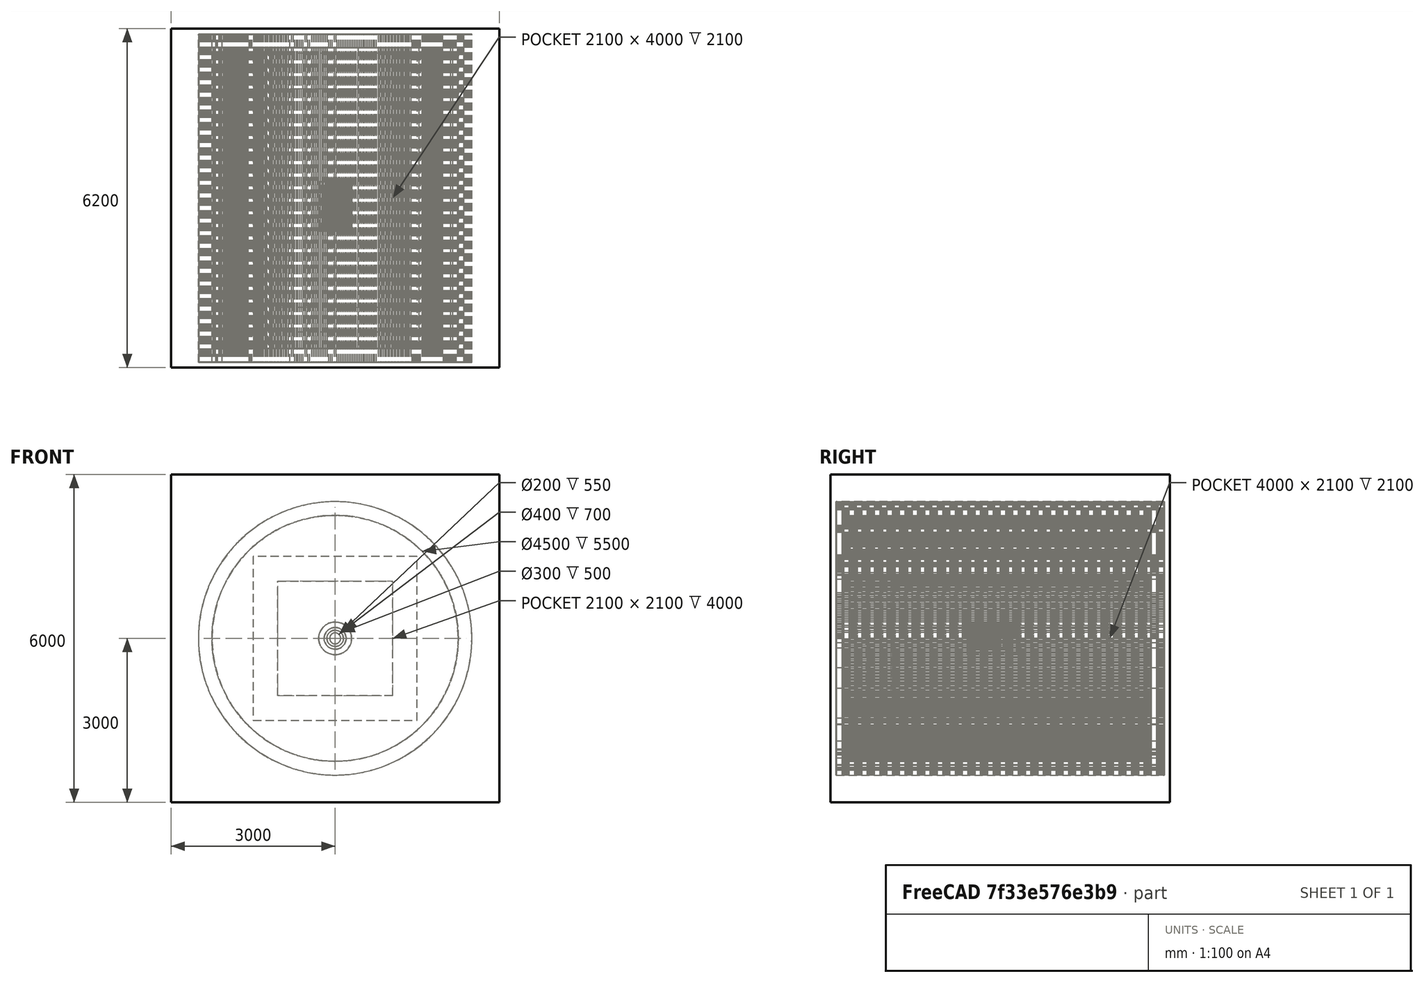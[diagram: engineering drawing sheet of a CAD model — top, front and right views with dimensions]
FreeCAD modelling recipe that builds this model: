
FCSTD DOCUMENT  (FreeCAD 1.0R39109 (Git))
Label: BeamDumpGDML_Optimized_01
License: All rights reserved
LicenseURL: https://en.wikipedia.org/wiki/All_rights_reserved
objects: App::DocumentObjectGroupPython×1252, Sketcher::SketchObject×8, PartDesign::Pad×6, Part::FeaturePython×5, App::Part×5, PartDesign::Body×4, Spreadsheet::Sheet×3, PartDesign::Revolution×2
note: 49 computed .brp shape members not serialized (recipe doc carries the construction recipe); baked Part::Feature solids carry a one-line shape summary decoded from their .brp

FEATURE [Spreadsheet::Sheet] defines
  cells = A1='constant; B1='HALFPI; C1(HALFPI)==pi / 2; A2='constant; B2='PI; C2(PI)==1 * pi; A3='constant; B3='TWOPI; C3(TWOPI)==2 * pi
FEATURE [Spreadsheet::Sheet] gdmlInfo
FEATURE [App::DocumentObjectGroupPython] Define  # scripted group (container) (typed FeaturePython)
  Group = -> [defines,gdmlInfo]
FEATURE [App::DocumentObjectGroupPython] HALFPI  # scripted group (container) (typed FeaturePython)
  name = HALFPI
  value = pi/2.
FEATURE [App::DocumentObjectGroupPython] PI  # scripted group (container) (typed FeaturePython)
  name = PI
  value = 1.*pi
FEATURE [App::DocumentObjectGroupPython] TWOPI  # scripted group (container) (typed FeaturePython)
  name = TWOPI
  value = 2.*pi
FEATURE [App::DocumentObjectGroupPython] Constants  # scripted group (container) (typed FeaturePython)
  Group = -> [HALFPI,PI,TWOPI]
FEATURE [App::DocumentObjectGroupPython] Quantities  # scripted group (container) (typed FeaturePython)
FEATURE [App::DocumentObjectGroupPython] Variables  # scripted group (container) (typed FeaturePython)
FEATURE [App::DocumentObjectGroupPython] Isotopes  # scripted group (container) (typed FeaturePython)
FEATURE [App::DocumentObjectGroupPython] Elements  # scripted group (container) (typed FeaturePython)
FEATURE [App::DocumentObjectGroupPython] Matrix  # scripted group (container) (typed FeaturePython)
FEATURE [App::DocumentObjectGroupPython] Surfaces  # scripted group (container) (typed FeaturePython)
FEATURE [App::DocumentObjectGroupPython] Opticals  # scripted group (container) (typed FeaturePython)
  Group = -> [Matrix,Surfaces]
FEATURE [App::DocumentObjectGroupPython] G4Isotopes  # scripted group (container) (typed FeaturePython)
FEATURE [App::DocumentObjectGroupPython] H_element  # scripted group (container) (typed FeaturePython)
  Z = 1
  atom_value = 1.008
  formula = H
  name = H_element
FEATURE [App::DocumentObjectGroupPython] He_element  # scripted group (container) (typed FeaturePython)
  Z = 2
  atom_value = 4.0026
  formula = He
  name = He_element
FEATURE [App::DocumentObjectGroupPython] Li_element  # scripted group (container) (typed FeaturePython)
  Z = 3
  atom_value = 6.94
  formula = Li
  name = Li_element
FEATURE [App::DocumentObjectGroupPython] Be_element  # scripted group (container) (typed FeaturePython)
  Z = 4
  atom_value = 9.01218
  formula = Be
  name = Be_element
FEATURE [App::DocumentObjectGroupPython] B_element  # scripted group (container) (typed FeaturePython)
  Z = 5
  atom_value = 10.81
  formula = B
  name = B_element
FEATURE [App::DocumentObjectGroupPython] C_element  # scripted group (container) (typed FeaturePython)
  Z = 6
  atom_value = 12.011
  formula = C
  name = C_element
FEATURE [App::DocumentObjectGroupPython] N_element  # scripted group (container) (typed FeaturePython)
  Z = 7
  atom_value = 14.007
  formula = N
  name = N_element
FEATURE [App::DocumentObjectGroupPython] O_element  # scripted group (container) (typed FeaturePython)
  Z = 8
  atom_value = 15.999
  formula = O
  name = O_element
FEATURE [App::DocumentObjectGroupPython] F_element  # scripted group (container) (typed FeaturePython)
  Z = 9
  atom_value = 18.9984
  formula = F
  name = F_element
FEATURE [App::DocumentObjectGroupPython] Ne_element  # scripted group (container) (typed FeaturePython)
  Z = 10
  atom_value = 20.1797
  formula = Ne
  name = Ne_element
FEATURE [App::DocumentObjectGroupPython] Na_element  # scripted group (container) (typed FeaturePython)
  Z = 11
  atom_value = 22.9898
  formula = Na
  name = Na_element
FEATURE [App::DocumentObjectGroupPython] Mg_element  # scripted group (container) (typed FeaturePython)
  Z = 12
  atom_value = 24.305
  formula = Mg
  name = Mg_element
FEATURE [App::DocumentObjectGroupPython] Al_element  # scripted group (container) (typed FeaturePython)
  Z = 13
  atom_value = 26.9815
  formula = Al
  name = Al_element
FEATURE [App::DocumentObjectGroupPython] Si_element  # scripted group (container) (typed FeaturePython)
  Z = 14
  atom_value = 28.085
  formula = Si
  name = Si_element
FEATURE [App::DocumentObjectGroupPython] P_element  # scripted group (container) (typed FeaturePython)
  Z = 15
  atom_value = 30.9738
  formula = P
  name = P_element
FEATURE [App::DocumentObjectGroupPython] S_element  # scripted group (container) (typed FeaturePython)
  Z = 16
  atom_value = 32.06
  formula = S
  name = S_element
FEATURE [App::DocumentObjectGroupPython] Cl_element  # scripted group (container) (typed FeaturePython)
  Z = 17
  atom_value = 35.45
  formula = Cl
  name = Cl_element
FEATURE [App::DocumentObjectGroupPython] Ar_element  # scripted group (container) (typed FeaturePython)
  Z = 18
  atom_value = 39.95
  formula = Ar
  name = Ar_element
FEATURE [App::DocumentObjectGroupPython] K_element  # scripted group (container) (typed FeaturePython)
  Z = 19
  atom_value = 39.0983
  formula = K
  name = K_element
FEATURE [App::DocumentObjectGroupPython] Ca_element  # scripted group (container) (typed FeaturePython)
  Z = 20
  atom_value = 40.078
  formula = Ca
  name = Ca_element
FEATURE [App::DocumentObjectGroupPython] Sc_element  # scripted group (container) (typed FeaturePython)
  Z = 21
  atom_value = 44.9559
  formula = Sc
  name = Sc_element
FEATURE [App::DocumentObjectGroupPython] Ti_element  # scripted group (container) (typed FeaturePython)
  Z = 22
  atom_value = 47.867
  formula = Ti
  name = Ti_element
FEATURE [App::DocumentObjectGroupPython] V_element  # scripted group (container) (typed FeaturePython)
  Z = 23
  atom_value = 50.9415
  formula = V
  name = V_element
FEATURE [App::DocumentObjectGroupPython] Cr_element  # scripted group (container) (typed FeaturePython)
  Z = 24
  atom_value = 51.9961
  formula = Cr
  name = Cr_element
FEATURE [App::DocumentObjectGroupPython] Mn_element  # scripted group (container) (typed FeaturePython)
  Z = 25
  atom_value = 54.938
  formula = Mn
  name = Mn_element
FEATURE [App::DocumentObjectGroupPython] Fe_element  # scripted group (container) (typed FeaturePython)
  Z = 26
  atom_value = 55.845
  formula = Fe
  name = Fe_element
FEATURE [App::DocumentObjectGroupPython] Co_element  # scripted group (container) (typed FeaturePython)
  Z = 27
  atom_value = 58.9332
  formula = Co
  name = Co_element
FEATURE [App::DocumentObjectGroupPython] Ni_element  # scripted group (container) (typed FeaturePython)
  Z = 28
  atom_value = 58.6934
  formula = Ni
  name = Ni_element
FEATURE [App::DocumentObjectGroupPython] Cu_element  # scripted group (container) (typed FeaturePython)
  Z = 29
  atom_value = 63.546
  formula = Cu
  name = Cu_element
FEATURE [App::DocumentObjectGroupPython] Zn_element  # scripted group (container) (typed FeaturePython)
  Z = 30
  atom_value = 65.38
  formula = Zn
  name = Zn_element
FEATURE [App::DocumentObjectGroupPython] Ga_element  # scripted group (container) (typed FeaturePython)
  Z = 31
  atom_value = 69.723
  formula = Ga
  name = Ga_element
FEATURE [App::DocumentObjectGroupPython] Ge_element  # scripted group (container) (typed FeaturePython)
  Z = 32
  atom_value = 72.63
  formula = Ge
  name = Ge_element
FEATURE [App::DocumentObjectGroupPython] As_element  # scripted group (container) (typed FeaturePython)
  Z = 33
  atom_value = 74.9216
  formula = As
  name = As_element
FEATURE [App::DocumentObjectGroupPython] Se_element  # scripted group (container) (typed FeaturePython)
  Z = 34
  atom_value = 78.971
  formula = Se
  name = Se_element
FEATURE [App::DocumentObjectGroupPython] Br_element  # scripted group (container) (typed FeaturePython)
  Z = 35
  atom_value = 79.904
  formula = Br
  name = Br_element
FEATURE [App::DocumentObjectGroupPython] Kr_element  # scripted group (container) (typed FeaturePython)
  Z = 36
  atom_value = 83.798
  formula = Kr
  name = Kr_element
FEATURE [App::DocumentObjectGroupPython] Rb_element  # scripted group (container) (typed FeaturePython)
  Z = 37
  atom_value = 85.4678
  formula = Rb
  name = Rb_element
FEATURE [App::DocumentObjectGroupPython] Sr_element  # scripted group (container) (typed FeaturePython)
  Z = 38
  atom_value = 87.62
  formula = Sr
  name = Sr_element
FEATURE [App::DocumentObjectGroupPython] Y_element  # scripted group (container) (typed FeaturePython)
  Z = 39
  atom_value = 88.9058
  formula = Y
  name = Y_element
FEATURE [App::DocumentObjectGroupPython] Zr_element  # scripted group (container) (typed FeaturePython)
  Z = 40
  atom_value = 91.224
  formula = Zr
  name = Zr_element
FEATURE [App::DocumentObjectGroupPython] Nb_element  # scripted group (container) (typed FeaturePython)
  Z = 41
  atom_value = 92.9064
  formula = Nb
  name = Nb_element
FEATURE [App::DocumentObjectGroupPython] Mo_element  # scripted group (container) (typed FeaturePython)
  Z = 42
  atom_value = 95.95
  formula = Mo
  name = Mo_element
FEATURE [App::DocumentObjectGroupPython] Tc_element  # scripted group (container) (typed FeaturePython)
  Z = 43
  atom_value = 97
  formula = Tc
  name = Tc_element
FEATURE [App::DocumentObjectGroupPython] Ru_element  # scripted group (container) (typed FeaturePython)
  Z = 44
  atom_value = 101.07
  formula = Ru
  name = Ru_element
FEATURE [App::DocumentObjectGroupPython] Rh_element  # scripted group (container) (typed FeaturePython)
  Z = 45
  atom_value = 102.905
  formula = Rh
  name = Rh_element
FEATURE [App::DocumentObjectGroupPython] Pd_element  # scripted group (container) (typed FeaturePython)
  Z = 46
  atom_value = 106.42
  formula = Pd
  name = Pd_element
FEATURE [App::DocumentObjectGroupPython] Ag_element  # scripted group (container) (typed FeaturePython)
  Z = 47
  atom_value = 107.868
  formula = Ag
  name = Ag_element
FEATURE [App::DocumentObjectGroupPython] Cd_element  # scripted group (container) (typed FeaturePython)
  Z = 48
  atom_value = 112.414
  formula = Cd
  name = Cd_element
FEATURE [App::DocumentObjectGroupPython] In_element  # scripted group (container) (typed FeaturePython)
  Z = 49
  atom_value = 114.818
  formula = In
  name = In_element
FEATURE [App::DocumentObjectGroupPython] Sn_element  # scripted group (container) (typed FeaturePython)
  Z = 50
  atom_value = 118.71
  formula = Sn
  name = Sn_element
FEATURE [App::DocumentObjectGroupPython] Sb_element  # scripted group (container) (typed FeaturePython)
  Z = 51
  atom_value = 121.76
  formula = Sb
  name = Sb_element
FEATURE [App::DocumentObjectGroupPython] Te_element  # scripted group (container) (typed FeaturePython)
  Z = 52
  atom_value = 127.6
  formula = Te
  name = Te_element
FEATURE [App::DocumentObjectGroupPython] I_element  # scripted group (container) (typed FeaturePython)
  Z = 53
  atom_value = 126.904
  formula = I
  name = I_element
FEATURE [App::DocumentObjectGroupPython] Xe_element  # scripted group (container) (typed FeaturePython)
  Z = 54
  atom_value = 131.293
  formula = Xe
  name = Xe_element
FEATURE [App::DocumentObjectGroupPython] Cs_element  # scripted group (container) (typed FeaturePython)
  Z = 55
  atom_value = 132.905
  formula = Cs
  name = Cs_element
FEATURE [App::DocumentObjectGroupPython] Ba_element  # scripted group (container) (typed FeaturePython)
  Z = 56
  atom_value = 137.327
  formula = Ba
  name = Ba_element
FEATURE [App::DocumentObjectGroupPython] La_element  # scripted group (container) (typed FeaturePython)
  Z = 57
  atom_value = 138.905
  formula = La
  name = La_element
FEATURE [App::DocumentObjectGroupPython] Ce_element  # scripted group (container) (typed FeaturePython)
  Z = 58
  atom_value = 140.116
  formula = Ce
  name = Ce_element
FEATURE [App::DocumentObjectGroupPython] Pr_element  # scripted group (container) (typed FeaturePython)
  Z = 59
  atom_value = 140.908
  formula = Pr
  name = Pr_element
FEATURE [App::DocumentObjectGroupPython] Nd_element  # scripted group (container) (typed FeaturePython)
  Z = 60
  atom_value = 144.242
  formula = Nd
  name = Nd_element
FEATURE [App::DocumentObjectGroupPython] Pm_element  # scripted group (container) (typed FeaturePython)
  Z = 61
  atom_value = 145
  formula = Pm
  name = Pm_element
FEATURE [App::DocumentObjectGroupPython] Sm_element  # scripted group (container) (typed FeaturePython)
  Z = 62
  atom_value = 150.36
  formula = Sm
  name = Sm_element
FEATURE [App::DocumentObjectGroupPython] Eu_element  # scripted group (container) (typed FeaturePython)
  Z = 63
  atom_value = 151.964
  formula = Eu
  name = Eu_element
FEATURE [App::DocumentObjectGroupPython] Gd_element  # scripted group (container) (typed FeaturePython)
  Z = 64
  atom_value = 157.25
  formula = Gd
  name = Gd_element
FEATURE [App::DocumentObjectGroupPython] Tb_element  # scripted group (container) (typed FeaturePython)
  Z = 65
  atom_value = 158.925
  formula = Tb
  name = Tb_element
FEATURE [App::DocumentObjectGroupPython] Dy_element  # scripted group (container) (typed FeaturePython)
  Z = 66
  atom_value = 162.5
  formula = Dy
  name = Dy_element
FEATURE [App::DocumentObjectGroupPython] Ho_element  # scripted group (container) (typed FeaturePython)
  Z = 67
  atom_value = 164.93
  formula = Ho
  name = Ho_element
FEATURE [App::DocumentObjectGroupPython] Er_element  # scripted group (container) (typed FeaturePython)
  Z = 68
  atom_value = 167.259
  formula = Er
  name = Er_element
FEATURE [App::DocumentObjectGroupPython] Tm_element  # scripted group (container) (typed FeaturePython)
  Z = 69
  atom_value = 168.934
  formula = Tm
  name = Tm_element
FEATURE [App::DocumentObjectGroupPython] Yb_element  # scripted group (container) (typed FeaturePython)
  Z = 70
  atom_value = 173.045
  formula = Yb
  name = Yb_element
FEATURE [App::DocumentObjectGroupPython] Lu_element  # scripted group (container) (typed FeaturePython)
  Z = 71
  atom_value = 174.967
  formula = Lu
  name = Lu_element
FEATURE [App::DocumentObjectGroupPython] Hf_element  # scripted group (container) (typed FeaturePython)
  Z = 72
  atom_value = 178.49
  formula = Hf
  name = Hf_element
FEATURE [App::DocumentObjectGroupPython] Ta_element  # scripted group (container) (typed FeaturePython)
  Z = 73
  atom_value = 180.948
  formula = Ta
  name = Ta_element
FEATURE [App::DocumentObjectGroupPython] W_element  # scripted group (container) (typed FeaturePython)
  Z = 74
  atom_value = 183.84
  formula = W
  name = W_element
FEATURE [App::DocumentObjectGroupPython] Re_element  # scripted group (container) (typed FeaturePython)
  Z = 75
  atom_value = 186.207
  formula = Re
  name = Re_element
FEATURE [App::DocumentObjectGroupPython] Os_element  # scripted group (container) (typed FeaturePython)
  Z = 76
  atom_value = 190.23
  formula = Os
  name = Os_element
FEATURE [App::DocumentObjectGroupPython] Ir_element  # scripted group (container) (typed FeaturePython)
  Z = 77
  atom_value = 192.217
  formula = Ir
  name = Ir_element
FEATURE [App::DocumentObjectGroupPython] Pt_element  # scripted group (container) (typed FeaturePython)
  Z = 78
  atom_value = 195.084
  formula = Pt
  name = Pt_element
FEATURE [App::DocumentObjectGroupPython] Au_element  # scripted group (container) (typed FeaturePython)
  Z = 79
  atom_value = 196.967
  formula = Au
  name = Au_element
FEATURE [App::DocumentObjectGroupPython] Hg_element  # scripted group (container) (typed FeaturePython)
  Z = 80
  atom_value = 200.592
  formula = Hg
  name = Hg_element
FEATURE [App::DocumentObjectGroupPython] Tl_element  # scripted group (container) (typed FeaturePython)
  Z = 81
  atom_value = 204.38
  formula = Tl
  name = Tl_element
FEATURE [App::DocumentObjectGroupPython] Pb_element  # scripted group (container) (typed FeaturePython)
  Z = 82
  atom_value = 207.2
  formula = Pb
  name = Pb_element
FEATURE [App::DocumentObjectGroupPython] Bi_element  # scripted group (container) (typed FeaturePython)
  Z = 83
  atom_value = 208.98
  formula = Bi
  name = Bi_element
FEATURE [App::DocumentObjectGroupPython] Po_element  # scripted group (container) (typed FeaturePython)
  Z = 84
  atom_value = 209
  formula = Po
  name = Po_element
FEATURE [App::DocumentObjectGroupPython] At_element  # scripted group (container) (typed FeaturePython)
  Z = 85
  atom_value = 210
  formula = At
  name = At_element
FEATURE [App::DocumentObjectGroupPython] Rn_element  # scripted group (container) (typed FeaturePython)
  Z = 86
  atom_value = 222
  formula = Rn
  name = Rn_element
FEATURE [App::DocumentObjectGroupPython] Fr_element  # scripted group (container) (typed FeaturePython)
  Z = 87
  atom_value = 223
  formula = Fr
  name = Fr_element
FEATURE [App::DocumentObjectGroupPython] Ra_element  # scripted group (container) (typed FeaturePython)
  Z = 88
  atom_value = 226
  formula = Ra
  name = Ra_element
FEATURE [App::DocumentObjectGroupPython] Ac_element  # scripted group (container) (typed FeaturePython)
  Z = 89
  atom_value = 227
  formula = Ac
  name = Ac_element
FEATURE [App::DocumentObjectGroupPython] Th_element  # scripted group (container) (typed FeaturePython)
  Z = 90
  atom_value = 232.038
  formula = Th
  name = Th_element
FEATURE [App::DocumentObjectGroupPython] Pa_element  # scripted group (container) (typed FeaturePython)
  Z = 91
  atom_value = 231.036
  formula = Pa
  name = Pa_element
FEATURE [App::DocumentObjectGroupPython] U_element  # scripted group (container) (typed FeaturePython)
  Z = 92
  atom_value = 238.029
  formula = U
  name = U_element
FEATURE [App::DocumentObjectGroupPython] Np_element  # scripted group (container) (typed FeaturePython)
  Z = 93
  atom_value = 237
  formula = Np
  name = Np_element
FEATURE [App::DocumentObjectGroupPython] Pu_element  # scripted group (container) (typed FeaturePython)
  Z = 94
  atom_value = 244
  formula = Pu
  name = Pu_element
FEATURE [App::DocumentObjectGroupPython] Am_element  # scripted group (container) (typed FeaturePython)
  Z = 95
  atom_value = 243
  formula = Am
  name = Am_element
FEATURE [App::DocumentObjectGroupPython] Cm_element  # scripted group (container) (typed FeaturePython)
  Z = 96
  atom_value = 247
  formula = Cm
  name = Cm_element
FEATURE [App::DocumentObjectGroupPython] Bk_element  # scripted group (container) (typed FeaturePython)
  Z = 97
  atom_value = 247
  formula = Bk
  name = Bk_element
FEATURE [App::DocumentObjectGroupPython] Cf_element  # scripted group (container) (typed FeaturePython)
  Z = 98
  atom_value = 251
  formula = Cf
  name = Cf_element
FEATURE [App::DocumentObjectGroupPython] G4Elements  # scripted group (container) (typed FeaturePython)
  Group = -> [H_element,He_element,Li_element,Be_element,B_element,C_element,N_element,O_element,F_element,Ne_element,Na_element,Mg_element,Al_element,Si_element,P_element,S_element,Cl_element,Ar_element,K_element,Ca_element,Sc_element,Ti_element,V_element,Cr_element,Mn_element,Fe_element,Co_element,Ni_element,Cu_element,Zn_element,Ga_element,Ge_element,As_element,Se_element,Br_element,Kr_element,Rb_element,+61 more]
FEATURE [App::DocumentObjectGroupPython] H_element001  label="H_element : 0.101"  # scripted group (container) (typed FeaturePython)
  n = 0.101327
FEATURE [App::DocumentObjectGroupPython] C_element001  label="C_element : 0.775"  # scripted group (container) (typed FeaturePython)
  n = 0.7755
FEATURE [App::DocumentObjectGroupPython] N_element001  label="N_element : 0.035"  # scripted group (container) (typed FeaturePython)
  n = 0.035057
FEATURE [App::DocumentObjectGroupPython] O_element001  label="O_element : 0.052"  # scripted group (container) (typed FeaturePython)
  n = 0.0523159
FEATURE [App::DocumentObjectGroupPython] F_element001  label="F_element : 0.017"  # scripted group (container) (typed FeaturePython)
  n = 0.017422
FEATURE [App::DocumentObjectGroupPython] Ca_element001  label="Ca_element : 0.018"  # scripted group (container) (typed FeaturePython)
  n = 0.018378
FEATURE [App::DocumentObjectGroupPython] G4_A_150_TISSUE  label="G4_A-150_TISSUE"  # scripted group (container) (typed FeaturePython)
  Dunit = g/cm3
  Dvalue = 1.127
  Group = -> [H_element001,C_element001,N_element001,O_element001,F_element001,Ca_element001]
  conduct = 2
  density = 1
  expand = 3
  formula = G4_A-150_TISSUE
  name = G4_A-150_TISSUE
  specific = 4
FEATURE [App::DocumentObjectGroupPython] C_element002  label="C_element : 3"  # scripted group (container) (typed FeaturePython)
  n = 3
  ref = C_element
FEATURE [App::DocumentObjectGroupPython] H_element002  label="H_element : 6"  # scripted group (container) (typed FeaturePython)
  n = 6
  ref = H_element
FEATURE [App::DocumentObjectGroupPython] O_element002  label="O_element : 1"  # scripted group (container) (typed FeaturePython)
  n = 1
  ref = O_element
FEATURE [App::DocumentObjectGroupPython] G4_ACETONE  # scripted group (container) (typed FeaturePython)
  Dunit = g/cm3
  Dvalue = 0.7899
  Group = -> [C_element002,H_element002,O_element002]
  conduct = 2
  density = 1
  expand = 3
  formula = G4_ACETONE
  name = G4_ACETONE
  specific = 4
FEATURE [App::DocumentObjectGroupPython] C_element003  label="C_element : 2"  # scripted group (container) (typed FeaturePython)
  n = 2
  ref = C_element
FEATURE [App::DocumentObjectGroupPython] H_element003  label="H_element : 2"  # scripted group (container) (typed FeaturePython)
  n = 2
  ref = H_element
FEATURE [App::DocumentObjectGroupPython] G4_ACETYLENE  # scripted group (container) (typed FeaturePython)
  Dunit = g/cm3
  Dvalue = 0.0010967
  Group = -> [C_element003,H_element003]
  conduct = 2
  density = 1
  expand = 3
  formula = G4_ACETYLENE
  name = G4_ACETYLENE
  specific = 4
FEATURE [App::DocumentObjectGroupPython] C_element004  label="C_element : 5"  # scripted group (container) (typed FeaturePython)
  n = 5
  ref = C_element
FEATURE [App::DocumentObjectGroupPython] H_element004  label="H_element : 5"  # scripted group (container) (typed FeaturePython)
  n = 5
  ref = H_element
FEATURE [App::DocumentObjectGroupPython] N_element002  label="N_element : 5"  # scripted group (container) (typed FeaturePython)
  n = 5
  ref = N_element
FEATURE [App::DocumentObjectGroupPython] G4_ADENINE  # scripted group (container) (typed FeaturePython)
  Dunit = g/cm3
  Dvalue = 1.6
  Group = -> [C_element004,H_element004,N_element002]
  conduct = 2
  density = 1
  expand = 3
  formula = G4_ADENINE
  name = G4_ADENINE
  specific = 4
FEATURE [App::DocumentObjectGroupPython] H_element005  label="H_element : 0.114"  # scripted group (container) (typed FeaturePython)
  n = 0.114
FEATURE [App::DocumentObjectGroupPython] C_element005  label="C_element : 0.598"  # scripted group (container) (typed FeaturePython)
  n = 0.598
FEATURE [App::DocumentObjectGroupPython] N_element003  label="N_element : 0.007"  # scripted group (container) (typed FeaturePython)
  n = 0.007
FEATURE [App::DocumentObjectGroupPython] O_element003  label="O_element : 0.278"  # scripted group (container) (typed FeaturePython)
  n = 0.278
FEATURE [App::DocumentObjectGroupPython] Na_element001  label="Na_element : 0.001"  # scripted group (container) (typed FeaturePython)
  n = 0.001
FEATURE [App::DocumentObjectGroupPython] S_element001  label="S_element : 0.001"  # scripted group (container) (typed FeaturePython)
  n = 0.001
FEATURE [App::DocumentObjectGroupPython] Cl_element001  label="Cl_element : 0.001"  # scripted group (container) (typed FeaturePython)
  n = 0.001
FEATURE [App::DocumentObjectGroupPython] G4_ADIPOSE_TISSUE_ICRP  # scripted group (container) (typed FeaturePython)
  Dunit = g/cm3
  Dvalue = 0.95
  Group = -> [H_element005,C_element005,N_element003,O_element003,Na_element001,S_element001,Cl_element001]
  conduct = 2
  density = 1
  expand = 3
  formula = G4_ADIPOSE_TISSUE_ICRP
  name = G4_ADIPOSE_TISSUE_ICRP
  specific = 4
FEATURE [App::DocumentObjectGroupPython] C_element006  label="C_element : 0.000"  # scripted group (container) (typed FeaturePython)
  n = 0.000124
FEATURE [App::DocumentObjectGroupPython] N_element004  label="N_element : 0.755"  # scripted group (container) (typed FeaturePython)
  n = 0.755268
FEATURE [App::DocumentObjectGroupPython] O_element004  label="O_element : 0.232"  # scripted group (container) (typed FeaturePython)
  n = 0.231781
FEATURE [App::DocumentObjectGroupPython] Ar_element001  label="Ar_element : 0.013"  # scripted group (container) (typed FeaturePython)
  n = 0.012827
FEATURE [App::DocumentObjectGroupPython] G4_AIR  # scripted group (container) (typed FeaturePython)
  Dunit = g/cm3
  Dvalue = 0.00120479
  Group = -> [C_element006,N_element004,O_element004,Ar_element001]
  conduct = 2
  density = 1
  expand = 3
  formula = G4_AIR
  name = G4_AIR
  specific = 4
FEATURE [App::DocumentObjectGroupPython] C_element007  label="C_element : 006"  # scripted group (container) (typed FeaturePython)
  n = 3
  ref = C_element
FEATURE [App::DocumentObjectGroupPython] H_element006  label="H_element : 7"  # scripted group (container) (typed FeaturePython)
  n = 7
  ref = H_element
FEATURE [App::DocumentObjectGroupPython] N_element005  label="N_element : 1"  # scripted group (container) (typed FeaturePython)
  n = 1
  ref = N_element
FEATURE [App::DocumentObjectGroupPython] O_element005  label="O_element : 2"  # scripted group (container) (typed FeaturePython)
  n = 2
  ref = O_element
FEATURE [App::DocumentObjectGroupPython] G4_ALANINE  # scripted group (container) (typed FeaturePython)
  Dunit = g/cm3
  Dvalue = 1.42
  Group = -> [C_element007,H_element006,N_element005,O_element005]
  conduct = 2
  density = 1
  expand = 3
  formula = G4_ALANINE
  name = G4_ALANINE
  specific = 4
FEATURE [App::DocumentObjectGroupPython] Al_element001  label="Al_element : 2"  # scripted group (container) (typed FeaturePython)
  n = 2
  ref = Al_element
FEATURE [App::DocumentObjectGroupPython] O_element006  label="O_element : 3"  # scripted group (container) (typed FeaturePython)
  n = 3
  ref = O_element
FEATURE [App::DocumentObjectGroupPython] G4_ALUMINUM_OXIDE  # scripted group (container) (typed FeaturePython)
  Dunit = g/cm3
  Dvalue = 3.97
  Group = -> [Al_element001,O_element006]
  conduct = 2
  density = 1
  expand = 3
  formula = G4_ALUMINUM_OXIDE
  name = G4_ALUMINUM_OXIDE
  specific = 4
FEATURE [App::DocumentObjectGroupPython] H_element007  label="H_element : 0.106"  # scripted group (container) (typed FeaturePython)
  n = 0.10593
FEATURE [App::DocumentObjectGroupPython] C_element008  label="C_element : 0.789"  # scripted group (container) (typed FeaturePython)
  n = 0.788974
FEATURE [App::DocumentObjectGroupPython] O_element007  label="O_element : 0.105"  # scripted group (container) (typed FeaturePython)
  n = 0.105096
FEATURE [App::DocumentObjectGroupPython] G4_AMBER  # scripted group (container) (typed FeaturePython)
  Dunit = g/cm3
  Dvalue = 1.1
  Group = -> [H_element007,C_element008,O_element007]
  conduct = 2
  density = 1
  expand = 3
  formula = G4_AMBER
  name = G4_AMBER
  specific = 4
FEATURE [App::DocumentObjectGroupPython] N_element006  label="N_element : 006"  # scripted group (container) (typed FeaturePython)
  n = 1
  ref = N_element
FEATURE [App::DocumentObjectGroupPython] H_element008  label="H_element : 3"  # scripted group (container) (typed FeaturePython)
  n = 3
  ref = H_element
FEATURE [App::DocumentObjectGroupPython] G4_AMMONIA  # scripted group (container) (typed FeaturePython)
  Dunit = g/cm3
  Dvalue = 0.000826019
  Group = -> [N_element006,H_element008]
  conduct = 2
  density = 1
  expand = 3
  formula = G4_AMMONIA
  name = G4_AMMONIA
  specific = 4
FEATURE [App::DocumentObjectGroupPython] C_element009  label="C_element : 6"  # scripted group (container) (typed FeaturePython)
  n = 6
  ref = C_element
FEATURE [App::DocumentObjectGroupPython] H_element009  label="H_element : 008"  # scripted group (container) (typed FeaturePython)
  n = 7
  ref = H_element
FEATURE [App::DocumentObjectGroupPython] N_element007  label="N_element : 007"  # scripted group (container) (typed FeaturePython)
  n = 1
  ref = N_element
FEATURE [App::DocumentObjectGroupPython] G4_ANILINE  # scripted group (container) (typed FeaturePython)
  Dunit = g/cm3
  Dvalue = 1.0235
  Group = -> [C_element009,H_element009,N_element007]
  conduct = 2
  density = 1
  expand = 3
  formula = G4_ANILINE
  name = G4_ANILINE
  specific = 4
FEATURE [App::DocumentObjectGroupPython] C_element010  label="C_element : 14"  # scripted group (container) (typed FeaturePython)
  n = 14
  ref = C_element
FEATURE [App::DocumentObjectGroupPython] H_element010  label="H_element : 10"  # scripted group (container) (typed FeaturePython)
  n = 10
  ref = H_element
FEATURE [App::DocumentObjectGroupPython] G4_ANTHRACENE  # scripted group (container) (typed FeaturePython)
  Dunit = g/cm3
  Dvalue = 1.283
  Group = -> [C_element010,H_element010]
  conduct = 2
  density = 1
  expand = 3
  formula = G4_ANTHRACENE
  name = G4_ANTHRACENE
  specific = 4
FEATURE [App::DocumentObjectGroupPython] H_element011  label="H_element : 0.065"  # scripted group (container) (typed FeaturePython)
  n = 0.0654709
FEATURE [App::DocumentObjectGroupPython] C_element011  label="C_element : 0.537"  # scripted group (container) (typed FeaturePython)
  n = 0.536944
FEATURE [App::DocumentObjectGroupPython] N_element008  label="N_element : 0.021"  # scripted group (container) (typed FeaturePython)
  n = 0.0215
FEATURE [App::DocumentObjectGroupPython] O_element008  label="O_element : 0.032"  # scripted group (container) (typed FeaturePython)
  n = 0.032085
FEATURE [App::DocumentObjectGroupPython] F_element002  label="F_element : 0.167"  # scripted group (container) (typed FeaturePython)
  n = 0.167411
FEATURE [App::DocumentObjectGroupPython] Ca_element002  label="Ca_element : 0.177"  # scripted group (container) (typed FeaturePython)
  n = 0.176589
FEATURE [App::DocumentObjectGroupPython] G4_B_100_BONE  label="G4_B-100_BONE"  # scripted group (container) (typed FeaturePython)
  Dunit = g/cm3
  Dvalue = 1.45
  Group = -> [H_element011,C_element011,N_element008,O_element008,F_element002,Ca_element002]
  conduct = 2
  density = 1
  expand = 3
  formula = G4_B-100_BONE
  name = G4_B-100_BONE
  specific = 4
FEATURE [App::DocumentObjectGroupPython] H_element012  label="H_element : 0.057"  # scripted group (container) (typed FeaturePython)
  n = 0.057441
FEATURE [App::DocumentObjectGroupPython] C_element012  label="C_element : 0.790"  # scripted group (container) (typed FeaturePython)
  n = 0.774591
FEATURE [App::DocumentObjectGroupPython] O_element009  label="O_element : 0.168"  # scripted group (container) (typed FeaturePython)
  n = 0.167968
FEATURE [App::DocumentObjectGroupPython] G4_BAKELITE  # scripted group (container) (typed FeaturePython)
  Dunit = g/cm3
  Dvalue = 1.25
  Group = -> [H_element012,C_element012,O_element009]
  conduct = 2
  density = 1
  expand = 3
  formula = G4_BAKELITE
  name = G4_BAKELITE
  specific = 4
FEATURE [App::DocumentObjectGroupPython] Ba_element001  label="Ba_element : 1"  # scripted group (container) (typed FeaturePython)
  n = 1
  ref = Ba_element
FEATURE [App::DocumentObjectGroupPython] F_element003  label="F_element : 2"  # scripted group (container) (typed FeaturePython)
  n = 2
  ref = F_element
FEATURE [App::DocumentObjectGroupPython] G4_BARIUM_FLUORIDE  # scripted group (container) (typed FeaturePython)
  Dunit = g/cm3
  Dvalue = 4.89
  Group = -> [Ba_element001,F_element003]
  conduct = 2
  density = 1
  expand = 3
  formula = G4_BARIUM_FLUORIDE
  name = G4_BARIUM_FLUORIDE
  specific = 4
FEATURE [App::DocumentObjectGroupPython] Ba_element002  label="Ba_element : 002"  # scripted group (container) (typed FeaturePython)
  n = 1
  ref = Ba_element
FEATURE [App::DocumentObjectGroupPython] S_element002  label="S_element : 1"  # scripted group (container) (typed FeaturePython)
  n = 1
  ref = S_element
FEATURE [App::DocumentObjectGroupPython] O_element010  label="O_element : 4"  # scripted group (container) (typed FeaturePython)
  n = 4
  ref = O_element
FEATURE [App::DocumentObjectGroupPython] G4_BARIUM_SULFATE  # scripted group (container) (typed FeaturePython)
  Dunit = g/cm3
  Dvalue = 4.5
  Group = -> [Ba_element002,S_element002,O_element010]
  conduct = 2
  density = 1
  expand = 3
  formula = G4_BARIUM_SULFATE
  name = G4_BARIUM_SULFATE
  specific = 4
FEATURE [App::DocumentObjectGroupPython] C_element013  label="C_element : 007"  # scripted group (container) (typed FeaturePython)
  n = 6
  ref = C_element
FEATURE [App::DocumentObjectGroupPython] H_element013  label="H_element : 009"  # scripted group (container) (typed FeaturePython)
  n = 6
  ref = H_element
FEATURE [App::DocumentObjectGroupPython] G4_BENZENE  # scripted group (container) (typed FeaturePython)
  Dunit = g/cm3
  Dvalue = 0.87865
  Group = -> [C_element013,H_element013]
  conduct = 2
  density = 1
  expand = 3
  formula = G4_BENZENE
  name = G4_BENZENE
  specific = 4
FEATURE [App::DocumentObjectGroupPython] Be_element001  label="Be_element : 1"  # scripted group (container) (typed FeaturePython)
  n = 1
  ref = Be_element
FEATURE [App::DocumentObjectGroupPython] O_element011  label="O_element : 005"  # scripted group (container) (typed FeaturePython)
  n = 1
  ref = O_element
FEATURE [App::DocumentObjectGroupPython] G4_BERYLLIUM_OXIDE  # scripted group (container) (typed FeaturePython)
  Dunit = g/cm3
  Dvalue = 3.01
  Group = -> [Be_element001,O_element011]
  conduct = 2
  density = 1
  expand = 3
  formula = G4_BERYLLIUM_OXIDE
  name = G4_BERYLLIUM_OXIDE
  specific = 4
FEATURE [App::DocumentObjectGroupPython] Bi_element001  label="Bi_element : 4"  # scripted group (container) (typed FeaturePython)
  n = 4
  ref = Bi_element
FEATURE [App::DocumentObjectGroupPython] Ge_element001  label="Ge_element : 3"  # scripted group (container) (typed FeaturePython)
  n = 3
  ref = Ge_element
FEATURE [App::DocumentObjectGroupPython] O_element012  label="O_element : 12"  # scripted group (container) (typed FeaturePython)
  n = 12
  ref = O_element
FEATURE [App::DocumentObjectGroupPython] G4_BGO  # scripted group (container) (typed FeaturePython)
  Dunit = g/cm3
  Dvalue = 7.13
  Group = -> [Bi_element001,Ge_element001,O_element012]
  conduct = 2
  density = 1
  expand = 3
  formula = G4_BGO
  name = G4_BGO
  specific = 4
FEATURE [App::DocumentObjectGroupPython] H_element014  label="H_element : 0.102"  # scripted group (container) (typed FeaturePython)
  n = 0.102
FEATURE [App::DocumentObjectGroupPython] C_element014  label="C_element : 0.110"  # scripted group (container) (typed FeaturePython)
  n = 0.11
FEATURE [App::DocumentObjectGroupPython] N_element009  label="N_element : 0.033"  # scripted group (container) (typed FeaturePython)
  n = 0.033
FEATURE [App::DocumentObjectGroupPython] O_element013  label="O_element : 0.745"  # scripted group (container) (typed FeaturePython)
  n = 0.745
FEATURE [App::DocumentObjectGroupPython] Na_element002  label="Na_element : 0.002"  # scripted group (container) (typed FeaturePython)
  n = 0.001
FEATURE [App::DocumentObjectGroupPython] P_element001  label="P_element : 0.001"  # scripted group (container) (typed FeaturePython)
  n = 0.001
FEATURE [App::DocumentObjectGroupPython] S_element003  label="S_element : 0.002"  # scripted group (container) (typed FeaturePython)
  n = 0.002
FEATURE [App::DocumentObjectGroupPython] Cl_element002  label="Cl_element : 0.003"  # scripted group (container) (typed FeaturePython)
  n = 0.003
FEATURE [App::DocumentObjectGroupPython] K_element001  label="K_element : 0.002"  # scripted group (container) (typed FeaturePython)
  n = 0.002
FEATURE [App::DocumentObjectGroupPython] Fe_element001  label="Fe_element : 0.001"  # scripted group (container) (typed FeaturePython)
  n = 0.001
FEATURE [App::DocumentObjectGroupPython] G4_BLOOD_ICRP  # scripted group (container) (typed FeaturePython)
  Dunit = g/cm3
  Dvalue = 1.06
  Group = -> [H_element014,C_element014,N_element009,O_element013,Na_element002,P_element001,S_element003,Cl_element002,K_element001,Fe_element001]
  conduct = 2
  density = 1
  expand = 3
  formula = G4_BLOOD_ICRP
  name = G4_BLOOD_ICRP
  specific = 4
FEATURE [App::DocumentObjectGroupPython] H_element015  label="H_element : 0.064"  # scripted group (container) (typed FeaturePython)
  n = 0.064
FEATURE [App::DocumentObjectGroupPython] C_element015  label="C_element : 0.278"  # scripted group (container) (typed FeaturePython)
  n = 0.278
FEATURE [App::DocumentObjectGroupPython] N_element010  label="N_element : 0.027"  # scripted group (container) (typed FeaturePython)
  n = 0.027
FEATURE [App::DocumentObjectGroupPython] O_element014  label="O_element : 0.410"  # scripted group (container) (typed FeaturePython)
  n = 0.41
FEATURE [App::DocumentObjectGroupPython] Mg_element001  label="Mg_element : 0.002"  # scripted group (container) (typed FeaturePython)
  n = 0.002
FEATURE [App::DocumentObjectGroupPython] P_element002  label="P_element : 0.070"  # scripted group (container) (typed FeaturePython)
  n = 0.07
FEATURE [App::DocumentObjectGroupPython] S_element004  label="S_element : 0.003"  # scripted group (container) (typed FeaturePython)
  n = 0.002
FEATURE [App::DocumentObjectGroupPython] Ca_element003  label="Ca_element : 0.147"  # scripted group (container) (typed FeaturePython)
  n = 0.147
FEATURE [App::DocumentObjectGroupPython] G4_BONE_COMPACT_ICRU  # scripted group (container) (typed FeaturePython)
  Dunit = g/cm3
  Dvalue = 1.85
  Group = -> [H_element015,C_element015,N_element010,O_element014,Mg_element001,P_element002,S_element004,Ca_element003]
  conduct = 2
  density = 1
  expand = 3
  formula = G4_BONE_COMPACT_ICRU
  name = G4_BONE_COMPACT_ICRU
  specific = 4
FEATURE [App::DocumentObjectGroupPython] H_element016  label="H_element : 0.034"  # scripted group (container) (typed FeaturePython)
  n = 0.034
FEATURE [App::DocumentObjectGroupPython] C_element016  label="C_element : 0.155"  # scripted group (container) (typed FeaturePython)
  n = 0.155
FEATURE [App::DocumentObjectGroupPython] N_element011  label="N_element : 0.042"  # scripted group (container) (typed FeaturePython)
  n = 0.042
FEATURE [App::DocumentObjectGroupPython] O_element015  label="O_element : 0.435"  # scripted group (container) (typed FeaturePython)
  n = 0.435
FEATURE [App::DocumentObjectGroupPython] Na_element003  label="Na_element : 0.003"  # scripted group (container) (typed FeaturePython)
  n = 0.001
FEATURE [App::DocumentObjectGroupPython] Mg_element002  label="Mg_element : 0.003"  # scripted group (container) (typed FeaturePython)
  n = 0.002
FEATURE [App::DocumentObjectGroupPython] P_element003  label="P_element : 0.103"  # scripted group (container) (typed FeaturePython)
  n = 0.103
FEATURE [App::DocumentObjectGroupPython] S_element005  label="S_element : 0.004"  # scripted group (container) (typed FeaturePython)
  n = 0.003
FEATURE [App::DocumentObjectGroupPython] Ca_element004  label="Ca_element : 0.225"  # scripted group (container) (typed FeaturePython)
  n = 0.225
FEATURE [App::DocumentObjectGroupPython] G4_BONE_CORTICAL_ICRP  # scripted group (container) (typed FeaturePython)
  Dunit = g/cm3
  Dvalue = 1.92
  Group = -> [H_element016,C_element016,N_element011,O_element015,Na_element003,Mg_element002,P_element003,S_element005,Ca_element004]
  conduct = 2
  density = 1
  expand = 3
  formula = G4_BONE_CORTICAL_ICRP
  name = G4_BONE_CORTICAL_ICRP
  specific = 4
FEATURE [App::DocumentObjectGroupPython] B_element001  label="B_element : 4"  # scripted group (container) (typed FeaturePython)
  n = 4
  ref = B_element
FEATURE [App::DocumentObjectGroupPython] C_element017  label="C_element : 1"  # scripted group (container) (typed FeaturePython)
  n = 1
  ref = C_element
FEATURE [App::DocumentObjectGroupPython] G4_BORON_CARBIDE  # scripted group (container) (typed FeaturePython)
  Dunit = g/cm3
  Dvalue = 2.52
  Group = -> [B_element001,C_element017]
  conduct = 2
  density = 1
  expand = 3
  formula = G4_BORON_CARBIDE
  name = G4_BORON_CARBIDE
  specific = 4
FEATURE [App::DocumentObjectGroupPython] B_element002  label="B_element : 2"  # scripted group (container) (typed FeaturePython)
  n = 2
  ref = B_element
FEATURE [App::DocumentObjectGroupPython] O_element016  label="O_element : 006"  # scripted group (container) (typed FeaturePython)
  n = 3
  ref = O_element
FEATURE [App::DocumentObjectGroupPython] G4_BORON_OXIDE  # scripted group (container) (typed FeaturePython)
  Dunit = g/cm3
  Dvalue = 1.812
  Group = -> [B_element002,O_element016]
  conduct = 2
  density = 1
  expand = 3
  formula = G4_BORON_OXIDE
  name = G4_BORON_OXIDE
  specific = 4
FEATURE [App::DocumentObjectGroupPython] H_element017  label="H_element : 0.107"  # scripted group (container) (typed FeaturePython)
  n = 0.107
FEATURE [App::DocumentObjectGroupPython] C_element018  label="C_element : 0.145"  # scripted group (container) (typed FeaturePython)
  n = 0.145
FEATURE [App::DocumentObjectGroupPython] N_element012  label="N_element : 0.022"  # scripted group (container) (typed FeaturePython)
  n = 0.022
FEATURE [App::DocumentObjectGroupPython] O_element017  label="O_element : 0.712"  # scripted group (container) (typed FeaturePython)
  n = 0.712
FEATURE [App::DocumentObjectGroupPython] Na_element004  label="Na_element : 0.004"  # scripted group (container) (typed FeaturePython)
  n = 0.002
FEATURE [App::DocumentObjectGroupPython] P_element004  label="P_element : 0.004"  # scripted group (container) (typed FeaturePython)
  n = 0.004
FEATURE [App::DocumentObjectGroupPython] S_element006  label="S_element : 0.005"  # scripted group (container) (typed FeaturePython)
  n = 0.002
FEATURE [App::DocumentObjectGroupPython] Cl_element003  label="Cl_element : 0.004"  # scripted group (container) (typed FeaturePython)
  n = 0.003
FEATURE [App::DocumentObjectGroupPython] K_element002  label="K_element : 0.003"  # scripted group (container) (typed FeaturePython)
  n = 0.003
FEATURE [App::DocumentObjectGroupPython] G4_BRAIN_ICRP  # scripted group (container) (typed FeaturePython)
  Dunit = g/cm3
  Dvalue = 1.04
  Group = -> [H_element017,C_element018,N_element012,O_element017,Na_element004,P_element004,S_element006,Cl_element003,K_element002]
  conduct = 2
  density = 1
  expand = 3
  formula = G4_BRAIN_ICRP
  name = G4_BRAIN_ICRP
  specific = 4
FEATURE [App::DocumentObjectGroupPython] C_element019  label="C_element : 4"  # scripted group (container) (typed FeaturePython)
  n = 4
  ref = C_element
FEATURE [App::DocumentObjectGroupPython] H_element018  label="H_element : 010"  # scripted group (container) (typed FeaturePython)
  n = 10
  ref = H_element
FEATURE [App::DocumentObjectGroupPython] G4_BUTANE  # scripted group (container) (typed FeaturePython)
  Dunit = g/cm3
  Dvalue = 0.00249343
  Group = -> [C_element019,H_element018]
  conduct = 2
  density = 1
  expand = 3
  formula = G4_BUTANE
  name = G4_BUTANE
  specific = 4
FEATURE [App::DocumentObjectGroupPython] C_element020  label="C_element : 008"  # scripted group (container) (typed FeaturePython)
  n = 4
  ref = C_element
FEATURE [App::DocumentObjectGroupPython] H_element019  label="H_element : 011"  # scripted group (container) (typed FeaturePython)
  n = 10
  ref = H_element
FEATURE [App::DocumentObjectGroupPython] O_element018  label="O_element : 007"  # scripted group (container) (typed FeaturePython)
  n = 1
  ref = O_element
FEATURE [App::DocumentObjectGroupPython] G4_N_BUTYL_ALCOHOL  label="G4_N-BUTYL_ALCOHOL"  # scripted group (container) (typed FeaturePython)
  Dunit = g/cm3
  Dvalue = 0.8098
  Group = -> [C_element020,H_element019,O_element018]
  conduct = 2
  density = 1
  expand = 3
  formula = G4_N-BUTYL_ALCOHOL
  name = G4_N-BUTYL_ALCOHOL
  specific = 4
FEATURE [App::DocumentObjectGroupPython] H_element020  label="H_element : 0.025"  # scripted group (container) (typed FeaturePython)
  n = 0.02468
FEATURE [App::DocumentObjectGroupPython] C_element021  label="C_element : 0.502"  # scripted group (container) (typed FeaturePython)
  n = 0.501611
FEATURE [App::DocumentObjectGroupPython] O_element019  label="O_element : 0.005"  # scripted group (container) (typed FeaturePython)
  n = 0.004527
FEATURE [App::DocumentObjectGroupPython] F_element004  label="F_element : 0.465"  # scripted group (container) (typed FeaturePython)
  n = 0.465209
FEATURE [App::DocumentObjectGroupPython] Si_element001  label="Si_element : 0.004"  # scripted group (container) (typed FeaturePython)
  n = 0.003973
FEATURE [App::DocumentObjectGroupPython] G4_C_552  label="G4_C-552"  # scripted group (container) (typed FeaturePython)
  Dunit = g/cm3
  Dvalue = 1.76
  Group = -> [H_element020,C_element021,O_element019,F_element004,Si_element001]
  conduct = 2
  density = 1
  expand = 3
  formula = G4_C-552
  name = G4_C-552
  specific = 4
FEATURE [App::DocumentObjectGroupPython] Cd_element001  label="Cd_element : 1"  # scripted group (container) (typed FeaturePython)
  n = 1
  ref = Cd_element
FEATURE [App::DocumentObjectGroupPython] Te_element001  label="Te_element : 1"  # scripted group (container) (typed FeaturePython)
  n = 1
  ref = Te_element
FEATURE [App::DocumentObjectGroupPython] G4_CADMIUM_TELLURIDE  # scripted group (container) (typed FeaturePython)
  Dunit = g/cm3
  Dvalue = 6.2
  Group = -> [Cd_element001,Te_element001]
  conduct = 2
  density = 1
  expand = 3
  formula = G4_CADMIUM_TELLURIDE
  name = G4_CADMIUM_TELLURIDE
  specific = 4
FEATURE [App::DocumentObjectGroupPython] Cd_element002  label="Cd_element : 002"  # scripted group (container) (typed FeaturePython)
  n = 1
  ref = Cd_element
FEATURE [App::DocumentObjectGroupPython] W_element001  label="W_element : 1"  # scripted group (container) (typed FeaturePython)
  n = 1
  ref = W_element
FEATURE [App::DocumentObjectGroupPython] O_element020  label="O_element : 008"  # scripted group (container) (typed FeaturePython)
  n = 4
  ref = O_element
FEATURE [App::DocumentObjectGroupPython] G4_CADMIUM_TUNGSTATE  # scripted group (container) (typed FeaturePython)
  Dunit = g/cm3
  Dvalue = 7.9
  Group = -> [Cd_element002,W_element001,O_element020]
  conduct = 2
  density = 1
  expand = 3
  formula = G4_CADMIUM_TUNGSTATE
  name = G4_CADMIUM_TUNGSTATE
  specific = 4
FEATURE [App::DocumentObjectGroupPython] Ca_element005  label="Ca_element : 1"  # scripted group (container) (typed FeaturePython)
  n = 1
  ref = Ca_element
FEATURE [App::DocumentObjectGroupPython] C_element022  label="C_element : 009"  # scripted group (container) (typed FeaturePython)
  n = 1
  ref = C_element
FEATURE [App::DocumentObjectGroupPython] O_element021  label="O_element : 009"  # scripted group (container) (typed FeaturePython)
  n = 3
  ref = O_element
FEATURE [App::DocumentObjectGroupPython] G4_CALCIUM_CARBONATE  # scripted group (container) (typed FeaturePython)
  Dunit = g/cm3
  Dvalue = 2.8
  Group = -> [Ca_element005,C_element022,O_element021]
  conduct = 2
  density = 1
  expand = 3
  formula = G4_CALCIUM_CARBONATE
  name = G4_CALCIUM_CARBONATE
  specific = 4
FEATURE [App::DocumentObjectGroupPython] Ca_element006  label="Ca_element : 002"  # scripted group (container) (typed FeaturePython)
  n = 1
  ref = Ca_element
FEATURE [App::DocumentObjectGroupPython] F_element005  label="F_element : 003"  # scripted group (container) (typed FeaturePython)
  n = 2
  ref = F_element
FEATURE [App::DocumentObjectGroupPython] G4_CALCIUM_FLUORIDE  # scripted group (container) (typed FeaturePython)
  Dunit = g/cm3
  Dvalue = 3.18
  Group = -> [Ca_element006,F_element005]
  conduct = 2
  density = 1
  expand = 3
  formula = G4_CALCIUM_FLUORIDE
  name = G4_CALCIUM_FLUORIDE
  specific = 4
FEATURE [App::DocumentObjectGroupPython] Ca_element007  label="Ca_element : 003"  # scripted group (container) (typed FeaturePython)
  n = 1
  ref = Ca_element
FEATURE [App::DocumentObjectGroupPython] O_element022  label="O_element : 010"  # scripted group (container) (typed FeaturePython)
  n = 1
  ref = O_element
FEATURE [App::DocumentObjectGroupPython] G4_CALCIUM_OXIDE  # scripted group (container) (typed FeaturePython)
  Dunit = g/cm3
  Dvalue = 3.3
  Group = -> [Ca_element007,O_element022]
  conduct = 2
  density = 1
  expand = 3
  formula = G4_CALCIUM_OXIDE
  name = G4_CALCIUM_OXIDE
  specific = 4
FEATURE [App::DocumentObjectGroupPython] Ca_element008  label="Ca_element : 004"  # scripted group (container) (typed FeaturePython)
  n = 1
  ref = Ca_element
FEATURE [App::DocumentObjectGroupPython] S_element007  label="S_element : 002"  # scripted group (container) (typed FeaturePython)
  n = 1
  ref = S_element
FEATURE [App::DocumentObjectGroupPython] O_element023  label="O_element : 011"  # scripted group (container) (typed FeaturePython)
  n = 4
  ref = O_element
FEATURE [App::DocumentObjectGroupPython] G4_CALCIUM_SULFATE  # scripted group (container) (typed FeaturePython)
  Dunit = g/cm3
  Dvalue = 2.96
  Group = -> [Ca_element008,S_element007,O_element023]
  conduct = 2
  density = 1
  expand = 3
  formula = G4_CALCIUM_SULFATE
  name = G4_CALCIUM_SULFATE
  specific = 4
FEATURE [App::DocumentObjectGroupPython] Ca_element009  label="Ca_element : 005"  # scripted group (container) (typed FeaturePython)
  n = 1
  ref = Ca_element
FEATURE [App::DocumentObjectGroupPython] W_element002  label="W_element : 002"  # scripted group (container) (typed FeaturePython)
  n = 1
  ref = W_element
FEATURE [App::DocumentObjectGroupPython] O_element024  label="O_element : 012"  # scripted group (container) (typed FeaturePython)
  n = 4
  ref = O_element
FEATURE [App::DocumentObjectGroupPython] G4_CALCIUM_TUNGSTATE  # scripted group (container) (typed FeaturePython)
  Dunit = g/cm3
  Dvalue = 6.062
  Group = -> [Ca_element009,W_element002,O_element024]
  conduct = 2
  density = 1
  expand = 3
  formula = G4_CALCIUM_TUNGSTATE
  name = G4_CALCIUM_TUNGSTATE
  specific = 4
FEATURE [App::DocumentObjectGroupPython] C_element023  label="C_element : 010"  # scripted group (container) (typed FeaturePython)
  n = 1
  ref = C_element
FEATURE [App::DocumentObjectGroupPython] O_element025  label="O_element : 013"  # scripted group (container) (typed FeaturePython)
  n = 2
  ref = O_element
FEATURE [App::DocumentObjectGroupPython] G4_CARBON_DIOXIDE  # scripted group (container) (typed FeaturePython)
  Dunit = g/cm3
  Dvalue = 0.00184212
  Group = -> [C_element023,O_element025]
  conduct = 2
  density = 1
  expand = 3
  formula = G4_CARBON_DIOXIDE
  name = G4_CARBON_DIOXIDE
  specific = 4
FEATURE [App::DocumentObjectGroupPython] C_element024  label="C_element : 011"  # scripted group (container) (typed FeaturePython)
  n = 1
  ref = C_element
FEATURE [App::DocumentObjectGroupPython] Cl_element004  label="Cl_element : 4"  # scripted group (container) (typed FeaturePython)
  n = 4
  ref = Cl_element
FEATURE [App::DocumentObjectGroupPython] G4_CARBON_TETRACHLORIDE  # scripted group (container) (typed FeaturePython)
  Dunit = g/cm3
  Dvalue = 1.594
  Group = -> [C_element024,Cl_element004]
  conduct = 2
  density = 1
  expand = 3
  formula = G4_CARBON_TETRACHLORIDE
  name = G4_CARBON_TETRACHLORIDE
  specific = 4
FEATURE [App::DocumentObjectGroupPython] C_element025  label="C_element : 012"  # scripted group (container) (typed FeaturePython)
  n = 6
  ref = C_element
FEATURE [App::DocumentObjectGroupPython] H_element021  label="H_element : 012"  # scripted group (container) (typed FeaturePython)
  n = 10
  ref = H_element
FEATURE [App::DocumentObjectGroupPython] O_element026  label="O_element : 5"  # scripted group (container) (typed FeaturePython)
  n = 5
  ref = O_element
FEATURE [App::DocumentObjectGroupPython] G4_CELLULOSE_CELLOPHANE  # scripted group (container) (typed FeaturePython)
  Dunit = g/cm3
  Dvalue = 1.42
  Group = -> [C_element025,H_element021,O_element026]
  conduct = 2
  density = 1
  expand = 3
  formula = G4_CELLULOSE_CELLOPHANE
  name = G4_CELLULOSE_CELLOPHANE
  specific = 4
FEATURE [App::DocumentObjectGroupPython] H_element022  label="H_element : 0.067"  # scripted group (container) (typed FeaturePython)
  n = 0.067125
FEATURE [App::DocumentObjectGroupPython] C_element026  label="C_element : 0.545"  # scripted group (container) (typed FeaturePython)
  n = 0.545403
FEATURE [App::DocumentObjectGroupPython] O_element027  label="O_element : 0.387"  # scripted group (container) (typed FeaturePython)
  n = 0.387472
FEATURE [App::DocumentObjectGroupPython] G4_CELLULOSE_BUTYRATE  # scripted group (container) (typed FeaturePython)
  Dunit = g/cm3
  Dvalue = 1.2
  Group = -> [H_element022,C_element026,O_element027]
  conduct = 2
  density = 1
  expand = 3
  formula = G4_CELLULOSE_BUTYRATE
  name = G4_CELLULOSE_BUTYRATE
  specific = 4
FEATURE [App::DocumentObjectGroupPython] H_element023  label="H_element : 0.029"  # scripted group (container) (typed FeaturePython)
  n = 0.029216
FEATURE [App::DocumentObjectGroupPython] C_element027  label="C_element : 0.271"  # scripted group (container) (typed FeaturePython)
  n = 0.271296
FEATURE [App::DocumentObjectGroupPython] N_element013  label="N_element : 0.121"  # scripted group (container) (typed FeaturePython)
  n = 0.121276
FEATURE [App::DocumentObjectGroupPython] O_element028  label="O_element : 0.578"  # scripted group (container) (typed FeaturePython)
  n = 0.578212
FEATURE [App::DocumentObjectGroupPython] G4_CELLULOSE_NITRATE  # scripted group (container) (typed FeaturePython)
  Dunit = g/cm3
  Dvalue = 1.49
  Group = -> [H_element023,C_element027,N_element013,O_element028]
  conduct = 2
  density = 1
  expand = 3
  formula = G4_CELLULOSE_NITRATE
  name = G4_CELLULOSE_NITRATE
  specific = 4
FEATURE [App::DocumentObjectGroupPython] H_element024  label="H_element : 0.108"  # scripted group (container) (typed FeaturePython)
  n = 0.107596
FEATURE [App::DocumentObjectGroupPython] N_element014  label="N_element : 0.001"  # scripted group (container) (typed FeaturePython)
  n = 0.0008
FEATURE [App::DocumentObjectGroupPython] O_element029  label="O_element : 0.875"  # scripted group (container) (typed FeaturePython)
  n = 0.874976
FEATURE [App::DocumentObjectGroupPython] S_element008  label="S_element : 0.015"  # scripted group (container) (typed FeaturePython)
  n = 0.014627
FEATURE [App::DocumentObjectGroupPython] Ce_element001  label="Ce_element : 0.002"  # scripted group (container) (typed FeaturePython)
  n = 0.002001
FEATURE [App::DocumentObjectGroupPython] G4_CERIC_SULFATE  # scripted group (container) (typed FeaturePython)
  Dunit = g/cm3
  Dvalue = 1.03
  Group = -> [H_element024,N_element014,O_element029,S_element008,Ce_element001]
  conduct = 2
  density = 1
  expand = 3
  formula = G4_CERIC_SULFATE
  name = G4_CERIC_SULFATE
  specific = 4
FEATURE [App::DocumentObjectGroupPython] Cs_element001  label="Cs_element : 1"  # scripted group (container) (typed FeaturePython)
  n = 1
  ref = Cs_element
FEATURE [App::DocumentObjectGroupPython] F_element006  label="F_element : 1"  # scripted group (container) (typed FeaturePython)
  n = 1
  ref = F_element
FEATURE [App::DocumentObjectGroupPython] G4_CESIUM_FLUORIDE  # scripted group (container) (typed FeaturePython)
  Dunit = g/cm3
  Dvalue = 4.115
  Group = -> [Cs_element001,F_element006]
  conduct = 2
  density = 1
  expand = 3
  formula = G4_CESIUM_FLUORIDE
  name = G4_CESIUM_FLUORIDE
  specific = 4
FEATURE [App::DocumentObjectGroupPython] Cs_element002  label="Cs_element : 002"  # scripted group (container) (typed FeaturePython)
  n = 1
  ref = Cs_element
FEATURE [App::DocumentObjectGroupPython] I_element001  label="I_element : 1"  # scripted group (container) (typed FeaturePython)
  n = 1
  ref = I_element
FEATURE [App::DocumentObjectGroupPython] G4_CESIUM_IODIDE  # scripted group (container) (typed FeaturePython)
  Dunit = g/cm3
  Dvalue = 4.51
  Group = -> [Cs_element002,I_element001]
  conduct = 2
  density = 1
  expand = 3
  formula = G4_CESIUM_IODIDE
  name = G4_CESIUM_IODIDE
  specific = 4
FEATURE [App::DocumentObjectGroupPython] C_element028  label="C_element : 013"  # scripted group (container) (typed FeaturePython)
  n = 6
  ref = C_element
FEATURE [App::DocumentObjectGroupPython] H_element025  label="H_element : 013"  # scripted group (container) (typed FeaturePython)
  n = 5
  ref = H_element
FEATURE [App::DocumentObjectGroupPython] Cl_element005  label="Cl_element : 1"  # scripted group (container) (typed FeaturePython)
  n = 1
  ref = Cl_element
FEATURE [App::DocumentObjectGroupPython] G4_CHLOROBENZENE  # scripted group (container) (typed FeaturePython)
  Dunit = g/cm3
  Dvalue = 1.1058
  Group = -> [C_element028,H_element025,Cl_element005]
  conduct = 2
  density = 1
  expand = 3
  formula = G4_CHLOROBENZENE
  name = G4_CHLOROBENZENE
  specific = 4
FEATURE [App::DocumentObjectGroupPython] C_element029  label="C_element : 014"  # scripted group (container) (typed FeaturePython)
  n = 1
  ref = C_element
FEATURE [App::DocumentObjectGroupPython] H_element026  label="H_element : 1"  # scripted group (container) (typed FeaturePython)
  n = 1
  ref = H_element
FEATURE [App::DocumentObjectGroupPython] Cl_element006  label="Cl_element : 3"  # scripted group (container) (typed FeaturePython)
  n = 3
  ref = Cl_element
FEATURE [App::DocumentObjectGroupPython] G4_CHLOROFORM  # scripted group (container) (typed FeaturePython)
  Dunit = g/cm3
  Dvalue = 1.4832
  Group = -> [C_element029,H_element026,Cl_element006]
  conduct = 2
  density = 1
  expand = 3
  formula = G4_CHLOROFORM
  name = G4_CHLOROFORM
  specific = 4
FEATURE [App::DocumentObjectGroupPython] H_element027  label="H_element : 0.010"  # scripted group (container) (typed FeaturePython)
  n = 0.01
FEATURE [App::DocumentObjectGroupPython] C_element030  label="C_element : 0.001"  # scripted group (container) (typed FeaturePython)
  n = 0.001
FEATURE [App::DocumentObjectGroupPython] O_element030  label="O_element : 0.529"  # scripted group (container) (typed FeaturePython)
  n = 0.529107
FEATURE [App::DocumentObjectGroupPython] Na_element005  label="Na_element : 0.016"  # scripted group (container) (typed FeaturePython)
  n = 0.016
FEATURE [App::DocumentObjectGroupPython] Mg_element003  label="Mg_element : 0.004"  # scripted group (container) (typed FeaturePython)
  n = 0.002
FEATURE [App::DocumentObjectGroupPython] Al_element002  label="Al_element : 0.034"  # scripted group (container) (typed FeaturePython)
  n = 0.033872
FEATURE [App::DocumentObjectGroupPython] Si_element002  label="Si_element : 0.337"  # scripted group (container) (typed FeaturePython)
  n = 0.337021
FEATURE [App::DocumentObjectGroupPython] K_element003  label="K_element : 0.013"  # scripted group (container) (typed FeaturePython)
  n = 0.013
FEATURE [App::DocumentObjectGroupPython] Ca_element010  label="Ca_element : 0.044"  # scripted group (container) (typed FeaturePython)
  n = 0.044
FEATURE [App::DocumentObjectGroupPython] Fe_element002  label="Fe_element : 0.014"  # scripted group (container) (typed FeaturePython)
  n = 0.014
FEATURE [App::DocumentObjectGroupPython] G4_CONCRETE  # scripted group (container) (typed FeaturePython)
  Dunit = g/cm3
  Dvalue = 2.3
  Group = -> [H_element027,C_element030,O_element030,Na_element005,Mg_element003,Al_element002,Si_element002,K_element003,Ca_element010,Fe_element002]
  conduct = 2
  density = 1
  expand = 3
  formula = G4_CONCRETE
  name = G4_CONCRETE
  specific = 4
FEATURE [App::DocumentObjectGroupPython] C_element031  label="C_element : 015"  # scripted group (container) (typed FeaturePython)
  n = 6
  ref = C_element
FEATURE [App::DocumentObjectGroupPython] H_element028  label="H_element : 12"  # scripted group (container) (typed FeaturePython)
  n = 12
  ref = H_element
FEATURE [App::DocumentObjectGroupPython] G4_CYCLOHEXANE  # scripted group (container) (typed FeaturePython)
  Dunit = g/cm3
  Dvalue = 0.779
  Group = -> [C_element031,H_element028]
  conduct = 2
  density = 1
  expand = 3
  formula = G4_CYCLOHEXANE
  name = G4_CYCLOHEXANE
  specific = 4
FEATURE [App::DocumentObjectGroupPython] C_element032  label="C_element : 016"  # scripted group (container) (typed FeaturePython)
  n = 6
  ref = C_element
FEATURE [App::DocumentObjectGroupPython] H_element029  label="H_element : 4"  # scripted group (container) (typed FeaturePython)
  n = 4
  ref = H_element
FEATURE [App::DocumentObjectGroupPython] Cl_element007  label="Cl_element : 2"  # scripted group (container) (typed FeaturePython)
  n = 2
  ref = Cl_element
FEATURE [App::DocumentObjectGroupPython] G4_1_2_DICHLOROBENZENE  label="G4_1.2-DICHLOROBENZENE"  # scripted group (container) (typed FeaturePython)
  Dunit = g/cm3
  Dvalue = 1.3048
  Group = -> [C_element032,H_element029,Cl_element007]
  conduct = 2
  density = 1
  expand = 3
  formula = G4_1.2-DICHLOROBENZENE
  name = G4_1.2-DICHLOROBENZENE
  specific = 4
FEATURE [App::DocumentObjectGroupPython] C_element033  label="C_element : 017"  # scripted group (container) (typed FeaturePython)
  n = 4
  ref = C_element
FEATURE [App::DocumentObjectGroupPython] H_element030  label="H_element : 8"  # scripted group (container) (typed FeaturePython)
  n = 8
  ref = H_element
FEATURE [App::DocumentObjectGroupPython] O_element031  label="O_element : 014"  # scripted group (container) (typed FeaturePython)
  n = 1
  ref = O_element
FEATURE [App::DocumentObjectGroupPython] Cl_element008  label="Cl_element : 005"  # scripted group (container) (typed FeaturePython)
  n = 2
  ref = Cl_element
FEATURE [App::DocumentObjectGroupPython] G4_DICHLORODIETHYL_ETHER  # scripted group (container) (typed FeaturePython)
  Dunit = g/cm3
  Dvalue = 1.2199
  Group = -> [C_element033,H_element030,O_element031,Cl_element008]
  conduct = 2
  density = 1
  expand = 3
  formula = G4_DICHLORODIETHYL_ETHER
  name = G4_DICHLORODIETHYL_ETHER
  specific = 4
FEATURE [App::DocumentObjectGroupPython] C_element034  label="C_element : 018"  # scripted group (container) (typed FeaturePython)
  n = 2
  ref = C_element
FEATURE [App::DocumentObjectGroupPython] H_element031  label="H_element : 014"  # scripted group (container) (typed FeaturePython)
  n = 4
  ref = H_element
FEATURE [App::DocumentObjectGroupPython] Cl_element009  label="Cl_element : 006"  # scripted group (container) (typed FeaturePython)
  n = 2
  ref = Cl_element
FEATURE [App::DocumentObjectGroupPython] G4_1_2_DICHLOROETHANE  label="G4_1.2-DICHLOROETHANE"  # scripted group (container) (typed FeaturePython)
  Dunit = g/cm3
  Dvalue = 1.2351
  Group = -> [C_element034,H_element031,Cl_element009]
  conduct = 2
  density = 1
  expand = 3
  formula = G4_1.2-DICHLOROETHANE
  name = G4_1.2-DICHLOROETHANE
  specific = 4
FEATURE [App::DocumentObjectGroupPython] C_element035  label="C_element : 019"  # scripted group (container) (typed FeaturePython)
  n = 4
  ref = C_element
FEATURE [App::DocumentObjectGroupPython] H_element032  label="H_element : 015"  # scripted group (container) (typed FeaturePython)
  n = 10
  ref = H_element
FEATURE [App::DocumentObjectGroupPython] O_element032  label="O_element : 015"  # scripted group (container) (typed FeaturePython)
  n = 1
  ref = O_element
FEATURE [App::DocumentObjectGroupPython] G4_DIETHYL_ETHER  # scripted group (container) (typed FeaturePython)
  Dunit = g/cm3
  Dvalue = 0.71378
  Group = -> [C_element035,H_element032,O_element032]
  conduct = 2
  density = 1
  expand = 3
  formula = G4_DIETHYL_ETHER
  name = G4_DIETHYL_ETHER
  specific = 4
FEATURE [App::DocumentObjectGroupPython] C_element036  label="C_element : 020"  # scripted group (container) (typed FeaturePython)
  n = 3
  ref = C_element
FEATURE [App::DocumentObjectGroupPython] H_element033  label="H_element : 016"  # scripted group (container) (typed FeaturePython)
  n = 7
  ref = H_element
FEATURE [App::DocumentObjectGroupPython] N_element015  label="N_element : 008"  # scripted group (container) (typed FeaturePython)
  n = 1
  ref = N_element
FEATURE [App::DocumentObjectGroupPython] O_element033  label="O_element : 016"  # scripted group (container) (typed FeaturePython)
  n = 1
  ref = O_element
FEATURE [App::DocumentObjectGroupPython] G4_N_N_DIMETHYL_FORMAMIDE  label="G4_N.N-DIMETHYL_FORMAMIDE"  # scripted group (container) (typed FeaturePython)
  Dunit = g/cm3
  Dvalue = 0.9487
  Group = -> [C_element036,H_element033,N_element015,O_element033]
  conduct = 2
  density = 1
  expand = 3
  formula = G4_N.N-DIMETHYL_FORMAMIDE
  name = G4_N.N-DIMETHYL_FORMAMIDE
  specific = 4
FEATURE [App::DocumentObjectGroupPython] C_element037  label="C_element : 021"  # scripted group (container) (typed FeaturePython)
  n = 2
  ref = C_element
FEATURE [App::DocumentObjectGroupPython] H_element034  label="H_element : 017"  # scripted group (container) (typed FeaturePython)
  n = 6
  ref = H_element
FEATURE [App::DocumentObjectGroupPython] O_element034  label="O_element : 017"  # scripted group (container) (typed FeaturePython)
  n = 1
  ref = O_element
FEATURE [App::DocumentObjectGroupPython] S_element009  label="S_element : 003"  # scripted group (container) (typed FeaturePython)
  n = 1
  ref = S_element
FEATURE [App::DocumentObjectGroupPython] G4_DIMETHYL_SULFOXIDE  # scripted group (container) (typed FeaturePython)
  Dunit = g/cm3
  Dvalue = 1.1014
  Group = -> [C_element037,H_element034,O_element034,S_element009]
  conduct = 2
  density = 1
  expand = 3
  formula = G4_DIMETHYL_SULFOXIDE
  name = G4_DIMETHYL_SULFOXIDE
  specific = 4
FEATURE [App::DocumentObjectGroupPython] C_element038  label="C_element : 022"  # scripted group (container) (typed FeaturePython)
  n = 2
  ref = C_element
FEATURE [App::DocumentObjectGroupPython] H_element035  label="H_element : 018"  # scripted group (container) (typed FeaturePython)
  n = 6
  ref = H_element
FEATURE [App::DocumentObjectGroupPython] G4_ETHANE  # scripted group (container) (typed FeaturePython)
  Dunit = g/cm3
  Dvalue = 0.00125324
  Group = -> [C_element038,H_element035]
  conduct = 2
  density = 1
  expand = 3
  formula = G4_ETHANE
  name = G4_ETHANE
  specific = 4
FEATURE [App::DocumentObjectGroupPython] C_element039  label="C_element : 023"  # scripted group (container) (typed FeaturePython)
  n = 2
  ref = C_element
FEATURE [App::DocumentObjectGroupPython] H_element036  label="H_element : 019"  # scripted group (container) (typed FeaturePython)
  n = 6
  ref = H_element
FEATURE [App::DocumentObjectGroupPython] O_element035  label="O_element : 018"  # scripted group (container) (typed FeaturePython)
  n = 1
  ref = O_element
FEATURE [App::DocumentObjectGroupPython] G4_ETHYL_ALCOHOL  # scripted group (container) (typed FeaturePython)
  Dunit = g/cm3
  Dvalue = 0.7893
  Group = -> [C_element039,H_element036,O_element035]
  conduct = 2
  density = 1
  expand = 3
  formula = G4_ETHYL_ALCOHOL
  name = G4_ETHYL_ALCOHOL
  specific = 4
FEATURE [App::DocumentObjectGroupPython] H_element037  label="H_element : 0.090"  # scripted group (container) (typed FeaturePython)
  n = 0.090027
FEATURE [App::DocumentObjectGroupPython] C_element040  label="C_element : 0.585"  # scripted group (container) (typed FeaturePython)
  n = 0.585182
FEATURE [App::DocumentObjectGroupPython] O_element036  label="O_element : 0.325"  # scripted group (container) (typed FeaturePython)
  n = 0.324791
FEATURE [App::DocumentObjectGroupPython] G4_ETHYL_CELLULOSE  # scripted group (container) (typed FeaturePython)
  Dunit = g/cm3
  Dvalue = 1.13
  Group = -> [H_element037,C_element040,O_element036]
  conduct = 2
  density = 1
  expand = 3
  formula = G4_ETHYL_CELLULOSE
  name = G4_ETHYL_CELLULOSE
  specific = 4
FEATURE [App::DocumentObjectGroupPython] C_element041  label="C_element : 024"  # scripted group (container) (typed FeaturePython)
  n = 2
  ref = C_element
FEATURE [App::DocumentObjectGroupPython] H_element038  label="H_element : 020"  # scripted group (container) (typed FeaturePython)
  n = 4
  ref = H_element
FEATURE [App::DocumentObjectGroupPython] G4_ETHYLENE  # scripted group (container) (typed FeaturePython)
  Dunit = g/cm3
  Dvalue = 0.00117497
  Group = -> [C_element041,H_element038]
  conduct = 2
  density = 1
  expand = 3
  formula = G4_ETHYLENE
  name = G4_ETHYLENE
  specific = 4
FEATURE [App::DocumentObjectGroupPython] H_element039  label="H_element : 0.096"  # scripted group (container) (typed FeaturePython)
  n = 0.096
FEATURE [App::DocumentObjectGroupPython] C_element042  label="C_element : 0.195"  # scripted group (container) (typed FeaturePython)
  n = 0.195
FEATURE [App::DocumentObjectGroupPython] N_element016  label="N_element : 0.057"  # scripted group (container) (typed FeaturePython)
  n = 0.057
FEATURE [App::DocumentObjectGroupPython] O_element037  label="O_element : 0.646"  # scripted group (container) (typed FeaturePython)
  n = 0.646
FEATURE [App::DocumentObjectGroupPython] Na_element006  label="Na_element : 0.017"  # scripted group (container) (typed FeaturePython)
  n = 0.001
FEATURE [App::DocumentObjectGroupPython] P_element005  label="P_element : 0.104"  # scripted group (container) (typed FeaturePython)
  n = 0.001
FEATURE [App::DocumentObjectGroupPython] S_element010  label="S_element : 0.016"  # scripted group (container) (typed FeaturePython)
  n = 0.003
FEATURE [App::DocumentObjectGroupPython] Cl_element010  label="Cl_element : 0.005"  # scripted group (container) (typed FeaturePython)
  n = 0.001
FEATURE [App::DocumentObjectGroupPython] G4_EYE_LENS_ICRP  # scripted group (container) (typed FeaturePython)
  Dunit = g/cm3
  Dvalue = 1.07
  Group = -> [H_element039,C_element042,N_element016,O_element037,Na_element006,P_element005,S_element010,Cl_element010]
  conduct = 2
  density = 1
  expand = 3
  formula = G4_EYE_LENS_ICRP
  name = G4_EYE_LENS_ICRP
  specific = 4
FEATURE [App::DocumentObjectGroupPython] Fe_element003  label="Fe_element : 2"  # scripted group (container) (typed FeaturePython)
  n = 2
  ref = Fe_element
FEATURE [App::DocumentObjectGroupPython] O_element038  label="O_element : 019"  # scripted group (container) (typed FeaturePython)
  n = 3
  ref = O_element
FEATURE [App::DocumentObjectGroupPython] G4_FERRIC_OXIDE  # scripted group (container) (typed FeaturePython)
  Dunit = g/cm3
  Dvalue = 5.2
  Group = -> [Fe_element003,O_element038]
  conduct = 2
  density = 1
  expand = 3
  formula = G4_FERRIC_OXIDE
  name = G4_FERRIC_OXIDE
  specific = 4
FEATURE [App::DocumentObjectGroupPython] Fe_element004  label="Fe_element : 1"  # scripted group (container) (typed FeaturePython)
  n = 1
  ref = Fe_element
FEATURE [App::DocumentObjectGroupPython] B_element003  label="B_element : 1"  # scripted group (container) (typed FeaturePython)
  n = 1
  ref = B_element
FEATURE [App::DocumentObjectGroupPython] G4_FERROBORIDE  # scripted group (container) (typed FeaturePython)
  Dunit = g/cm3
  Dvalue = 7.15
  Group = -> [Fe_element004,B_element003]
  conduct = 2
  density = 1
  expand = 3
  formula = G4_FERROBORIDE
  name = G4_FERROBORIDE
  specific = 4
FEATURE [App::DocumentObjectGroupPython] Fe_element005  label="Fe_element : 003"  # scripted group (container) (typed FeaturePython)
  n = 1
  ref = Fe_element
FEATURE [App::DocumentObjectGroupPython] O_element039  label="O_element : 020"  # scripted group (container) (typed FeaturePython)
  n = 1
  ref = O_element
FEATURE [App::DocumentObjectGroupPython] G4_FERROUS_OXIDE  # scripted group (container) (typed FeaturePython)
  Dunit = g/cm3
  Dvalue = 5.7
  Group = -> [Fe_element005,O_element039]
  conduct = 2
  density = 1
  expand = 3
  formula = G4_FERROUS_OXIDE
  name = G4_FERROUS_OXIDE
  specific = 4
FEATURE [App::DocumentObjectGroupPython] H_element040  label="H_element : 0.115"  # scripted group (container) (typed FeaturePython)
  n = 0.108259
FEATURE [App::DocumentObjectGroupPython] N_element017  label="N_element : 0.000"  # scripted group (container) (typed FeaturePython)
  n = 2.7e-05
FEATURE [App::DocumentObjectGroupPython] O_element040  label="O_element : 0.879"  # scripted group (container) (typed FeaturePython)
  n = 0.878636
FEATURE [App::DocumentObjectGroupPython] Na_element007  label="Na_element : 0.000"  # scripted group (container) (typed FeaturePython)
  n = 2.2e-05
FEATURE [App::DocumentObjectGroupPython] S_element011  label="S_element : 0.013"  # scripted group (container) (typed FeaturePython)
  n = 0.012968
FEATURE [App::DocumentObjectGroupPython] Cl_element011  label="Cl_element : 0.000"  # scripted group (container) (typed FeaturePython)
  n = 3.4e-05
FEATURE [App::DocumentObjectGroupPython] Fe_element006  label="Fe_element : 0.000"  # scripted group (container) (typed FeaturePython)
  n = 5.4e-05
FEATURE [App::DocumentObjectGroupPython] G4_FERROUS_SULFATE  # scripted group (container) (typed FeaturePython)
  Dunit = g/cm3
  Dvalue = 1.024
  Group = -> [H_element040,N_element017,O_element040,Na_element007,S_element011,Cl_element011,Fe_element006]
  conduct = 2
  density = 1
  expand = 3
  formula = G4_FERROUS_SULFATE
  name = G4_FERROUS_SULFATE
  specific = 4
FEATURE [App::DocumentObjectGroupPython] C_element043  label="C_element : 0.099"  # scripted group (container) (typed FeaturePython)
  n = 0.099335
FEATURE [App::DocumentObjectGroupPython] F_element007  label="F_element : 0.314"  # scripted group (container) (typed FeaturePython)
  n = 0.314247
FEATURE [App::DocumentObjectGroupPython] Cl_element012  label="Cl_element : 0.586"  # scripted group (container) (typed FeaturePython)
  n = 0.586418
FEATURE [App::DocumentObjectGroupPython] G4_FREON_12  label="G4_FREON-12"  # scripted group (container) (typed FeaturePython)
  Dunit = g/cm3
  Dvalue = 1.12
  Group = -> [C_element043,F_element007,Cl_element012]
  conduct = 2
  density = 1
  expand = 3
  formula = G4_FREON-12
  name = G4_FREON-12
  specific = 4
FEATURE [App::DocumentObjectGroupPython] C_element044  label="C_element : 0.057"  # scripted group (container) (typed FeaturePython)
  n = 0.057245
FEATURE [App::DocumentObjectGroupPython] F_element008  label="F_element : 0.181"  # scripted group (container) (typed FeaturePython)
  n = 0.181096
FEATURE [App::DocumentObjectGroupPython] Br_element001  label="Br_element : 0.762"  # scripted group (container) (typed FeaturePython)
  n = 0.761659
FEATURE [App::DocumentObjectGroupPython] G4_FREON_12B2  label="G4_FREON-12B2"  # scripted group (container) (typed FeaturePython)
  Dunit = g/cm3
  Dvalue = 1.8
  Group = -> [C_element044,F_element008,Br_element001]
  conduct = 2
  density = 1
  expand = 3
  formula = G4_FREON-12B2
  name = G4_FREON-12B2
  specific = 4
FEATURE [App::DocumentObjectGroupPython] C_element045  label="C_element : 0.115"  # scripted group (container) (typed FeaturePython)
  n = 0.114983
FEATURE [App::DocumentObjectGroupPython] F_element009  label="F_element : 0.546"  # scripted group (container) (typed FeaturePython)
  n = 0.545621
FEATURE [App::DocumentObjectGroupPython] Cl_element013  label="Cl_element : 0.339"  # scripted group (container) (typed FeaturePython)
  n = 0.339396
FEATURE [App::DocumentObjectGroupPython] G4_FREON_13  label="G4_FREON-13"  # scripted group (container) (typed FeaturePython)
  Dunit = g/cm3
  Dvalue = 0.95
  Group = -> [C_element045,F_element009,Cl_element013]
  conduct = 2
  density = 1
  expand = 3
  formula = G4_FREON-13
  name = G4_FREON-13
  specific = 4
FEATURE [App::DocumentObjectGroupPython] C_element046  label="C_element : 025"  # scripted group (container) (typed FeaturePython)
  n = 1
  ref = C_element
FEATURE [App::DocumentObjectGroupPython] F_element010  label="F_element : 3"  # scripted group (container) (typed FeaturePython)
  n = 3
  ref = F_element
FEATURE [App::DocumentObjectGroupPython] Br_element002  label="Br_element : 1"  # scripted group (container) (typed FeaturePython)
  n = 1
  ref = Br_element
FEATURE [App::DocumentObjectGroupPython] G4_FREON_13B1  label="G4_FREON-13B1"  # scripted group (container) (typed FeaturePython)
  Dunit = g/cm3
  Dvalue = 1.5
  Group = -> [C_element046,F_element010,Br_element002]
  conduct = 2
  density = 1
  expand = 3
  formula = G4_FREON-13B1
  name = G4_FREON-13B1
  specific = 4
FEATURE [App::DocumentObjectGroupPython] C_element047  label="C_element : 0.061"  # scripted group (container) (typed FeaturePython)
  n = 0.061309
FEATURE [App::DocumentObjectGroupPython] F_element011  label="F_element : 0.291"  # scripted group (container) (typed FeaturePython)
  n = 0.290924
FEATURE [App::DocumentObjectGroupPython] I_element002  label="I_element : 0.648"  # scripted group (container) (typed FeaturePython)
  n = 0.647767
FEATURE [App::DocumentObjectGroupPython] G4_FREON_13I1  label="G4_FREON-13I1"  # scripted group (container) (typed FeaturePython)
  Dunit = g/cm3
  Dvalue = 1.8
  Group = -> [C_element047,F_element011,I_element002]
  conduct = 2
  density = 1
  expand = 3
  formula = G4_FREON-13I1
  name = G4_FREON-13I1
  specific = 4
FEATURE [App::DocumentObjectGroupPython] Gd_element001  label="Gd_element : 2"  # scripted group (container) (typed FeaturePython)
  n = 2
  ref = Gd_element
FEATURE [App::DocumentObjectGroupPython] O_element041  label="O_element : 021"  # scripted group (container) (typed FeaturePython)
  n = 2
  ref = O_element
FEATURE [App::DocumentObjectGroupPython] S_element012  label="S_element : 004"  # scripted group (container) (typed FeaturePython)
  n = 1
  ref = S_element
FEATURE [App::DocumentObjectGroupPython] G4_GADOLINIUM_OXYSULFIDE  # scripted group (container) (typed FeaturePython)
  Dunit = g/cm3
  Dvalue = 7.44
  Group = -> [Gd_element001,O_element041,S_element012]
  conduct = 2
  density = 1
  expand = 3
  formula = G4_GADOLINIUM_OXYSULFIDE
  name = G4_GADOLINIUM_OXYSULFIDE
  specific = 4
FEATURE [App::DocumentObjectGroupPython] Ga_element001  label="Ga_element : 1"  # scripted group (container) (typed FeaturePython)
  n = 1
  ref = Ga_element
FEATURE [App::DocumentObjectGroupPython] As_element001  label="As_element : 1"  # scripted group (container) (typed FeaturePython)
  n = 1
  ref = As_element
FEATURE [App::DocumentObjectGroupPython] G4_GALLIUM_ARSENIDE  # scripted group (container) (typed FeaturePython)
  Dunit = g/cm3
  Dvalue = 5.31
  Group = -> [Ga_element001,As_element001]
  conduct = 2
  density = 1
  expand = 3
  formula = G4_GALLIUM_ARSENIDE
  name = G4_GALLIUM_ARSENIDE
  specific = 4
FEATURE [App::DocumentObjectGroupPython] H_element041  label="H_element : 0.081"  # scripted group (container) (typed FeaturePython)
  n = 0.08118
FEATURE [App::DocumentObjectGroupPython] C_element048  label="C_element : 0.416"  # scripted group (container) (typed FeaturePython)
  n = 0.41606
FEATURE [App::DocumentObjectGroupPython] N_element018  label="N_element : 0.111"  # scripted group (container) (typed FeaturePython)
  n = 0.11124
FEATURE [App::DocumentObjectGroupPython] O_element042  label="O_element : 0.381"  # scripted group (container) (typed FeaturePython)
  n = 0.38064
FEATURE [App::DocumentObjectGroupPython] S_element013  label="S_element : 0.011"  # scripted group (container) (typed FeaturePython)
  n = 0.01088
FEATURE [App::DocumentObjectGroupPython] G4_GEL_PHOTO_EMULSION  # scripted group (container) (typed FeaturePython)
  Dunit = g/cm3
  Dvalue = 1.2914
  Group = -> [H_element041,C_element048,N_element018,O_element042,S_element013]
  conduct = 2
  density = 1
  expand = 3
  formula = G4_GEL_PHOTO_EMULSION
  name = G4_GEL_PHOTO_EMULSION
  specific = 4
FEATURE [App::DocumentObjectGroupPython] B_element004  label="B_element : 0.040"  # scripted group (container) (typed FeaturePython)
  n = 0.0400639
FEATURE [App::DocumentObjectGroupPython] O_element043  label="O_element : 0.540"  # scripted group (container) (typed FeaturePython)
  n = 0.539561
FEATURE [App::DocumentObjectGroupPython] Na_element008  label="Na_element : 0.028"  # scripted group (container) (typed FeaturePython)
  n = 0.0281909
FEATURE [App::DocumentObjectGroupPython] Al_element003  label="Al_element : 0.012"  # scripted group (container) (typed FeaturePython)
  n = 0.011644
FEATURE [App::DocumentObjectGroupPython] Si_element003  label="Si_element : 0.377"  # scripted group (container) (typed FeaturePython)
  n = 0.377219
FEATURE [App::DocumentObjectGroupPython] K_element004  label="K_element : 0.014"  # scripted group (container) (typed FeaturePython)
  n = 0.00332099
FEATURE [App::DocumentObjectGroupPython] G4_Pyrex_Glass  # scripted group (container) (typed FeaturePython)
  Dunit = g/cm3
  Dvalue = 2.23
  Group = -> [B_element004,O_element043,Na_element008,Al_element003,Si_element003,K_element004]
  conduct = 2
  density = 1
  expand = 3
  formula = G4_Pyrex_Glass
  name = G4_Pyrex_Glass
  specific = 4
FEATURE [App::DocumentObjectGroupPython] O_element044  label="O_element : 0.156"  # scripted group (container) (typed FeaturePython)
  n = 0.156453
FEATURE [App::DocumentObjectGroupPython] Si_element004  label="Si_element : 0.081"  # scripted group (container) (typed FeaturePython)
  n = 0.080866
FEATURE [App::DocumentObjectGroupPython] Ti_element001  label="Ti_element : 0.008"  # scripted group (container) (typed FeaturePython)
  n = 0.008092
FEATURE [App::DocumentObjectGroupPython] As_element002  label="As_element : 0.003"  # scripted group (container) (typed FeaturePython)
  n = 0.002651
FEATURE [App::DocumentObjectGroupPython] Pb_element001  label="Pb_element : 0.752"  # scripted group (container) (typed FeaturePython)
  n = 0.751938
FEATURE [App::DocumentObjectGroupPython] G4_GLASS_LEAD  # scripted group (container) (typed FeaturePython)
  Dunit = g/cm3
  Dvalue = 6.22
  Group = -> [O_element044,Si_element004,Ti_element001,As_element002,Pb_element001]
  conduct = 2
  density = 1
  expand = 3
  formula = G4_GLASS_LEAD
  name = G4_GLASS_LEAD
  specific = 4
FEATURE [App::DocumentObjectGroupPython] O_element045  label="O_element : 0.460"  # scripted group (container) (typed FeaturePython)
  n = 0.4598
FEATURE [App::DocumentObjectGroupPython] Na_element009  label="Na_element : 0.096"  # scripted group (container) (typed FeaturePython)
  n = 0.0964411
FEATURE [App::DocumentObjectGroupPython] Si_element005  label="Si_element : 0.378"  # scripted group (container) (typed FeaturePython)
  n = 0.336553
FEATURE [App::DocumentObjectGroupPython] Ca_element011  label="Ca_element : 0.107"  # scripted group (container) (typed FeaturePython)
  n = 0.107205
FEATURE [App::DocumentObjectGroupPython] G4_GLASS_PLATE  # scripted group (container) (typed FeaturePython)
  Dunit = g/cm3
  Dvalue = 2.4
  Group = -> [O_element045,Na_element009,Si_element005,Ca_element011]
  conduct = 2
  density = 1
  expand = 3
  formula = G4_GLASS_PLATE
  name = G4_GLASS_PLATE
  specific = 4
FEATURE [App::DocumentObjectGroupPython] C_element049  label="C_element : 026"  # scripted group (container) (typed FeaturePython)
  n = 5
  ref = C_element
FEATURE [App::DocumentObjectGroupPython] H_element042  label="H_element : 021"  # scripted group (container) (typed FeaturePython)
  n = 10
  ref = H_element
FEATURE [App::DocumentObjectGroupPython] N_element019  label="N_element : 2"  # scripted group (container) (typed FeaturePython)
  n = 2
  ref = N_element
FEATURE [App::DocumentObjectGroupPython] O_element046  label="O_element : 022"  # scripted group (container) (typed FeaturePython)
  n = 3
  ref = O_element
FEATURE [App::DocumentObjectGroupPython] G4_GLUTAMINE  # scripted group (container) (typed FeaturePython)
  Dunit = g/cm3
  Dvalue = 1.46
  Group = -> [C_element049,H_element042,N_element019,O_element046]
  conduct = 2
  density = 1
  expand = 3
  formula = G4_GLUTAMINE
  name = G4_GLUTAMINE
  specific = 4
FEATURE [App::DocumentObjectGroupPython] C_element050  label="C_element : 027"  # scripted group (container) (typed FeaturePython)
  n = 3
  ref = C_element
FEATURE [App::DocumentObjectGroupPython] H_element043  label="H_element : 022"  # scripted group (container) (typed FeaturePython)
  n = 8
  ref = H_element
FEATURE [App::DocumentObjectGroupPython] O_element047  label="O_element : 023"  # scripted group (container) (typed FeaturePython)
  n = 3
  ref = O_element
FEATURE [App::DocumentObjectGroupPython] G4_GLYCEROL  # scripted group (container) (typed FeaturePython)
  Dunit = g/cm3
  Dvalue = 1.2613
  Group = -> [C_element050,H_element043,O_element047]
  conduct = 2
  density = 1
  expand = 3
  formula = G4_GLYCEROL
  name = G4_GLYCEROL
  specific = 4
FEATURE [App::DocumentObjectGroupPython] C_element051  label="C_element : 028"  # scripted group (container) (typed FeaturePython)
  n = 5
  ref = C_element
FEATURE [App::DocumentObjectGroupPython] H_element044  label="H_element : 023"  # scripted group (container) (typed FeaturePython)
  n = 5
  ref = H_element
FEATURE [App::DocumentObjectGroupPython] N_element020  label="N_element : 009"  # scripted group (container) (typed FeaturePython)
  n = 5
  ref = N_element
FEATURE [App::DocumentObjectGroupPython] O_element048  label="O_element : 024"  # scripted group (container) (typed FeaturePython)
  n = 1
  ref = O_element
FEATURE [App::DocumentObjectGroupPython] G4_GUANINE  # scripted group (container) (typed FeaturePython)
  Dunit = g/cm3
  Dvalue = 2.2
  Group = -> [C_element051,H_element044,N_element020,O_element048]
  conduct = 2
  density = 1
  expand = 3
  formula = G4_GUANINE
  name = G4_GUANINE
  specific = 4
FEATURE [App::DocumentObjectGroupPython] Ca_element012  label="Ca_element : 006"  # scripted group (container) (typed FeaturePython)
  n = 1
  ref = Ca_element
FEATURE [App::DocumentObjectGroupPython] S_element014  label="S_element : 005"  # scripted group (container) (typed FeaturePython)
  n = 1
  ref = S_element
FEATURE [App::DocumentObjectGroupPython] O_element049  label="O_element : 6"  # scripted group (container) (typed FeaturePython)
  n = 6
  ref = O_element
FEATURE [App::DocumentObjectGroupPython] H_element045  label="H_element : 024"  # scripted group (container) (typed FeaturePython)
  n = 4
  ref = H_element
FEATURE [App::DocumentObjectGroupPython] G4_GYPSUM  # scripted group (container) (typed FeaturePython)
  Dunit = g/cm3
  Dvalue = 2.32
  Group = -> [Ca_element012,S_element014,O_element049,H_element045]
  conduct = 2
  density = 1
  expand = 3
  formula = G4_GYPSUM
  name = G4_GYPSUM
  specific = 4
FEATURE [App::DocumentObjectGroupPython] C_element052  label="C_element : 7"  # scripted group (container) (typed FeaturePython)
  n = 7
  ref = C_element
FEATURE [App::DocumentObjectGroupPython] H_element046  label="H_element : 16"  # scripted group (container) (typed FeaturePython)
  n = 16
  ref = H_element
FEATURE [App::DocumentObjectGroupPython] G4_N_HEPTANE  label="G4_N-HEPTANE"  # scripted group (container) (typed FeaturePython)
  Dunit = g/cm3
  Dvalue = 0.68376
  Group = -> [C_element052,H_element046]
  conduct = 2
  density = 1
  expand = 3
  formula = G4_N-HEPTANE
  name = G4_N-HEPTANE
  specific = 4
FEATURE [App::DocumentObjectGroupPython] C_element053  label="C_element : 029"  # scripted group (container) (typed FeaturePython)
  n = 6
  ref = C_element
FEATURE [App::DocumentObjectGroupPython] H_element047  label="H_element : 14"  # scripted group (container) (typed FeaturePython)
  n = 14
  ref = H_element
FEATURE [App::DocumentObjectGroupPython] G4_N_HEXANE  label="G4_N-HEXANE"  # scripted group (container) (typed FeaturePython)
  Dunit = g/cm3
  Dvalue = 0.6603
  Group = -> [C_element053,H_element047]
  conduct = 2
  density = 1
  expand = 3
  formula = G4_N-HEXANE
  name = G4_N-HEXANE
  specific = 4
FEATURE [App::DocumentObjectGroupPython] C_element054  label="C_element : 22"  # scripted group (container) (typed FeaturePython)
  n = 22
  ref = C_element
FEATURE [App::DocumentObjectGroupPython] H_element048  label="H_element : 025"  # scripted group (container) (typed FeaturePython)
  n = 10
  ref = H_element
FEATURE [App::DocumentObjectGroupPython] N_element021  label="N_element : 010"  # scripted group (container) (typed FeaturePython)
  n = 2
  ref = N_element
FEATURE [App::DocumentObjectGroupPython] O_element050  label="O_element : 025"  # scripted group (container) (typed FeaturePython)
  n = 5
  ref = O_element
FEATURE [App::DocumentObjectGroupPython] G4_KAPTON  # scripted group (container) (typed FeaturePython)
  Dunit = g/cm3
  Dvalue = 1.42
  Group = -> [C_element054,H_element048,N_element021,O_element050]
  conduct = 2
  density = 1
  expand = 3
  formula = G4_KAPTON
  name = G4_KAPTON
  specific = 4
FEATURE [App::DocumentObjectGroupPython] La_element001  label="La_element : 1"  # scripted group (container) (typed FeaturePython)
  n = 1
  ref = La_element
FEATURE [App::DocumentObjectGroupPython] Br_element003  label="Br_element : 002"  # scripted group (container) (typed FeaturePython)
  n = 1
  ref = Br_element
FEATURE [App::DocumentObjectGroupPython] O_element051  label="O_element : 026"  # scripted group (container) (typed FeaturePython)
  n = 1
  ref = O_element
FEATURE [App::DocumentObjectGroupPython] G4_LANTHANUM_OXYBROMIDE  # scripted group (container) (typed FeaturePython)
  Dunit = g/cm3
  Dvalue = 6.28
  Group = -> [La_element001,Br_element003,O_element051]
  conduct = 2
  density = 1
  expand = 3
  formula = G4_LANTHANUM_OXYBROMIDE
  name = G4_LANTHANUM_OXYBROMIDE
  specific = 4
FEATURE [App::DocumentObjectGroupPython] La_element002  label="La_element : 2"  # scripted group (container) (typed FeaturePython)
  n = 2
  ref = La_element
FEATURE [App::DocumentObjectGroupPython] O_element052  label="O_element : 027"  # scripted group (container) (typed FeaturePython)
  n = 2
  ref = O_element
FEATURE [App::DocumentObjectGroupPython] S_element015  label="S_element : 006"  # scripted group (container) (typed FeaturePython)
  n = 1
  ref = S_element
FEATURE [App::DocumentObjectGroupPython] G4_LANTHANUM_OXYSULFIDE  # scripted group (container) (typed FeaturePython)
  Dunit = g/cm3
  Dvalue = 5.86
  Group = -> [La_element002,O_element052,S_element015]
  conduct = 2
  density = 1
  expand = 3
  formula = G4_LANTHANUM_OXYSULFIDE
  name = G4_LANTHANUM_OXYSULFIDE
  specific = 4
FEATURE [App::DocumentObjectGroupPython] O_element053  label="O_element : 0.072"  # scripted group (container) (typed FeaturePython)
  n = 0.071682
FEATURE [App::DocumentObjectGroupPython] Pb_element002  label="Pb_element : 0.928"  # scripted group (container) (typed FeaturePython)
  n = 0.928318
FEATURE [App::DocumentObjectGroupPython] G4_LEAD_OXIDE  # scripted group (container) (typed FeaturePython)
  Dunit = g/cm3
  Dvalue = 9.53
  Group = -> [O_element053,Pb_element002]
  conduct = 2
  density = 1
  expand = 3
  formula = G4_LEAD_OXIDE
  name = G4_LEAD_OXIDE
  specific = 4
FEATURE [App::DocumentObjectGroupPython] Li_element001  label="Li_element : 1"  # scripted group (container) (typed FeaturePython)
  n = 1
  ref = Li_element
FEATURE [App::DocumentObjectGroupPython] N_element022  label="N_element : 011"  # scripted group (container) (typed FeaturePython)
  n = 1
  ref = N_element
FEATURE [App::DocumentObjectGroupPython] H_element049  label="H_element : 026"  # scripted group (container) (typed FeaturePython)
  n = 2
  ref = H_element
FEATURE [App::DocumentObjectGroupPython] G4_LITHIUM_AMIDE  # scripted group (container) (typed FeaturePython)
  Dunit = g/cm3
  Dvalue = 1.178
  Group = -> [Li_element001,N_element022,H_element049]
  conduct = 2
  density = 1
  expand = 3
  formula = G4_LITHIUM_AMIDE
  name = G4_LITHIUM_AMIDE
  specific = 4
FEATURE [App::DocumentObjectGroupPython] Li_element002  label="Li_element : 2"  # scripted group (container) (typed FeaturePython)
  n = 2
  ref = Li_element
FEATURE [App::DocumentObjectGroupPython] C_element055  label="C_element : 030"  # scripted group (container) (typed FeaturePython)
  n = 1
  ref = C_element
FEATURE [App::DocumentObjectGroupPython] O_element054  label="O_element : 028"  # scripted group (container) (typed FeaturePython)
  n = 3
  ref = O_element
FEATURE [App::DocumentObjectGroupPython] G4_LITHIUM_CARBONATE  # scripted group (container) (typed FeaturePython)
  Dunit = g/cm3
  Dvalue = 2.11
  Group = -> [Li_element002,C_element055,O_element054]
  conduct = 2
  density = 1
  expand = 3
  formula = G4_LITHIUM_CARBONATE
  name = G4_LITHIUM_CARBONATE
  specific = 4
FEATURE [App::DocumentObjectGroupPython] Li_element003  label="Li_element : 003"  # scripted group (container) (typed FeaturePython)
  n = 1
  ref = Li_element
FEATURE [App::DocumentObjectGroupPython] F_element012  label="F_element : 004"  # scripted group (container) (typed FeaturePython)
  n = 1
  ref = F_element
FEATURE [App::DocumentObjectGroupPython] G4_LITHIUM_FLUORIDE  # scripted group (container) (typed FeaturePython)
  Dunit = g/cm3
  Dvalue = 2.635
  Group = -> [Li_element003,F_element012]
  conduct = 2
  density = 1
  expand = 3
  formula = G4_LITHIUM_FLUORIDE
  name = G4_LITHIUM_FLUORIDE
  specific = 4
FEATURE [App::DocumentObjectGroupPython] Li_element004  label="Li_element : 004"  # scripted group (container) (typed FeaturePython)
  n = 1
  ref = Li_element
FEATURE [App::DocumentObjectGroupPython] H_element050  label="H_element : 027"  # scripted group (container) (typed FeaturePython)
  n = 1
  ref = H_element
FEATURE [App::DocumentObjectGroupPython] G4_LITHIUM_HYDRIDE  # scripted group (container) (typed FeaturePython)
  Dunit = g/cm3
  Dvalue = 0.82
  Group = -> [Li_element004,H_element050]
  conduct = 2
  density = 1
  expand = 3
  formula = G4_LITHIUM_HYDRIDE
  name = G4_LITHIUM_HYDRIDE
  specific = 4
FEATURE [App::DocumentObjectGroupPython] Li_element005  label="Li_element : 005"  # scripted group (container) (typed FeaturePython)
  n = 1
  ref = Li_element
FEATURE [App::DocumentObjectGroupPython] I_element003  label="I_element : 002"  # scripted group (container) (typed FeaturePython)
  n = 1
  ref = I_element
FEATURE [App::DocumentObjectGroupPython] G4_LITHIUM_IODIDE  # scripted group (container) (typed FeaturePython)
  Dunit = g/cm3
  Dvalue = 3.494
  Group = -> [Li_element005,I_element003]
  conduct = 2
  density = 1
  expand = 3
  formula = G4_LITHIUM_IODIDE
  name = G4_LITHIUM_IODIDE
  specific = 4
FEATURE [App::DocumentObjectGroupPython] Li_element006  label="Li_element : 006"  # scripted group (container) (typed FeaturePython)
  n = 2
  ref = Li_element
FEATURE [App::DocumentObjectGroupPython] O_element055  label="O_element : 029"  # scripted group (container) (typed FeaturePython)
  n = 1
  ref = O_element
FEATURE [App::DocumentObjectGroupPython] G4_LITHIUM_OXIDE  # scripted group (container) (typed FeaturePython)
  Dunit = g/cm3
  Dvalue = 2.013
  Group = -> [Li_element006,O_element055]
  conduct = 2
  density = 1
  expand = 3
  formula = G4_LITHIUM_OXIDE
  name = G4_LITHIUM_OXIDE
  specific = 4
FEATURE [App::DocumentObjectGroupPython] Li_element007  label="Li_element : 007"  # scripted group (container) (typed FeaturePython)
  n = 2
  ref = Li_element
FEATURE [App::DocumentObjectGroupPython] B_element005  label="B_element : 005"  # scripted group (container) (typed FeaturePython)
  n = 4
  ref = B_element
FEATURE [App::DocumentObjectGroupPython] O_element056  label="O_element : 7"  # scripted group (container) (typed FeaturePython)
  n = 7
  ref = O_element
FEATURE [App::DocumentObjectGroupPython] G4_LITHIUM_TETRABORATE  # scripted group (container) (typed FeaturePython)
  Dunit = g/cm3
  Dvalue = 2.44
  Group = -> [Li_element007,B_element005,O_element056]
  conduct = 2
  density = 1
  expand = 3
  formula = G4_LITHIUM_TETRABORATE
  name = G4_LITHIUM_TETRABORATE
  specific = 4
FEATURE [App::DocumentObjectGroupPython] H_element051  label="H_element : 0.105"  # scripted group (container) (typed FeaturePython)
  n = 0.105
FEATURE [App::DocumentObjectGroupPython] C_element056  label="C_element : 0.083"  # scripted group (container) (typed FeaturePython)
  n = 0.083
FEATURE [App::DocumentObjectGroupPython] N_element023  label="N_element : 0.023"  # scripted group (container) (typed FeaturePython)
  n = 0.023
FEATURE [App::DocumentObjectGroupPython] O_element057  label="O_element : 0.779"  # scripted group (container) (typed FeaturePython)
  n = 0.779
FEATURE [App::DocumentObjectGroupPython] Na_element010  label="Na_element : 0.097"  # scripted group (container) (typed FeaturePython)
  n = 0.002
FEATURE [App::DocumentObjectGroupPython] P_element006  label="P_element : 0.105"  # scripted group (container) (typed FeaturePython)
  n = 0.001
FEATURE [App::DocumentObjectGroupPython] S_element016  label="S_element : 0.017"  # scripted group (container) (typed FeaturePython)
  n = 0.002
FEATURE [App::DocumentObjectGroupPython] Cl_element014  label="Cl_element : 0.587"  # scripted group (container) (typed FeaturePython)
  n = 0.003
FEATURE [App::DocumentObjectGroupPython] K_element005  label="K_element : 0.015"  # scripted group (container) (typed FeaturePython)
  n = 0.002
FEATURE [App::DocumentObjectGroupPython] G4_LUNG_ICRP  # scripted group (container) (typed FeaturePython)
  Dunit = g/cm3
  Dvalue = 1.04
  Group = -> [H_element051,C_element056,N_element023,O_element057,Na_element010,P_element006,S_element016,Cl_element014,K_element005]
  conduct = 2
  density = 1
  expand = 3
  formula = G4_LUNG_ICRP
  name = G4_LUNG_ICRP
  specific = 4
FEATURE [App::DocumentObjectGroupPython] H_element052  label="H_element : 0.116"  # scripted group (container) (typed FeaturePython)
  n = 0.114318
FEATURE [App::DocumentObjectGroupPython] C_element057  label="C_element : 0.656"  # scripted group (container) (typed FeaturePython)
  n = 0.655824
FEATURE [App::DocumentObjectGroupPython] O_element058  label="O_element : 0.092"  # scripted group (container) (typed FeaturePython)
  n = 0.0921831
FEATURE [App::DocumentObjectGroupPython] Mg_element004  label="Mg_element : 0.135"  # scripted group (container) (typed FeaturePython)
  n = 0.134792
FEATURE [App::DocumentObjectGroupPython] Ca_element013  label="Ca_element : 0.003"  # scripted group (container) (typed FeaturePython)
  n = 0.002883
FEATURE [App::DocumentObjectGroupPython] G4_M3_WAX  # scripted group (container) (typed FeaturePython)
  Dunit = g/cm3
  Dvalue = 1.05
  Group = -> [H_element052,C_element057,O_element058,Mg_element004,Ca_element013]
  conduct = 2
  density = 1
  expand = 3
  formula = G4_M3_WAX
  name = G4_M3_WAX
  specific = 4
FEATURE [App::DocumentObjectGroupPython] Mg_element005  label="Mg_element : 1"  # scripted group (container) (typed FeaturePython)
  n = 1
  ref = Mg_element
FEATURE [App::DocumentObjectGroupPython] C_element058  label="C_element : 031"  # scripted group (container) (typed FeaturePython)
  n = 1
  ref = C_element
FEATURE [App::DocumentObjectGroupPython] O_element059  label="O_element : 030"  # scripted group (container) (typed FeaturePython)
  n = 3
  ref = O_element
FEATURE [App::DocumentObjectGroupPython] G4_MAGNESIUM_CARBONATE  # scripted group (container) (typed FeaturePython)
  Dunit = g/cm3
  Dvalue = 2.958
  Group = -> [Mg_element005,C_element058,O_element059]
  conduct = 2
  density = 1
  expand = 3
  formula = G4_MAGNESIUM_CARBONATE
  name = G4_MAGNESIUM_CARBONATE
  specific = 4
FEATURE [App::DocumentObjectGroupPython] Mg_element006  label="Mg_element : 002"  # scripted group (container) (typed FeaturePython)
  n = 1
  ref = Mg_element
FEATURE [App::DocumentObjectGroupPython] F_element013  label="F_element : 005"  # scripted group (container) (typed FeaturePython)
  n = 2
  ref = F_element
FEATURE [App::DocumentObjectGroupPython] G4_MAGNESIUM_FLUORIDE  # scripted group (container) (typed FeaturePython)
  Dunit = g/cm3
  Dvalue = 3
  Group = -> [Mg_element006,F_element013]
  conduct = 2
  density = 1
  expand = 3
  formula = G4_MAGNESIUM_FLUORIDE
  name = G4_MAGNESIUM_FLUORIDE
  specific = 4
FEATURE [App::DocumentObjectGroupPython] Mg_element007  label="Mg_element : 003"  # scripted group (container) (typed FeaturePython)
  n = 1
  ref = Mg_element
FEATURE [App::DocumentObjectGroupPython] O_element060  label="O_element : 031"  # scripted group (container) (typed FeaturePython)
  n = 1
  ref = O_element
FEATURE [App::DocumentObjectGroupPython] G4_MAGNESIUM_OXIDE  # scripted group (container) (typed FeaturePython)
  Dunit = g/cm3
  Dvalue = 3.58
  Group = -> [Mg_element007,O_element060]
  conduct = 2
  density = 1
  expand = 3
  formula = G4_MAGNESIUM_OXIDE
  name = G4_MAGNESIUM_OXIDE
  specific = 4
FEATURE [App::DocumentObjectGroupPython] Mg_element008  label="Mg_element : 004"  # scripted group (container) (typed FeaturePython)
  n = 1
  ref = Mg_element
FEATURE [App::DocumentObjectGroupPython] B_element006  label="B_element : 006"  # scripted group (container) (typed FeaturePython)
  n = 4
  ref = B_element
FEATURE [App::DocumentObjectGroupPython] O_element061  label="O_element : 032"  # scripted group (container) (typed FeaturePython)
  n = 7
  ref = O_element
FEATURE [App::DocumentObjectGroupPython] G4_MAGNESIUM_TETRABORATE  # scripted group (container) (typed FeaturePython)
  Dunit = g/cm3
  Dvalue = 2.53
  Group = -> [Mg_element008,B_element006,O_element061]
  conduct = 2
  density = 1
  expand = 3
  formula = G4_MAGNESIUM_TETRABORATE
  name = G4_MAGNESIUM_TETRABORATE
  specific = 4
FEATURE [App::DocumentObjectGroupPython] Hg_element001  label="Hg_element : 1"  # scripted group (container) (typed FeaturePython)
  n = 1
  ref = Hg_element
FEATURE [App::DocumentObjectGroupPython] I_element004  label="I_element : 2"  # scripted group (container) (typed FeaturePython)
  n = 2
  ref = I_element
FEATURE [App::DocumentObjectGroupPython] G4_MERCURIC_IODIDE  # scripted group (container) (typed FeaturePython)
  Dunit = g/cm3
  Dvalue = 6.36
  Group = -> [Hg_element001,I_element004]
  conduct = 2
  density = 1
  expand = 3
  formula = G4_MERCURIC_IODIDE
  name = G4_MERCURIC_IODIDE
  specific = 4
FEATURE [App::DocumentObjectGroupPython] C_element059  label="C_element : 032"  # scripted group (container) (typed FeaturePython)
  n = 1
  ref = C_element
FEATURE [App::DocumentObjectGroupPython] H_element053  label="H_element : 028"  # scripted group (container) (typed FeaturePython)
  n = 4
  ref = H_element
FEATURE [App::DocumentObjectGroupPython] G4_METHANE  # scripted group (container) (typed FeaturePython)
  Dunit = g/cm3
  Dvalue = 0.000667151
  Group = -> [C_element059,H_element053]
  conduct = 2
  density = 1
  expand = 3
  formula = G4_METHANE
  name = G4_METHANE
  specific = 4
FEATURE [App::DocumentObjectGroupPython] C_element060  label="C_element : 033"  # scripted group (container) (typed FeaturePython)
  n = 1
  ref = C_element
FEATURE [App::DocumentObjectGroupPython] H_element054  label="H_element : 029"  # scripted group (container) (typed FeaturePython)
  n = 4
  ref = H_element
FEATURE [App::DocumentObjectGroupPython] O_element062  label="O_element : 033"  # scripted group (container) (typed FeaturePython)
  n = 1
  ref = O_element
FEATURE [App::DocumentObjectGroupPython] G4_METHANOL  # scripted group (container) (typed FeaturePython)
  Dunit = g/cm3
  Dvalue = 0.7914
  Group = -> [C_element060,H_element054,O_element062]
  conduct = 2
  density = 1
  expand = 3
  formula = G4_METHANOL
  name = G4_METHANOL
  specific = 4
FEATURE [App::DocumentObjectGroupPython] H_element055  label="H_element : 0.134"  # scripted group (container) (typed FeaturePython)
  n = 0.13404
FEATURE [App::DocumentObjectGroupPython] C_element061  label="C_element : 0.778"  # scripted group (container) (typed FeaturePython)
  n = 0.77796
FEATURE [App::DocumentObjectGroupPython] O_element063  label="O_element : 0.035"  # scripted group (container) (typed FeaturePython)
  n = 0.03502
FEATURE [App::DocumentObjectGroupPython] Mg_element009  label="Mg_element : 0.039"  # scripted group (container) (typed FeaturePython)
  n = 0.038594
FEATURE [App::DocumentObjectGroupPython] Ti_element002  label="Ti_element : 0.014"  # scripted group (container) (typed FeaturePython)
  n = 0.014386
FEATURE [App::DocumentObjectGroupPython] G4_MIX_D_WAX  # scripted group (container) (typed FeaturePython)
  Dunit = g/cm3
  Dvalue = 0.99
  Group = -> [H_element055,C_element061,O_element063,Mg_element009,Ti_element002]
  conduct = 2
  density = 1
  expand = 3
  formula = G4_MIX_D_WAX
  name = G4_MIX_D_WAX
  specific = 4
FEATURE [App::DocumentObjectGroupPython] H_element056  label="H_element : 0.135"  # scripted group (container) (typed FeaturePython)
  n = 0.081192
FEATURE [App::DocumentObjectGroupPython] C_element062  label="C_element : 0.583"  # scripted group (container) (typed FeaturePython)
  n = 0.583442
FEATURE [App::DocumentObjectGroupPython] N_element024  label="N_element : 0.018"  # scripted group (container) (typed FeaturePython)
  n = 0.017798
FEATURE [App::DocumentObjectGroupPython] O_element064  label="O_element : 0.186"  # scripted group (container) (typed FeaturePython)
  n = 0.186381
FEATURE [App::DocumentObjectGroupPython] Mg_element010  label="Mg_element : 0.130"  # scripted group (container) (typed FeaturePython)
  n = 0.130287
FEATURE [App::DocumentObjectGroupPython] Cl_element015  label="Cl_element : 0.588"  # scripted group (container) (typed FeaturePython)
  n = 0.0009
FEATURE [App::DocumentObjectGroupPython] G4_MS20_TISSUE  # scripted group (container) (typed FeaturePython)
  Dunit = g/cm3
  Dvalue = 1
  Group = -> [H_element056,C_element062,N_element024,O_element064,Mg_element010,Cl_element015]
  conduct = 2
  density = 1
  expand = 3
  formula = G4_MS20_TISSUE
  name = G4_MS20_TISSUE
  specific = 4
FEATURE [App::DocumentObjectGroupPython] H_element057  label="H_element : 0.136"  # scripted group (container) (typed FeaturePython)
  n = 0.102
FEATURE [App::DocumentObjectGroupPython] C_element063  label="C_element : 0.143"  # scripted group (container) (typed FeaturePython)
  n = 0.143
FEATURE [App::DocumentObjectGroupPython] N_element025  label="N_element : 0.034"  # scripted group (container) (typed FeaturePython)
  n = 0.034
FEATURE [App::DocumentObjectGroupPython] O_element065  label="O_element : 0.710"  # scripted group (container) (typed FeaturePython)
  n = 0.71
FEATURE [App::DocumentObjectGroupPython] Na_element011  label="Na_element : 0.098"  # scripted group (container) (typed FeaturePython)
  n = 0.001
FEATURE [App::DocumentObjectGroupPython] P_element007  label="P_element : 0.002"  # scripted group (container) (typed FeaturePython)
  n = 0.002
FEATURE [App::DocumentObjectGroupPython] S_element017  label="S_element : 0.018"  # scripted group (container) (typed FeaturePython)
  n = 0.003
FEATURE [App::DocumentObjectGroupPython] Cl_element016  label="Cl_element : 0.589"  # scripted group (container) (typed FeaturePython)
  n = 0.001
FEATURE [App::DocumentObjectGroupPython] K_element006  label="K_element : 0.004"  # scripted group (container) (typed FeaturePython)
  n = 0.004
FEATURE [App::DocumentObjectGroupPython] G4_MUSCLE_SKELETAL_ICRP  # scripted group (container) (typed FeaturePython)
  Dunit = g/cm3
  Dvalue = 1.05
  Group = -> [H_element057,C_element063,N_element025,O_element065,Na_element011,P_element007,S_element017,Cl_element016,K_element006]
  conduct = 2
  density = 1
  expand = 3
  formula = G4_MUSCLE_SKELETAL_ICRP
  name = G4_MUSCLE_SKELETAL_ICRP
  specific = 4
FEATURE [App::DocumentObjectGroupPython] H_element058  label="H_element : 0.137"  # scripted group (container) (typed FeaturePython)
  n = 0.102102
FEATURE [App::DocumentObjectGroupPython] C_element064  label="C_element : 0.123"  # scripted group (container) (typed FeaturePython)
  n = 0.123123
FEATURE [App::DocumentObjectGroupPython] N_element026  label="N_element : 0.756"  # scripted group (container) (typed FeaturePython)
  n = 0.035035
FEATURE [App::DocumentObjectGroupPython] O_element066  label="O_element : 0.730"  # scripted group (container) (typed FeaturePython)
  n = 0.72973
FEATURE [App::DocumentObjectGroupPython] Na_element012  label="Na_element : 0.099"  # scripted group (container) (typed FeaturePython)
  n = 0.001001
FEATURE [App::DocumentObjectGroupPython] P_element008  label="P_element : 0.106"  # scripted group (container) (typed FeaturePython)
  n = 0.002002
FEATURE [App::DocumentObjectGroupPython] S_element018  label="S_element : 0.019"  # scripted group (container) (typed FeaturePython)
  n = 0.004004
FEATURE [App::DocumentObjectGroupPython] K_element007  label="K_element : 0.016"  # scripted group (container) (typed FeaturePython)
  n = 0.003003
FEATURE [App::DocumentObjectGroupPython] G4_MUSCLE_STRIATED_ICRU  # scripted group (container) (typed FeaturePython)
  Dunit = g/cm3
  Dvalue = 1.04
  Group = -> [H_element058,C_element064,N_element026,O_element066,Na_element012,P_element008,S_element018,K_element007]
  conduct = 2
  density = 1
  expand = 3
  formula = G4_MUSCLE_STRIATED_ICRU
  name = G4_MUSCLE_STRIATED_ICRU
  specific = 4
FEATURE [App::DocumentObjectGroupPython] H_element059  label="H_element : 0.098"  # scripted group (container) (typed FeaturePython)
  n = 0.0982341
FEATURE [App::DocumentObjectGroupPython] C_element065  label="C_element : 0.156"  # scripted group (container) (typed FeaturePython)
  n = 0.156214
FEATURE [App::DocumentObjectGroupPython] N_element027  label="N_element : 0.757"  # scripted group (container) (typed FeaturePython)
  n = 0.035451
FEATURE [App::DocumentObjectGroupPython] O_element067  label="O_element : 0.880"  # scripted group (container) (typed FeaturePython)
  n = 0.710101
FEATURE [App::DocumentObjectGroupPython] G4_MUSCLE_WITH_SUCROSE  # scripted group (container) (typed FeaturePython)
  Dunit = g/cm3
  Dvalue = 1.11
  Group = -> [H_element059,C_element065,N_element027,O_element067]
  conduct = 2
  density = 1
  expand = 3
  formula = G4_MUSCLE_WITH_SUCROSE
  name = G4_MUSCLE_WITH_SUCROSE
  specific = 4
FEATURE [App::DocumentObjectGroupPython] H_element060  label="H_element : 0.138"  # scripted group (container) (typed FeaturePython)
  n = 0.101969
FEATURE [App::DocumentObjectGroupPython] C_element066  label="C_element : 0.120"  # scripted group (container) (typed FeaturePython)
  n = 0.120058
FEATURE [App::DocumentObjectGroupPython] N_element028  label="N_element : 0.758"  # scripted group (container) (typed FeaturePython)
  n = 0.035451
FEATURE [App::DocumentObjectGroupPython] O_element068  label="O_element : 0.743"  # scripted group (container) (typed FeaturePython)
  n = 0.742522
FEATURE [App::DocumentObjectGroupPython] G4_MUSCLE_WITHOUT_SUCROSE  # scripted group (container) (typed FeaturePython)
  Dunit = g/cm3
  Dvalue = 1.07
  Group = -> [H_element060,C_element066,N_element028,O_element068]
  conduct = 2
  density = 1
  expand = 3
  formula = G4_MUSCLE_WITHOUT_SUCROSE
  name = G4_MUSCLE_WITHOUT_SUCROSE
  specific = 4
FEATURE [App::DocumentObjectGroupPython] C_element067  label="C_element : 10"  # scripted group (container) (typed FeaturePython)
  n = 10
  ref = C_element
FEATURE [App::DocumentObjectGroupPython] H_element061  label="H_element : 030"  # scripted group (container) (typed FeaturePython)
  n = 8
  ref = H_element
FEATURE [App::DocumentObjectGroupPython] G4_NAPHTHALENE  # scripted group (container) (typed FeaturePython)
  Dunit = g/cm3
  Dvalue = 1.145
  Group = -> [C_element067,H_element061]
  conduct = 2
  density = 1
  expand = 3
  formula = G4_NAPHTHALENE
  name = G4_NAPHTHALENE
  specific = 4
FEATURE [App::DocumentObjectGroupPython] C_element068  label="C_element : 034"  # scripted group (container) (typed FeaturePython)
  n = 6
  ref = C_element
FEATURE [App::DocumentObjectGroupPython] H_element062  label="H_element : 031"  # scripted group (container) (typed FeaturePython)
  n = 5
  ref = H_element
FEATURE [App::DocumentObjectGroupPython] N_element029  label="N_element : 012"  # scripted group (container) (typed FeaturePython)
  n = 1
  ref = N_element
FEATURE [App::DocumentObjectGroupPython] O_element069  label="O_element : 034"  # scripted group (container) (typed FeaturePython)
  n = 2
  ref = O_element
FEATURE [App::DocumentObjectGroupPython] G4_NITROBENZENE  # scripted group (container) (typed FeaturePython)
  Dunit = g/cm3
  Dvalue = 1.19867
  Group = -> [C_element068,H_element062,N_element029,O_element069]
  conduct = 2
  density = 1
  expand = 3
  formula = G4_NITROBENZENE
  name = G4_NITROBENZENE
  specific = 4
FEATURE [App::DocumentObjectGroupPython] N_element030  label="N_element : 013"  # scripted group (container) (typed FeaturePython)
  n = 2
  ref = N_element
FEATURE [App::DocumentObjectGroupPython] O_element070  label="O_element : 035"  # scripted group (container) (typed FeaturePython)
  n = 1
  ref = O_element
FEATURE [App::DocumentObjectGroupPython] G4_NITROUS_OXIDE  # scripted group (container) (typed FeaturePython)
  Dunit = g/cm3
  Dvalue = 0.00183094
  Group = -> [N_element030,O_element070]
  conduct = 2
  density = 1
  expand = 3
  formula = G4_NITROUS_OXIDE
  name = G4_NITROUS_OXIDE
  specific = 4
FEATURE [App::DocumentObjectGroupPython] H_element063  label="H_element : 0.104"  # scripted group (container) (typed FeaturePython)
  n = 0.103509
FEATURE [App::DocumentObjectGroupPython] C_element069  label="C_element : 0.648"  # scripted group (container) (typed FeaturePython)
  n = 0.648416
FEATURE [App::DocumentObjectGroupPython] N_element031  label="N_element : 0.100"  # scripted group (container) (typed FeaturePython)
  n = 0.0995361
FEATURE [App::DocumentObjectGroupPython] O_element071  label="O_element : 0.149"  # scripted group (container) (typed FeaturePython)
  n = 0.148539
FEATURE [App::DocumentObjectGroupPython] G4_NYLON_8062  label="G4_NYLON-8062"  # scripted group (container) (typed FeaturePython)
  Dunit = g/cm3
  Dvalue = 1.08
  Group = -> [H_element063,C_element069,N_element031,O_element071]
  conduct = 2
  density = 1
  expand = 3
  formula = G4_NYLON-8062
  name = G4_NYLON-8062
  specific = 4
FEATURE [App::DocumentObjectGroupPython] C_element070  label="C_element : 035"  # scripted group (container) (typed FeaturePython)
  n = 6
  ref = C_element
FEATURE [App::DocumentObjectGroupPython] H_element064  label="H_element : 11"  # scripted group (container) (typed FeaturePython)
  n = 11
  ref = H_element
FEATURE [App::DocumentObjectGroupPython] N_element032  label="N_element : 014"  # scripted group (container) (typed FeaturePython)
  n = 1
  ref = N_element
FEATURE [App::DocumentObjectGroupPython] O_element072  label="O_element : 036"  # scripted group (container) (typed FeaturePython)
  n = 1
  ref = O_element
FEATURE [App::DocumentObjectGroupPython] G4_NYLON_6_6  label="G4_NYLON-6-6"  # scripted group (container) (typed FeaturePython)
  Dunit = g/cm3
  Dvalue = 1.14
  Group = -> [C_element070,H_element064,N_element032,O_element072]
  conduct = 2
  density = 1
  expand = 3
  formula = G4_NYLON-6-6
  name = G4_NYLON-6-6
  specific = 4
FEATURE [App::DocumentObjectGroupPython] H_element065  label="H_element : 0.139"  # scripted group (container) (typed FeaturePython)
  n = 0.107062
FEATURE [App::DocumentObjectGroupPython] C_element071  label="C_element : 0.680"  # scripted group (container) (typed FeaturePython)
  n = 0.680449
FEATURE [App::DocumentObjectGroupPython] N_element033  label="N_element : 0.099"  # scripted group (container) (typed FeaturePython)
  n = 0.099189
FEATURE [App::DocumentObjectGroupPython] O_element073  label="O_element : 0.113"  # scripted group (container) (typed FeaturePython)
  n = 0.1133
FEATURE [App::DocumentObjectGroupPython] G4_NYLON_6_10  label="G4_NYLON-6-10"  # scripted group (container) (typed FeaturePython)
  Dunit = g/cm3
  Dvalue = 1.14
  Group = -> [H_element065,C_element071,N_element033,O_element073]
  conduct = 2
  density = 1
  expand = 3
  formula = G4_NYLON-6-10
  name = G4_NYLON-6-10
  specific = 4
FEATURE [App::DocumentObjectGroupPython] H_element066  label="H_element : 0.140"  # scripted group (container) (typed FeaturePython)
  n = 0.115476
FEATURE [App::DocumentObjectGroupPython] C_element072  label="C_element : 0.721"  # scripted group (container) (typed FeaturePython)
  n = 0.720818
FEATURE [App::DocumentObjectGroupPython] N_element034  label="N_element : 0.076"  # scripted group (container) (typed FeaturePython)
  n = 0.0764169
FEATURE [App::DocumentObjectGroupPython] O_element074  label="O_element : 0.087"  # scripted group (container) (typed FeaturePython)
  n = 0.0872889
FEATURE [App::DocumentObjectGroupPython] G4_NYLON_11_RILSAN  label="G4_NYLON-11_RILSAN"  # scripted group (container) (typed FeaturePython)
  Dunit = g/cm3
  Dvalue = 1.425
  Group = -> [H_element066,C_element072,N_element034,O_element074]
  conduct = 2
  density = 1
  expand = 3
  formula = G4_NYLON-11_RILSAN
  name = G4_NYLON-11_RILSAN
  specific = 4
FEATURE [App::DocumentObjectGroupPython] C_element073  label="C_element : 8"  # scripted group (container) (typed FeaturePython)
  n = 8
  ref = C_element
FEATURE [App::DocumentObjectGroupPython] H_element067  label="H_element : 18"  # scripted group (container) (typed FeaturePython)
  n = 18
  ref = H_element
FEATURE [App::DocumentObjectGroupPython] G4_OCTANE  # scripted group (container) (typed FeaturePython)
  Dunit = g/cm3
  Dvalue = 0.7026
  Group = -> [C_element073,H_element067]
  conduct = 2
  density = 1
  expand = 3
  formula = G4_OCTANE
  name = G4_OCTANE
  specific = 4
FEATURE [App::DocumentObjectGroupPython] C_element074  label="C_element : 25"  # scripted group (container) (typed FeaturePython)
  n = 25
  ref = C_element
FEATURE [App::DocumentObjectGroupPython] H_element068  label="H_element : 52"  # scripted group (container) (typed FeaturePython)
  n = 52
  ref = H_element
FEATURE [App::DocumentObjectGroupPython] G4_PARAFFIN  # scripted group (container) (typed FeaturePython)
  Dunit = g/cm3
  Dvalue = 0.93
  Group = -> [C_element074,H_element068]
  conduct = 2
  density = 1
  expand = 3
  formula = G4_PARAFFIN
  name = G4_PARAFFIN
  specific = 4
FEATURE [App::DocumentObjectGroupPython] C_element075  label="C_element : 036"  # scripted group (container) (typed FeaturePython)
  n = 5
  ref = C_element
FEATURE [App::DocumentObjectGroupPython] H_element069  label="H_element : 032"  # scripted group (container) (typed FeaturePython)
  n = 12
  ref = H_element
FEATURE [App::DocumentObjectGroupPython] G4_N_PENTANE  label="G4_N-PENTANE"  # scripted group (container) (typed FeaturePython)
  Dunit = g/cm3
  Dvalue = 0.6262
  Group = -> [C_element075,H_element069]
  conduct = 2
  density = 1
  expand = 3
  formula = G4_N-PENTANE
  name = G4_N-PENTANE
  specific = 4
FEATURE [App::DocumentObjectGroupPython] H_element070  label="H_element : 0.014"  # scripted group (container) (typed FeaturePython)
  n = 0.0141
FEATURE [App::DocumentObjectGroupPython] C_element076  label="C_element : 0.072"  # scripted group (container) (typed FeaturePython)
  n = 0.072261
FEATURE [App::DocumentObjectGroupPython] N_element035  label="N_element : 0.019"  # scripted group (container) (typed FeaturePython)
  n = 0.01932
FEATURE [App::DocumentObjectGroupPython] O_element075  label="O_element : 0.066"  # scripted group (container) (typed FeaturePython)
  n = 0.066101
FEATURE [App::DocumentObjectGroupPython] S_element019  label="S_element : 0.020"  # scripted group (container) (typed FeaturePython)
  n = 0.00189
FEATURE [App::DocumentObjectGroupPython] Br_element004  label="Br_element : 0.349"  # scripted group (container) (typed FeaturePython)
  n = 0.349103
FEATURE [App::DocumentObjectGroupPython] Ag_element001  label="Ag_element : 0.474"  # scripted group (container) (typed FeaturePython)
  n = 0.474105
FEATURE [App::DocumentObjectGroupPython] I_element005  label="I_element : 0.003"  # scripted group (container) (typed FeaturePython)
  n = 0.00312
FEATURE [App::DocumentObjectGroupPython] G4_PHOTO_EMULSION  # scripted group (container) (typed FeaturePython)
  Dunit = g/cm3
  Dvalue = 3.815
  Group = -> [H_element070,C_element076,N_element035,O_element075,S_element019,Br_element004,Ag_element001,I_element005]
  conduct = 2
  density = 1
  expand = 3
  formula = G4_PHOTO_EMULSION
  name = G4_PHOTO_EMULSION
  specific = 4
FEATURE [App::DocumentObjectGroupPython] C_element077  label="C_element : 9"  # scripted group (container) (typed FeaturePython)
  n = 9
  ref = C_element
FEATURE [App::DocumentObjectGroupPython] H_element071  label="H_element : 033"  # scripted group (container) (typed FeaturePython)
  n = 10
  ref = H_element
FEATURE [App::DocumentObjectGroupPython] G4_PLASTIC_SC_VINYLTOLUENE  # scripted group (container) (typed FeaturePython)
  Dunit = g/cm3
  Dvalue = 1.032
  Group = -> [C_element077,H_element071]
  conduct = 2
  density = 1
  expand = 3
  formula = G4_PLASTIC_SC_VINYLTOLUENE
  name = G4_PLASTIC_SC_VINYLTOLUENE
  specific = 4
FEATURE [App::DocumentObjectGroupPython] Pu_element001  label="Pu_element : 1"  # scripted group (container) (typed FeaturePython)
  n = 1
  ref = Pu_element
FEATURE [App::DocumentObjectGroupPython] O_element076  label="O_element : 037"  # scripted group (container) (typed FeaturePython)
  n = 2
  ref = O_element
FEATURE [App::DocumentObjectGroupPython] G4_PLUTONIUM_DIOXIDE  # scripted group (container) (typed FeaturePython)
  Dunit = g/cm3
  Dvalue = 11.46
  Group = -> [Pu_element001,O_element076]
  conduct = 2
  density = 1
  expand = 3
  formula = G4_PLUTONIUM_DIOXIDE
  name = G4_PLUTONIUM_DIOXIDE
  specific = 4
FEATURE [App::DocumentObjectGroupPython] C_element078  label="C_element : 037"  # scripted group (container) (typed FeaturePython)
  n = 3
  ref = C_element
FEATURE [App::DocumentObjectGroupPython] H_element072  label="H_element : 034"  # scripted group (container) (typed FeaturePython)
  n = 3
  ref = H_element
FEATURE [App::DocumentObjectGroupPython] N_element036  label="N_element : 015"  # scripted group (container) (typed FeaturePython)
  n = 1
  ref = N_element
FEATURE [App::DocumentObjectGroupPython] G4_POLYACRYLONITRILE  # scripted group (container) (typed FeaturePython)
  Dunit = g/cm3
  Dvalue = 1.17
  Group = -> [C_element078,H_element072,N_element036]
  conduct = 2
  density = 1
  expand = 3
  formula = G4_POLYACRYLONITRILE
  name = G4_POLYACRYLONITRILE
  specific = 4
FEATURE [App::DocumentObjectGroupPython] C_element079  label="C_element : 16"  # scripted group (container) (typed FeaturePython)
  n = 16
  ref = C_element
FEATURE [App::DocumentObjectGroupPython] H_element073  label="H_element : 035"  # scripted group (container) (typed FeaturePython)
  n = 14
  ref = H_element
FEATURE [App::DocumentObjectGroupPython] O_element077  label="O_element : 038"  # scripted group (container) (typed FeaturePython)
  n = 3
  ref = O_element
FEATURE [App::DocumentObjectGroupPython] G4_POLYCARBONATE  # scripted group (container) (typed FeaturePython)
  Dunit = g/cm3
  Dvalue = 1.2
  Group = -> [C_element079,H_element073,O_element077]
  conduct = 2
  density = 1
  expand = 3
  formula = G4_POLYCARBONATE
  name = G4_POLYCARBONATE
  specific = 4
FEATURE [App::DocumentObjectGroupPython] C_element080  label="C_element : 038"  # scripted group (container) (typed FeaturePython)
  n = 8
  ref = C_element
FEATURE [App::DocumentObjectGroupPython] H_element074  label="H_element : 036"  # scripted group (container) (typed FeaturePython)
  n = 7
  ref = H_element
FEATURE [App::DocumentObjectGroupPython] Cl_element017  label="Cl_element : 007"  # scripted group (container) (typed FeaturePython)
  n = 1
  ref = Cl_element
FEATURE [App::DocumentObjectGroupPython] G4_POLYCHLOROSTYRENE  # scripted group (container) (typed FeaturePython)
  Dunit = g/cm3
  Dvalue = 1.3
  Group = -> [C_element080,H_element074,Cl_element017]
  conduct = 2
  density = 1
  expand = 3
  formula = G4_POLYCHLOROSTYRENE
  name = G4_POLYCHLOROSTYRENE
  specific = 4
FEATURE [App::DocumentObjectGroupPython] C_element081  label="C_element : 039"  # scripted group (container) (typed FeaturePython)
  n = 1
  ref = C_element
FEATURE [App::DocumentObjectGroupPython] H_element075  label="H_element : 037"  # scripted group (container) (typed FeaturePython)
  n = 2
  ref = H_element
FEATURE [App::DocumentObjectGroupPython] G4_POLYETHYLENE  # scripted group (container) (typed FeaturePython)
  Dunit = g/cm3
  Dvalue = 0.94
  Group = -> [C_element081,H_element075]
  conduct = 2
  density = 1
  expand = 3
  formula = G4_POLYETHYLENE
  name = G4_POLYETHYLENE
  specific = 4
FEATURE [App::DocumentObjectGroupPython] C_element082  label="C_element : 040"  # scripted group (container) (typed FeaturePython)
  n = 10
  ref = C_element
FEATURE [App::DocumentObjectGroupPython] H_element076  label="H_element : 038"  # scripted group (container) (typed FeaturePython)
  n = 8
  ref = H_element
FEATURE [App::DocumentObjectGroupPython] O_element078  label="O_element : 039"  # scripted group (container) (typed FeaturePython)
  n = 4
  ref = O_element
FEATURE [App::DocumentObjectGroupPython] G4_MYLAR  # scripted group (container) (typed FeaturePython)
  Dunit = g/cm3
  Dvalue = 1.4
  Group = -> [C_element082,H_element076,O_element078]
  conduct = 2
  density = 1
  expand = 3
  formula = G4_MYLAR
  name = G4_MYLAR
  specific = 4
FEATURE [App::DocumentObjectGroupPython] C_element083  label="C_element : 041"  # scripted group (container) (typed FeaturePython)
  n = 5
  ref = C_element
FEATURE [App::DocumentObjectGroupPython] H_element077  label="H_element : 039"  # scripted group (container) (typed FeaturePython)
  n = 8
  ref = H_element
FEATURE [App::DocumentObjectGroupPython] O_element079  label="O_element : 040"  # scripted group (container) (typed FeaturePython)
  n = 2
  ref = O_element
FEATURE [App::DocumentObjectGroupPython] G4_PLEXIGLASS  # scripted group (container) (typed FeaturePython)
  Dunit = g/cm3
  Dvalue = 1.19
  Group = -> [C_element083,H_element077,O_element079]
  conduct = 2
  density = 1
  expand = 3
  formula = G4_PLEXIGLASS
  name = G4_PLEXIGLASS
  specific = 4
FEATURE [App::DocumentObjectGroupPython] C_element084  label="C_element : 042"  # scripted group (container) (typed FeaturePython)
  n = 1
  ref = C_element
FEATURE [App::DocumentObjectGroupPython] H_element078  label="H_element : 040"  # scripted group (container) (typed FeaturePython)
  n = 2
  ref = H_element
FEATURE [App::DocumentObjectGroupPython] O_element080  label="O_element : 041"  # scripted group (container) (typed FeaturePython)
  n = 1
  ref = O_element
FEATURE [App::DocumentObjectGroupPython] G4_POLYOXYMETHYLENE  # scripted group (container) (typed FeaturePython)
  Dunit = g/cm3
  Dvalue = 1.425
  Group = -> [C_element084,H_element078,O_element080]
  conduct = 2
  density = 1
  expand = 3
  formula = G4_POLYOXYMETHYLENE
  name = G4_POLYOXYMETHYLENE
  specific = 4
FEATURE [App::DocumentObjectGroupPython] C_element085  label="C_element : 043"  # scripted group (container) (typed FeaturePython)
  n = 2
  ref = C_element
FEATURE [App::DocumentObjectGroupPython] H_element079  label="H_element : 041"  # scripted group (container) (typed FeaturePython)
  n = 4
  ref = H_element
FEATURE [App::DocumentObjectGroupPython] G4_POLYPROPYLENE  # scripted group (container) (typed FeaturePython)
  Dunit = g/cm3
  Dvalue = 0.9
  Group = -> [C_element085,H_element079]
  conduct = 2
  density = 1
  expand = 3
  formula = G4_POLYPROPYLENE
  name = G4_POLYPROPYLENE
  specific = 4
FEATURE [App::DocumentObjectGroupPython] C_element086  label="C_element : 044"  # scripted group (container) (typed FeaturePython)
  n = 8
  ref = C_element
FEATURE [App::DocumentObjectGroupPython] H_element080  label="H_element : 042"  # scripted group (container) (typed FeaturePython)
  n = 8
  ref = H_element
FEATURE [App::DocumentObjectGroupPython] G4_POLYSTYRENE  # scripted group (container) (typed FeaturePython)
  Dunit = g/cm3
  Dvalue = 1.06
  Group = -> [C_element086,H_element080]
  conduct = 2
  density = 1
  expand = 3
  formula = G4_POLYSTYRENE
  name = G4_POLYSTYRENE
  specific = 4
FEATURE [App::DocumentObjectGroupPython] C_element087  label="C_element : 045"  # scripted group (container) (typed FeaturePython)
  n = 2
  ref = C_element
FEATURE [App::DocumentObjectGroupPython] F_element014  label="F_element : 4"  # scripted group (container) (typed FeaturePython)
  n = 4
  ref = F_element
FEATURE [App::DocumentObjectGroupPython] G4_TEFLON  # scripted group (container) (typed FeaturePython)
  Dunit = g/cm3
  Dvalue = 2.2
  Group = -> [C_element087,F_element014]
  conduct = 2
  density = 1
  expand = 3
  formula = G4_TEFLON
  name = G4_TEFLON
  specific = 4
FEATURE [App::DocumentObjectGroupPython] C_element088  label="C_element : 046"  # scripted group (container) (typed FeaturePython)
  n = 2
  ref = C_element
FEATURE [App::DocumentObjectGroupPython] F_element015  label="F_element : 006"  # scripted group (container) (typed FeaturePython)
  n = 3
  ref = F_element
FEATURE [App::DocumentObjectGroupPython] Cl_element018  label="Cl_element : 008"  # scripted group (container) (typed FeaturePython)
  n = 1
  ref = Cl_element
FEATURE [App::DocumentObjectGroupPython] G4_POLYTRIFLUOROCHLOROETHYLENE  # scripted group (container) (typed FeaturePython)
  Dunit = g/cm3
  Dvalue = 2.1
  Group = -> [C_element088,F_element015,Cl_element018]
  conduct = 2
  density = 1
  expand = 3
  formula = G4_POLYTRIFLUOROCHLOROETHYLENE
  name = G4_POLYTRIFLUOROCHLOROETHYLENE
  specific = 4
FEATURE [App::DocumentObjectGroupPython] C_element089  label="C_element : 047"  # scripted group (container) (typed FeaturePython)
  n = 4
  ref = C_element
FEATURE [App::DocumentObjectGroupPython] H_element081  label="H_element : 043"  # scripted group (container) (typed FeaturePython)
  n = 6
  ref = H_element
FEATURE [App::DocumentObjectGroupPython] O_element081  label="O_element : 042"  # scripted group (container) (typed FeaturePython)
  n = 2
  ref = O_element
FEATURE [App::DocumentObjectGroupPython] G4_POLYVINYL_ACETATE  # scripted group (container) (typed FeaturePython)
  Dunit = g/cm3
  Dvalue = 1.19
  Group = -> [C_element089,H_element081,O_element081]
  conduct = 2
  density = 1
  expand = 3
  formula = G4_POLYVINYL_ACETATE
  name = G4_POLYVINYL_ACETATE
  specific = 4
FEATURE [App::DocumentObjectGroupPython] C_element090  label="C_element : 048"  # scripted group (container) (typed FeaturePython)
  n = 2
  ref = C_element
FEATURE [App::DocumentObjectGroupPython] H_element082  label="H_element : 044"  # scripted group (container) (typed FeaturePython)
  n = 4
  ref = H_element
FEATURE [App::DocumentObjectGroupPython] O_element082  label="O_element : 043"  # scripted group (container) (typed FeaturePython)
  n = 1
  ref = O_element
FEATURE [App::DocumentObjectGroupPython] G4_POLYVINYL_ALCOHOL  # scripted group (container) (typed FeaturePython)
  Dunit = g/cm3
  Dvalue = 1.3
  Group = -> [C_element090,H_element082,O_element082]
  conduct = 2
  density = 1
  expand = 3
  formula = G4_POLYVINYL_ALCOHOL
  name = G4_POLYVINYL_ALCOHOL
  specific = 4
FEATURE [App::DocumentObjectGroupPython] C_element091  label="C_element : 049"  # scripted group (container) (typed FeaturePython)
  n = 8
  ref = C_element
FEATURE [App::DocumentObjectGroupPython] H_element083  label="H_element : 045"  # scripted group (container) (typed FeaturePython)
  n = 14
  ref = H_element
FEATURE [App::DocumentObjectGroupPython] O_element083  label="O_element : 044"  # scripted group (container) (typed FeaturePython)
  n = 2
  ref = O_element
FEATURE [App::DocumentObjectGroupPython] G4_POLYVINYL_BUTYRAL  # scripted group (container) (typed FeaturePython)
  Dunit = g/cm3
  Dvalue = 1.12
  Group = -> [C_element091,H_element083,O_element083]
  conduct = 2
  density = 1
  expand = 3
  formula = G4_POLYVINYL_BUTYRAL
  name = G4_POLYVINYL_BUTYRAL
  specific = 4
FEATURE [App::DocumentObjectGroupPython] C_element092  label="C_element : 050"  # scripted group (container) (typed FeaturePython)
  n = 2
  ref = C_element
FEATURE [App::DocumentObjectGroupPython] H_element084  label="H_element : 046"  # scripted group (container) (typed FeaturePython)
  n = 3
  ref = H_element
FEATURE [App::DocumentObjectGroupPython] Cl_element019  label="Cl_element : 009"  # scripted group (container) (typed FeaturePython)
  n = 1
  ref = Cl_element
FEATURE [App::DocumentObjectGroupPython] G4_POLYVINYL_CHLORIDE  # scripted group (container) (typed FeaturePython)
  Dunit = g/cm3
  Dvalue = 1.3
  Group = -> [C_element092,H_element084,Cl_element019]
  conduct = 2
  density = 1
  expand = 3
  formula = G4_POLYVINYL_CHLORIDE
  name = G4_POLYVINYL_CHLORIDE
  specific = 4
FEATURE [App::DocumentObjectGroupPython] C_element093  label="C_element : 051"  # scripted group (container) (typed FeaturePython)
  n = 2
  ref = C_element
FEATURE [App::DocumentObjectGroupPython] H_element085  label="H_element : 047"  # scripted group (container) (typed FeaturePython)
  n = 2
  ref = H_element
FEATURE [App::DocumentObjectGroupPython] Cl_element020  label="Cl_element : 010"  # scripted group (container) (typed FeaturePython)
  n = 2
  ref = Cl_element
FEATURE [App::DocumentObjectGroupPython] G4_POLYVINYLIDENE_CHLORIDE  # scripted group (container) (typed FeaturePython)
  Dunit = g/cm3
  Dvalue = 1.7
  Group = -> [C_element093,H_element085,Cl_element020]
  conduct = 2
  density = 1
  expand = 3
  formula = G4_POLYVINYLIDENE_CHLORIDE
  name = G4_POLYVINYLIDENE_CHLORIDE
  specific = 4
FEATURE [App::DocumentObjectGroupPython] C_element094  label="C_element : 052"  # scripted group (container) (typed FeaturePython)
  n = 2
  ref = C_element
FEATURE [App::DocumentObjectGroupPython] H_element086  label="H_element : 048"  # scripted group (container) (typed FeaturePython)
  n = 2
  ref = H_element
FEATURE [App::DocumentObjectGroupPython] F_element016  label="F_element : 007"  # scripted group (container) (typed FeaturePython)
  n = 2
  ref = F_element
FEATURE [App::DocumentObjectGroupPython] G4_POLYVINYLIDENE_FLUORIDE  # scripted group (container) (typed FeaturePython)
  Dunit = g/cm3
  Dvalue = 1.76
  Group = -> [C_element094,H_element086,F_element016]
  conduct = 2
  density = 1
  expand = 3
  formula = G4_POLYVINYLIDENE_FLUORIDE
  name = G4_POLYVINYLIDENE_FLUORIDE
  specific = 4
FEATURE [App::DocumentObjectGroupPython] C_element095  label="C_element : 053"  # scripted group (container) (typed FeaturePython)
  n = 6
  ref = C_element
FEATURE [App::DocumentObjectGroupPython] H_element087  label="H_element : 9"  # scripted group (container) (typed FeaturePython)
  n = 9
  ref = H_element
FEATURE [App::DocumentObjectGroupPython] N_element037  label="N_element : 016"  # scripted group (container) (typed FeaturePython)
  n = 1
  ref = N_element
FEATURE [App::DocumentObjectGroupPython] O_element084  label="O_element : 045"  # scripted group (container) (typed FeaturePython)
  n = 1
  ref = O_element
FEATURE [App::DocumentObjectGroupPython] G4_POLYVINYL_PYRROLIDONE  # scripted group (container) (typed FeaturePython)
  Dunit = g/cm3
  Dvalue = 1.25
  Group = -> [C_element095,H_element087,N_element037,O_element084]
  conduct = 2
  density = 1
  expand = 3
  formula = G4_POLYVINYL_PYRROLIDONE
  name = G4_POLYVINYL_PYRROLIDONE
  specific = 4
FEATURE [App::DocumentObjectGroupPython] K_element008  label="K_element : 1"  # scripted group (container) (typed FeaturePython)
  n = 1
  ref = K_element
FEATURE [App::DocumentObjectGroupPython] I_element006  label="I_element : 003"  # scripted group (container) (typed FeaturePython)
  n = 1
  ref = I_element
FEATURE [App::DocumentObjectGroupPython] G4_POTASSIUM_IODIDE  # scripted group (container) (typed FeaturePython)
  Dunit = g/cm3
  Dvalue = 3.13
  Group = -> [K_element008,I_element006]
  conduct = 2
  density = 1
  expand = 3
  formula = G4_POTASSIUM_IODIDE
  name = G4_POTASSIUM_IODIDE
  specific = 4
FEATURE [App::DocumentObjectGroupPython] K_element009  label="K_element : 2"  # scripted group (container) (typed FeaturePython)
  n = 2
  ref = K_element
FEATURE [App::DocumentObjectGroupPython] O_element085  label="O_element : 046"  # scripted group (container) (typed FeaturePython)
  n = 1
  ref = O_element
FEATURE [App::DocumentObjectGroupPython] G4_POTASSIUM_OXIDE  # scripted group (container) (typed FeaturePython)
  Dunit = g/cm3
  Dvalue = 2.32
  Group = -> [K_element009,O_element085]
  conduct = 2
  density = 1
  expand = 3
  formula = G4_POTASSIUM_OXIDE
  name = G4_POTASSIUM_OXIDE
  specific = 4
FEATURE [App::DocumentObjectGroupPython] C_element096  label="C_element : 054"  # scripted group (container) (typed FeaturePython)
  n = 3
  ref = C_element
FEATURE [App::DocumentObjectGroupPython] H_element088  label="H_element : 049"  # scripted group (container) (typed FeaturePython)
  n = 8
  ref = H_element
FEATURE [App::DocumentObjectGroupPython] G4_PROPANE  # scripted group (container) (typed FeaturePython)
  Dunit = g/cm3
  Dvalue = 0.00187939
  Group = -> [C_element096,H_element088]
  conduct = 2
  density = 1
  expand = 3
  formula = G4_PROPANE
  name = G4_PROPANE
  specific = 4
FEATURE [App::DocumentObjectGroupPython] C_element097  label="C_element : 055"  # scripted group (container) (typed FeaturePython)
  n = 3
  ref = C_element
FEATURE [App::DocumentObjectGroupPython] H_element089  label="H_element : 050"  # scripted group (container) (typed FeaturePython)
  n = 8
  ref = H_element
FEATURE [App::DocumentObjectGroupPython] G4_lPROPANE  # scripted group (container) (typed FeaturePython)
  Dunit = g/cm3
  Dvalue = 0.43
  Group = -> [C_element097,H_element089]
  conduct = 2
  density = 1
  expand = 3
  formula = G4_lPROPANE
  name = G4_lPROPANE
  specific = 4
FEATURE [App::DocumentObjectGroupPython] C_element098  label="C_element : 056"  # scripted group (container) (typed FeaturePython)
  n = 3
  ref = C_element
FEATURE [App::DocumentObjectGroupPython] H_element090  label="H_element : 051"  # scripted group (container) (typed FeaturePython)
  n = 8
  ref = H_element
FEATURE [App::DocumentObjectGroupPython] O_element086  label="O_element : 047"  # scripted group (container) (typed FeaturePython)
  n = 1
  ref = O_element
FEATURE [App::DocumentObjectGroupPython] G4_N_PROPYL_ALCOHOL  label="G4_N-PROPYL_ALCOHOL"  # scripted group (container) (typed FeaturePython)
  Dunit = g/cm3
  Dvalue = 0.8035
  Group = -> [C_element098,H_element090,O_element086]
  conduct = 2
  density = 1
  expand = 3
  formula = G4_N-PROPYL_ALCOHOL
  name = G4_N-PROPYL_ALCOHOL
  specific = 4
FEATURE [App::DocumentObjectGroupPython] C_element099  label="C_element : 057"  # scripted group (container) (typed FeaturePython)
  n = 5
  ref = C_element
FEATURE [App::DocumentObjectGroupPython] H_element091  label="H_element : 052"  # scripted group (container) (typed FeaturePython)
  n = 5
  ref = H_element
FEATURE [App::DocumentObjectGroupPython] N_element038  label="N_element : 017"  # scripted group (container) (typed FeaturePython)
  n = 1
  ref = N_element
FEATURE [App::DocumentObjectGroupPython] G4_PYRIDINE  # scripted group (container) (typed FeaturePython)
  Dunit = g/cm3
  Dvalue = 0.9819
  Group = -> [C_element099,H_element091,N_element038]
  conduct = 2
  density = 1
  expand = 3
  formula = G4_PYRIDINE
  name = G4_PYRIDINE
  specific = 4
FEATURE [App::DocumentObjectGroupPython] H_element092  label="H_element : 0.144"  # scripted group (container) (typed FeaturePython)
  n = 0.143711
FEATURE [App::DocumentObjectGroupPython] C_element100  label="C_element : 0.856"  # scripted group (container) (typed FeaturePython)
  n = 0.856289
FEATURE [App::DocumentObjectGroupPython] G4_RUBBER_BUTYL  # scripted group (container) (typed FeaturePython)
  Dunit = g/cm3
  Dvalue = 0.92
  Group = -> [H_element092,C_element100]
  conduct = 2
  density = 1
  expand = 3
  formula = G4_RUBBER_BUTYL
  name = G4_RUBBER_BUTYL
  specific = 4
FEATURE [App::DocumentObjectGroupPython] H_element093  label="H_element : 0.118"  # scripted group (container) (typed FeaturePython)
  n = 0.118371
FEATURE [App::DocumentObjectGroupPython] C_element101  label="C_element : 0.882"  # scripted group (container) (typed FeaturePython)
  n = 0.881629
FEATURE [App::DocumentObjectGroupPython] G4_RUBBER_NATURAL  # scripted group (container) (typed FeaturePython)
  Dunit = g/cm3
  Dvalue = 0.92
  Group = -> [H_element093,C_element101]
  conduct = 2
  density = 1
  expand = 3
  formula = G4_RUBBER_NATURAL
  name = G4_RUBBER_NATURAL
  specific = 4
FEATURE [App::DocumentObjectGroupPython] H_element094  label="H_element : 0.145"  # scripted group (container) (typed FeaturePython)
  n = 0.05692
FEATURE [App::DocumentObjectGroupPython] C_element102  label="C_element : 0.543"  # scripted group (container) (typed FeaturePython)
  n = 0.542646
FEATURE [App::DocumentObjectGroupPython] Cl_element021  label="Cl_element : 0.400"  # scripted group (container) (typed FeaturePython)
  n = 0.400434
FEATURE [App::DocumentObjectGroupPython] G4_RUBBER_NEOPRENE  # scripted group (container) (typed FeaturePython)
  Dunit = g/cm3
  Dvalue = 1.23
  Group = -> [H_element094,C_element102,Cl_element021]
  conduct = 2
  density = 1
  expand = 3
  formula = G4_RUBBER_NEOPRENE
  name = G4_RUBBER_NEOPRENE
  specific = 4
FEATURE [App::DocumentObjectGroupPython] Si_element006  label="Si_element : 1"  # scripted group (container) (typed FeaturePython)
  n = 1
  ref = Si_element
FEATURE [App::DocumentObjectGroupPython] O_element087  label="O_element : 048"  # scripted group (container) (typed FeaturePython)
  n = 2
  ref = O_element
FEATURE [App::DocumentObjectGroupPython] G4_SILICON_DIOXIDE  # scripted group (container) (typed FeaturePython)
  Dunit = g/cm3
  Dvalue = 2.32
  Group = -> [Si_element006,O_element087]
  conduct = 2
  density = 1
  expand = 3
  formula = G4_SILICON_DIOXIDE
  name = G4_SILICON_DIOXIDE
  specific = 4
FEATURE [App::DocumentObjectGroupPython] Ag_element002  label="Ag_element : 1"  # scripted group (container) (typed FeaturePython)
  n = 1
  ref = Ag_element
FEATURE [App::DocumentObjectGroupPython] Br_element005  label="Br_element : 003"  # scripted group (container) (typed FeaturePython)
  n = 1
  ref = Br_element
FEATURE [App::DocumentObjectGroupPython] G4_SILVER_BROMIDE  # scripted group (container) (typed FeaturePython)
  Dunit = g/cm3
  Dvalue = 6.473
  Group = -> [Ag_element002,Br_element005]
  conduct = 2
  density = 1
  expand = 3
  formula = G4_SILVER_BROMIDE
  name = G4_SILVER_BROMIDE
  specific = 4
FEATURE [App::DocumentObjectGroupPython] Ag_element003  label="Ag_element : 002"  # scripted group (container) (typed FeaturePython)
  n = 1
  ref = Ag_element
FEATURE [App::DocumentObjectGroupPython] Cl_element022  label="Cl_element : 011"  # scripted group (container) (typed FeaturePython)
  n = 1
  ref = Cl_element
FEATURE [App::DocumentObjectGroupPython] G4_SILVER_CHLORIDE  # scripted group (container) (typed FeaturePython)
  Dunit = g/cm3
  Dvalue = 5.56
  Group = -> [Ag_element003,Cl_element022]
  conduct = 2
  density = 1
  expand = 3
  formula = G4_SILVER_CHLORIDE
  name = G4_SILVER_CHLORIDE
  specific = 4
FEATURE [App::DocumentObjectGroupPython] Br_element006  label="Br_element : 0.423"  # scripted group (container) (typed FeaturePython)
  n = 0.422895
FEATURE [App::DocumentObjectGroupPython] Ag_element004  label="Ag_element : 0.574"  # scripted group (container) (typed FeaturePython)
  n = 0.573748
FEATURE [App::DocumentObjectGroupPython] I_element007  label="I_element : 0.649"  # scripted group (container) (typed FeaturePython)
  n = 0.003357
FEATURE [App::DocumentObjectGroupPython] G4_SILVER_HALIDES  # scripted group (container) (typed FeaturePython)
  Dunit = g/cm3
  Dvalue = 6.47
  Group = -> [Br_element006,Ag_element004,I_element007]
  conduct = 2
  density = 1
  expand = 3
  formula = G4_SILVER_HALIDES
  name = G4_SILVER_HALIDES
  specific = 4
FEATURE [App::DocumentObjectGroupPython] Ag_element005  label="Ag_element : 003"  # scripted group (container) (typed FeaturePython)
  n = 1
  ref = Ag_element
FEATURE [App::DocumentObjectGroupPython] I_element008  label="I_element : 004"  # scripted group (container) (typed FeaturePython)
  n = 1
  ref = I_element
FEATURE [App::DocumentObjectGroupPython] G4_SILVER_IODIDE  # scripted group (container) (typed FeaturePython)
  Dunit = g/cm3
  Dvalue = 6.01
  Group = -> [Ag_element005,I_element008]
  conduct = 2
  density = 1
  expand = 3
  formula = G4_SILVER_IODIDE
  name = G4_SILVER_IODIDE
  specific = 4
FEATURE [App::DocumentObjectGroupPython] H_element095  label="H_element : 0.100"  # scripted group (container) (typed FeaturePython)
  n = 0.1
FEATURE [App::DocumentObjectGroupPython] C_element103  label="C_element : 0.204"  # scripted group (container) (typed FeaturePython)
  n = 0.204
FEATURE [App::DocumentObjectGroupPython] N_element039  label="N_element : 0.759"  # scripted group (container) (typed FeaturePython)
  n = 0.042
FEATURE [App::DocumentObjectGroupPython] O_element088  label="O_element : 0.645"  # scripted group (container) (typed FeaturePython)
  n = 0.645
FEATURE [App::DocumentObjectGroupPython] Na_element013  label="Na_element : 0.100"  # scripted group (container) (typed FeaturePython)
  n = 0.002
FEATURE [App::DocumentObjectGroupPython] P_element009  label="P_element : 0.107"  # scripted group (container) (typed FeaturePython)
  n = 0.001
FEATURE [App::DocumentObjectGroupPython] S_element020  label="S_element : 0.021"  # scripted group (container) (typed FeaturePython)
  n = 0.002
FEATURE [App::DocumentObjectGroupPython] Cl_element023  label="Cl_element : 0.590"  # scripted group (container) (typed FeaturePython)
  n = 0.003
FEATURE [App::DocumentObjectGroupPython] K_element010  label="K_element : 0.001"  # scripted group (container) (typed FeaturePython)
  n = 0.001
FEATURE [App::DocumentObjectGroupPython] G4_SKIN_ICRP  # scripted group (container) (typed FeaturePython)
  Dunit = g/cm3
  Dvalue = 1.09
  Group = -> [H_element095,C_element103,N_element039,O_element088,Na_element013,P_element009,S_element020,Cl_element023,K_element010]
  conduct = 2
  density = 1
  expand = 3
  formula = G4_SKIN_ICRP
  name = G4_SKIN_ICRP
  specific = 4
FEATURE [App::DocumentObjectGroupPython] Na_element014  label="Na_element : 2"  # scripted group (container) (typed FeaturePython)
  n = 2
  ref = Na_element
FEATURE [App::DocumentObjectGroupPython] C_element104  label="C_element : 058"  # scripted group (container) (typed FeaturePython)
  n = 1
  ref = C_element
FEATURE [App::DocumentObjectGroupPython] O_element089  label="O_element : 049"  # scripted group (container) (typed FeaturePython)
  n = 3
  ref = O_element
FEATURE [App::DocumentObjectGroupPython] G4_SODIUM_CARBONATE  # scripted group (container) (typed FeaturePython)
  Dunit = g/cm3
  Dvalue = 2.532
  Group = -> [Na_element014,C_element104,O_element089]
  conduct = 2
  density = 1
  expand = 3
  formula = G4_SODIUM_CARBONATE
  name = G4_SODIUM_CARBONATE
  specific = 4
FEATURE [App::DocumentObjectGroupPython] Na_element015  label="Na_element : 1"  # scripted group (container) (typed FeaturePython)
  n = 1
  ref = Na_element
FEATURE [App::DocumentObjectGroupPython] I_element009  label="I_element : 005"  # scripted group (container) (typed FeaturePython)
  n = 1
  ref = I_element
FEATURE [App::DocumentObjectGroupPython] G4_SODIUM_IODIDE  # scripted group (container) (typed FeaturePython)
  Dunit = g/cm3
  Dvalue = 3.667
  Group = -> [Na_element015,I_element009]
  conduct = 2
  density = 1
  expand = 3
  formula = G4_SODIUM_IODIDE
  name = G4_SODIUM_IODIDE
  specific = 4
FEATURE [App::DocumentObjectGroupPython] Na_element016  label="Na_element : 003"  # scripted group (container) (typed FeaturePython)
  n = 2
  ref = Na_element
FEATURE [App::DocumentObjectGroupPython] O_element090  label="O_element : 050"  # scripted group (container) (typed FeaturePython)
  n = 1
  ref = O_element
FEATURE [App::DocumentObjectGroupPython] G4_SODIUM_MONOXIDE  # scripted group (container) (typed FeaturePython)
  Dunit = g/cm3
  Dvalue = 2.27
  Group = -> [Na_element016,O_element090]
  conduct = 2
  density = 1
  expand = 3
  formula = G4_SODIUM_MONOXIDE
  name = G4_SODIUM_MONOXIDE
  specific = 4
FEATURE [App::DocumentObjectGroupPython] Na_element017  label="Na_element : 004"  # scripted group (container) (typed FeaturePython)
  n = 1
  ref = Na_element
FEATURE [App::DocumentObjectGroupPython] N_element040  label="N_element : 018"  # scripted group (container) (typed FeaturePython)
  n = 1
  ref = N_element
FEATURE [App::DocumentObjectGroupPython] O_element091  label="O_element : 051"  # scripted group (container) (typed FeaturePython)
  n = 3
  ref = O_element
FEATURE [App::DocumentObjectGroupPython] G4_SODIUM_NITRATE  # scripted group (container) (typed FeaturePython)
  Dunit = g/cm3
  Dvalue = 2.261
  Group = -> [Na_element017,N_element040,O_element091]
  conduct = 2
  density = 1
  expand = 3
  formula = G4_SODIUM_NITRATE
  name = G4_SODIUM_NITRATE
  specific = 4
FEATURE [App::DocumentObjectGroupPython] C_element105  label="C_element : 059"  # scripted group (container) (typed FeaturePython)
  n = 14
  ref = C_element
FEATURE [App::DocumentObjectGroupPython] H_element096  label="H_element : 053"  # scripted group (container) (typed FeaturePython)
  n = 12
  ref = H_element
FEATURE [App::DocumentObjectGroupPython] G4_STILBENE  # scripted group (container) (typed FeaturePython)
  Dunit = g/cm3
  Dvalue = 0.9707
  Group = -> [C_element105,H_element096]
  conduct = 2
  density = 1
  expand = 3
  formula = G4_STILBENE
  name = G4_STILBENE
  specific = 4
FEATURE [App::DocumentObjectGroupPython] C_element106  label="C_element : 12"  # scripted group (container) (typed FeaturePython)
  n = 12
  ref = C_element
FEATURE [App::DocumentObjectGroupPython] H_element097  label="H_element : 22"  # scripted group (container) (typed FeaturePython)
  n = 22
  ref = H_element
FEATURE [App::DocumentObjectGroupPython] O_element092  label="O_element : 11"  # scripted group (container) (typed FeaturePython)
  n = 11
  ref = O_element
FEATURE [App::DocumentObjectGroupPython] G4_SUCROSE  # scripted group (container) (typed FeaturePython)
  Dunit = g/cm3
  Dvalue = 1.5805
  Group = -> [C_element106,H_element097,O_element092]
  conduct = 2
  density = 1
  expand = 3
  formula = G4_SUCROSE
  name = G4_SUCROSE
  specific = 4
FEATURE [App::DocumentObjectGroupPython] C_element107  label="C_element : 18"  # scripted group (container) (typed FeaturePython)
  n = 18
  ref = C_element
FEATURE [App::DocumentObjectGroupPython] H_element098  label="H_element : 054"  # scripted group (container) (typed FeaturePython)
  n = 14
  ref = H_element
FEATURE [App::DocumentObjectGroupPython] G4_TERPHENYL  # scripted group (container) (typed FeaturePython)
  Dunit = g/cm3
  Dvalue = 1.24
  Group = -> [C_element107,H_element098]
  conduct = 2
  density = 1
  expand = 3
  formula = G4_TERPHENYL
  name = G4_TERPHENYL
  specific = 4
FEATURE [App::DocumentObjectGroupPython] H_element099  label="H_element : 0.146"  # scripted group (container) (typed FeaturePython)
  n = 0.106
FEATURE [App::DocumentObjectGroupPython] C_element108  label="C_element : 0.883"  # scripted group (container) (typed FeaturePython)
  n = 0.099
FEATURE [App::DocumentObjectGroupPython] N_element041  label="N_element : 0.020"  # scripted group (container) (typed FeaturePython)
  n = 0.02
FEATURE [App::DocumentObjectGroupPython] O_element093  label="O_element : 0.766"  # scripted group (container) (typed FeaturePython)
  n = 0.766
FEATURE [App::DocumentObjectGroupPython] Na_element018  label="Na_element : 0.101"  # scripted group (container) (typed FeaturePython)
  n = 0.002
FEATURE [App::DocumentObjectGroupPython] P_element010  label="P_element : 0.108"  # scripted group (container) (typed FeaturePython)
  n = 0.001
FEATURE [App::DocumentObjectGroupPython] S_element021  label="S_element : 0.022"  # scripted group (container) (typed FeaturePython)
  n = 0.002
FEATURE [App::DocumentObjectGroupPython] Cl_element024  label="Cl_element : 0.002"  # scripted group (container) (typed FeaturePython)
  n = 0.002
FEATURE [App::DocumentObjectGroupPython] K_element011  label="K_element : 0.017"  # scripted group (container) (typed FeaturePython)
  n = 0.002
FEATURE [App::DocumentObjectGroupPython] G4_TESTIS_ICRP  # scripted group (container) (typed FeaturePython)
  Dunit = g/cm3
  Dvalue = 1.04
  Group = -> [H_element099,C_element108,N_element041,O_element093,Na_element018,P_element010,S_element021,Cl_element024,K_element011]
  conduct = 2
  density = 1
  expand = 3
  formula = G4_TESTIS_ICRP
  name = G4_TESTIS_ICRP
  specific = 4
FEATURE [App::DocumentObjectGroupPython] C_element109  label="C_element : 060"  # scripted group (container) (typed FeaturePython)
  n = 2
  ref = C_element
FEATURE [App::DocumentObjectGroupPython] Cl_element025  label="Cl_element : 012"  # scripted group (container) (typed FeaturePython)
  n = 4
  ref = Cl_element
FEATURE [App::DocumentObjectGroupPython] G4_TETRACHLOROETHYLENE  # scripted group (container) (typed FeaturePython)
  Dunit = g/cm3
  Dvalue = 1.625
  Group = -> [C_element109,Cl_element025]
  conduct = 2
  density = 1
  expand = 3
  formula = G4_TETRACHLOROETHYLENE
  name = G4_TETRACHLOROETHYLENE
  specific = 4
FEATURE [App::DocumentObjectGroupPython] Tl_element001  label="Tl_element : 1"  # scripted group (container) (typed FeaturePython)
  n = 1
  ref = Tl_element
FEATURE [App::DocumentObjectGroupPython] Cl_element026  label="Cl_element : 013"  # scripted group (container) (typed FeaturePython)
  n = 1
  ref = Cl_element
FEATURE [App::DocumentObjectGroupPython] G4_THALLIUM_CHLORIDE  # scripted group (container) (typed FeaturePython)
  Dunit = g/cm3
  Dvalue = 7.004
  Group = -> [Tl_element001,Cl_element026]
  conduct = 2
  density = 1
  expand = 3
  formula = G4_THALLIUM_CHLORIDE
  name = G4_THALLIUM_CHLORIDE
  specific = 4
FEATURE [App::DocumentObjectGroupPython] H_element100  label="H_element : 0.147"  # scripted group (container) (typed FeaturePython)
  n = 0.105
FEATURE [App::DocumentObjectGroupPython] C_element110  label="C_element : 0.256"  # scripted group (container) (typed FeaturePython)
  n = 0.256
FEATURE [App::DocumentObjectGroupPython] N_element042  label="N_element : 0.760"  # scripted group (container) (typed FeaturePython)
  n = 0.027
FEATURE [App::DocumentObjectGroupPython] O_element094  label="O_element : 0.602"  # scripted group (container) (typed FeaturePython)
  n = 0.602
FEATURE [App::DocumentObjectGroupPython] Na_element019  label="Na_element : 0.102"  # scripted group (container) (typed FeaturePython)
  n = 0.001
FEATURE [App::DocumentObjectGroupPython] P_element011  label="P_element : 0.109"  # scripted group (container) (typed FeaturePython)
  n = 0.002
FEATURE [App::DocumentObjectGroupPython] S_element022  label="S_element : 0.023"  # scripted group (container) (typed FeaturePython)
  n = 0.003
FEATURE [App::DocumentObjectGroupPython] Cl_element027  label="Cl_element : 0.591"  # scripted group (container) (typed FeaturePython)
  n = 0.002
FEATURE [App::DocumentObjectGroupPython] K_element012  label="K_element : 0.018"  # scripted group (container) (typed FeaturePython)
  n = 0.002
FEATURE [App::DocumentObjectGroupPython] G4_TISSUE_SOFT_ICRP  # scripted group (container) (typed FeaturePython)
  Dunit = g/cm3
  Dvalue = 1.03
  Group = -> [H_element100,C_element110,N_element042,O_element094,Na_element019,P_element011,S_element022,Cl_element027,K_element012]
  conduct = 2
  density = 1
  expand = 3
  formula = G4_TISSUE_SOFT_ICRP
  name = G4_TISSUE_SOFT_ICRP
  specific = 4
FEATURE [App::DocumentObjectGroupPython] H_element101  label="H_element : 0.148"  # scripted group (container) (typed FeaturePython)
  n = 0.101
FEATURE [App::DocumentObjectGroupPython] C_element111  label="C_element : 0.111"  # scripted group (container) (typed FeaturePython)
  n = 0.111
FEATURE [App::DocumentObjectGroupPython] N_element043  label="N_element : 0.026"  # scripted group (container) (typed FeaturePython)
  n = 0.026
FEATURE [App::DocumentObjectGroupPython] O_element095  label="O_element : 0.762"  # scripted group (container) (typed FeaturePython)
  n = 0.762
FEATURE [App::DocumentObjectGroupPython] G4_TISSUE_SOFT_ICRU_4  label="G4_TISSUE_SOFT_ICRU-4"  # scripted group (container) (typed FeaturePython)
  Dunit = g/cm3
  Dvalue = 1
  Group = -> [H_element101,C_element111,N_element043,O_element095]
  conduct = 2
  density = 1
  expand = 3
  formula = G4_TISSUE_SOFT_ICRU-4
  name = G4_TISSUE_SOFT_ICRU-4
  specific = 4
FEATURE [App::DocumentObjectGroupPython] H_element102  label="H_element : 0.149"  # scripted group (container) (typed FeaturePython)
  n = 0.101869
FEATURE [App::DocumentObjectGroupPython] C_element112  label="C_element : 0.456"  # scripted group (container) (typed FeaturePython)
  n = 0.456179
FEATURE [App::DocumentObjectGroupPython] N_element044  label="N_element : 0.761"  # scripted group (container) (typed FeaturePython)
  n = 0.035172
FEATURE [App::DocumentObjectGroupPython] O_element096  label="O_element : 0.407"  # scripted group (container) (typed FeaturePython)
  n = 0.40678
FEATURE [App::DocumentObjectGroupPython] G4_TISSUE_METHANE  label="G4_TISSUE-METHANE"  # scripted group (container) (typed FeaturePython)
  Dunit = g/cm3
  Dvalue = 0.00106409
  Group = -> [H_element102,C_element112,N_element044,O_element096]
  conduct = 2
  density = 1
  expand = 3
  formula = G4_TISSUE-METHANE
  name = G4_TISSUE-METHANE
  specific = 4
FEATURE [App::DocumentObjectGroupPython] H_element103  label="H_element : 0.103"  # scripted group (container) (typed FeaturePython)
  n = 0.102672
FEATURE [App::DocumentObjectGroupPython] C_element113  label="C_element : 0.569"  # scripted group (container) (typed FeaturePython)
  n = 0.56894
FEATURE [App::DocumentObjectGroupPython] N_element045  label="N_element : 0.762"  # scripted group (container) (typed FeaturePython)
  n = 0.035022
FEATURE [App::DocumentObjectGroupPython] O_element097  label="O_element : 0.293"  # scripted group (container) (typed FeaturePython)
  n = 0.293366
FEATURE [App::DocumentObjectGroupPython] G4_TISSUE_PROPANE  label="G4_TISSUE-PROPANE"  # scripted group (container) (typed FeaturePython)
  Dunit = g/cm3
  Dvalue = 0.00182628
  Group = -> [H_element103,C_element113,N_element045,O_element097]
  conduct = 2
  density = 1
  expand = 3
  formula = G4_TISSUE-PROPANE
  name = G4_TISSUE-PROPANE
  specific = 4
FEATURE [App::DocumentObjectGroupPython] Ti_element003  label="Ti_element : 1"  # scripted group (container) (typed FeaturePython)
  n = 1
  ref = Ti_element
FEATURE [App::DocumentObjectGroupPython] O_element098  label="O_element : 052"  # scripted group (container) (typed FeaturePython)
  n = 2
  ref = O_element
FEATURE [App::DocumentObjectGroupPython] G4_TITANIUM_DIOXIDE  # scripted group (container) (typed FeaturePython)
  Dunit = g/cm3
  Dvalue = 4.26
  Group = -> [Ti_element003,O_element098]
  conduct = 2
  density = 1
  expand = 3
  formula = G4_TITANIUM_DIOXIDE
  name = G4_TITANIUM_DIOXIDE
  specific = 4
FEATURE [App::DocumentObjectGroupPython] C_element114  label="C_element : 061"  # scripted group (container) (typed FeaturePython)
  n = 7
  ref = C_element
FEATURE [App::DocumentObjectGroupPython] H_element104  label="H_element : 055"  # scripted group (container) (typed FeaturePython)
  n = 8
  ref = H_element
FEATURE [App::DocumentObjectGroupPython] G4_TOLUENE  # scripted group (container) (typed FeaturePython)
  Dunit = g/cm3
  Dvalue = 0.8669
  Group = -> [C_element114,H_element104]
  conduct = 2
  density = 1
  expand = 3
  formula = G4_TOLUENE
  name = G4_TOLUENE
  specific = 4
FEATURE [App::DocumentObjectGroupPython] C_element115  label="C_element : 062"  # scripted group (container) (typed FeaturePython)
  n = 2
  ref = C_element
FEATURE [App::DocumentObjectGroupPython] H_element105  label="H_element : 056"  # scripted group (container) (typed FeaturePython)
  n = 1
  ref = H_element
FEATURE [App::DocumentObjectGroupPython] Cl_element028  label="Cl_element : 014"  # scripted group (container) (typed FeaturePython)
  n = 3
  ref = Cl_element
FEATURE [App::DocumentObjectGroupPython] G4_TRICHLOROETHYLENE  # scripted group (container) (typed FeaturePython)
  Dunit = g/cm3
  Dvalue = 1.46
  Group = -> [C_element115,H_element105,Cl_element028]
  conduct = 2
  density = 1
  expand = 3
  formula = G4_TRICHLOROETHYLENE
  name = G4_TRICHLOROETHYLENE
  specific = 4
FEATURE [App::DocumentObjectGroupPython] C_element116  label="C_element : 063"  # scripted group (container) (typed FeaturePython)
  n = 6
  ref = C_element
FEATURE [App::DocumentObjectGroupPython] H_element106  label="H_element : 15"  # scripted group (container) (typed FeaturePython)
  n = 15
  ref = H_element
FEATURE [App::DocumentObjectGroupPython] O_element099  label="O_element : 053"  # scripted group (container) (typed FeaturePython)
  n = 4
  ref = O_element
FEATURE [App::DocumentObjectGroupPython] P_element012  label="P_element : 1"  # scripted group (container) (typed FeaturePython)
  n = 1
  ref = P_element
FEATURE [App::DocumentObjectGroupPython] G4_TRIETHYL_PHOSPHATE  # scripted group (container) (typed FeaturePython)
  Dunit = g/cm3
  Dvalue = 1.07
  Group = -> [C_element116,H_element106,O_element099,P_element012]
  conduct = 2
  density = 1
  expand = 3
  formula = G4_TRIETHYL_PHOSPHATE
  name = G4_TRIETHYL_PHOSPHATE
  specific = 4
FEATURE [App::DocumentObjectGroupPython] W_element003  label="W_element : 003"  # scripted group (container) (typed FeaturePython)
  n = 1
  ref = W_element
FEATURE [App::DocumentObjectGroupPython] F_element017  label="F_element : 6"  # scripted group (container) (typed FeaturePython)
  n = 6
  ref = F_element
FEATURE [App::DocumentObjectGroupPython] G4_TUNGSTEN_HEXAFLUORIDE  # scripted group (container) (typed FeaturePython)
  Dunit = g/cm3
  Dvalue = 2.4
  Group = -> [W_element003,F_element017]
  conduct = 2
  density = 1
  expand = 3
  formula = G4_TUNGSTEN_HEXAFLUORIDE
  name = G4_TUNGSTEN_HEXAFLUORIDE
  specific = 4
FEATURE [App::DocumentObjectGroupPython] U_element001  label="U_element : 1"  # scripted group (container) (typed FeaturePython)
  n = 1
  ref = U_element
FEATURE [App::DocumentObjectGroupPython] C_element117  label="C_element : 064"  # scripted group (container) (typed FeaturePython)
  n = 2
  ref = C_element
FEATURE [App::DocumentObjectGroupPython] G4_URANIUM_DICARBIDE  # scripted group (container) (typed FeaturePython)
  Dunit = g/cm3
  Dvalue = 11.28
  Group = -> [U_element001,C_element117]
  conduct = 2
  density = 1
  expand = 3
  formula = G4_URANIUM_DICARBIDE
  name = G4_URANIUM_DICARBIDE
  specific = 4
FEATURE [App::DocumentObjectGroupPython] U_element002  label="U_element : 002"  # scripted group (container) (typed FeaturePython)
  n = 1
  ref = U_element
FEATURE [App::DocumentObjectGroupPython] C_element118  label="C_element : 065"  # scripted group (container) (typed FeaturePython)
  n = 1
  ref = C_element
FEATURE [App::DocumentObjectGroupPython] G4_URANIUM_MONOCARBIDE  # scripted group (container) (typed FeaturePython)
  Dunit = g/cm3
  Dvalue = 13.63
  Group = -> [U_element002,C_element118]
  conduct = 2
  density = 1
  expand = 3
  formula = G4_URANIUM_MONOCARBIDE
  name = G4_URANIUM_MONOCARBIDE
  specific = 4
FEATURE [App::DocumentObjectGroupPython] U_element003  label="U_element : 003"  # scripted group (container) (typed FeaturePython)
  n = 1
  ref = U_element
FEATURE [App::DocumentObjectGroupPython] O_element100  label="O_element : 054"  # scripted group (container) (typed FeaturePython)
  n = 2
  ref = O_element
FEATURE [App::DocumentObjectGroupPython] G4_URANIUM_OXIDE  # scripted group (container) (typed FeaturePython)
  Dunit = g/cm3
  Dvalue = 10.96
  Group = -> [U_element003,O_element100]
  conduct = 2
  density = 1
  expand = 3
  formula = G4_URANIUM_OXIDE
  name = G4_URANIUM_OXIDE
  specific = 4
FEATURE [App::DocumentObjectGroupPython] C_element119  label="C_element : 066"  # scripted group (container) (typed FeaturePython)
  n = 1
  ref = C_element
FEATURE [App::DocumentObjectGroupPython] H_element107  label="H_element : 057"  # scripted group (container) (typed FeaturePython)
  n = 4
  ref = H_element
FEATURE [App::DocumentObjectGroupPython] N_element046  label="N_element : 019"  # scripted group (container) (typed FeaturePython)
  n = 2
  ref = N_element
FEATURE [App::DocumentObjectGroupPython] O_element101  label="O_element : 055"  # scripted group (container) (typed FeaturePython)
  n = 1
  ref = O_element
FEATURE [App::DocumentObjectGroupPython] G4_UREA  # scripted group (container) (typed FeaturePython)
  Dunit = g/cm3
  Dvalue = 1.323
  Group = -> [C_element119,H_element107,N_element046,O_element101]
  conduct = 2
  density = 1
  expand = 3
  formula = G4_UREA
  name = G4_UREA
  specific = 4
FEATURE [App::DocumentObjectGroupPython] C_element120  label="C_element : 067"  # scripted group (container) (typed FeaturePython)
  n = 5
  ref = C_element
FEATURE [App::DocumentObjectGroupPython] H_element108  label="H_element : 058"  # scripted group (container) (typed FeaturePython)
  n = 11
  ref = H_element
FEATURE [App::DocumentObjectGroupPython] N_element047  label="N_element : 020"  # scripted group (container) (typed FeaturePython)
  n = 1
  ref = N_element
FEATURE [App::DocumentObjectGroupPython] O_element102  label="O_element : 056"  # scripted group (container) (typed FeaturePython)
  n = 2
  ref = O_element
FEATURE [App::DocumentObjectGroupPython] G4_VALINE  # scripted group (container) (typed FeaturePython)
  Dunit = g/cm3
  Dvalue = 1.23
  Group = -> [C_element120,H_element108,N_element047,O_element102]
  conduct = 2
  density = 1
  expand = 3
  formula = G4_VALINE
  name = G4_VALINE
  specific = 4
FEATURE [App::DocumentObjectGroupPython] H_element109  label="H_element : 0.009"  # scripted group (container) (typed FeaturePython)
  n = 0.009417
FEATURE [App::DocumentObjectGroupPython] C_element121  label="C_element : 0.281"  # scripted group (container) (typed FeaturePython)
  n = 0.280555
FEATURE [App::DocumentObjectGroupPython] F_element018  label="F_element : 0.710"  # scripted group (container) (typed FeaturePython)
  n = 0.710028
FEATURE [App::DocumentObjectGroupPython] G4_VITON  # scripted group (container) (typed FeaturePython)
  Dunit = g/cm3
  Dvalue = 1.8
  Group = -> [H_element109,C_element121,F_element018]
  conduct = 2
  density = 1
  expand = 3
  formula = G4_VITON
  name = G4_VITON
  specific = 4
FEATURE [App::DocumentObjectGroupPython] H_element110  label="H_element : 059"  # scripted group (container) (typed FeaturePython)
  n = 2
  ref = H_element
FEATURE [App::DocumentObjectGroupPython] O_element103  label="O_element : 057"  # scripted group (container) (typed FeaturePython)
  n = 1
  ref = O_element
FEATURE [App::DocumentObjectGroupPython] G4_WATER  # scripted group (container) (typed FeaturePython)
  Dunit = g/cm3
  Dvalue = 1
  Group = -> [H_element110,O_element103]
  conduct = 2
  density = 1
  expand = 3
  formula = G4_WATER
  name = G4_WATER
  specific = 4
FEATURE [App::DocumentObjectGroupPython] H_element111  label="H_element : 060"  # scripted group (container) (typed FeaturePython)
  n = 2
  ref = H_element
FEATURE [App::DocumentObjectGroupPython] O_element104  label="O_element : 058"  # scripted group (container) (typed FeaturePython)
  n = 1
  ref = O_element
FEATURE [App::DocumentObjectGroupPython] G4_WATER_VAPOR  # scripted group (container) (typed FeaturePython)
  Dunit = g/cm3
  Dvalue = 0.000756182
  Group = -> [H_element111,O_element104]
  conduct = 2
  density = 1
  expand = 3
  formula = G4_WATER_VAPOR
  name = G4_WATER_VAPOR
  specific = 4
FEATURE [App::DocumentObjectGroupPython] C_element122  label="C_element : 068"  # scripted group (container) (typed FeaturePython)
  n = 8
  ref = C_element
FEATURE [App::DocumentObjectGroupPython] H_element112  label="H_element : 061"  # scripted group (container) (typed FeaturePython)
  n = 10
  ref = H_element
FEATURE [App::DocumentObjectGroupPython] G4_XYLENE  # scripted group (container) (typed FeaturePython)
  Dunit = g/cm3
  Dvalue = 0.87
  Group = -> [C_element122,H_element112]
  conduct = 2
  density = 1
  expand = 3
  formula = G4_XYLENE
  name = G4_XYLENE
  specific = 4
FEATURE [App::DocumentObjectGroupPython] C_element123  label="C_element : 069"  # scripted group (container) (typed FeaturePython)
  n = 1
  ref = C_element
FEATURE [App::DocumentObjectGroupPython] G4_GRAPHITE  # scripted group (container) (typed FeaturePython)
  Dunit = g/cm3
  Dvalue = 2.21
  Group = -> [C_element123]
  conduct = 2
  density = 1
  expand = 3
  formula = G4_GRAPHITE
  name = G4_GRAPHITE
  specific = 4
FEATURE [App::DocumentObjectGroupPython] NIST  # scripted group (container) (typed FeaturePython)
  Group = -> [G4_A_150_TISSUE,G4_ACETONE,G4_ACETYLENE,G4_ADENINE,G4_ADIPOSE_TISSUE_ICRP,G4_AIR,G4_ALANINE,G4_ALUMINUM_OXIDE,G4_AMBER,G4_AMMONIA,G4_ANILINE,G4_ANTHRACENE,G4_B_100_BONE,G4_BAKELITE,G4_BARIUM_FLUORIDE,G4_BARIUM_SULFATE,G4_BENZENE,G4_BERYLLIUM_OXIDE,G4_BGO,G4_BLOOD_ICRP,G4_BONE_COMPACT_ICRU,G4_BONE_CORTICAL_ICRP,G4_BORON_CARBIDE,G4_BORON_OXIDE,G4_BRAIN_ICRP,G4_BUTANE,G4_N_BUTYL_ALCOHOL,G4_C_552,+152 more]
FEATURE [App::DocumentObjectGroupPython] H_element113  label="H_element : 062"  # scripted group (container) (typed FeaturePython)
  n = 1
  ref = H_element
FEATURE [App::DocumentObjectGroupPython] G4_H  # scripted group (container) (typed FeaturePython)
  Dunit = g/cm3
  Dvalue = 8.3748e-05
  Group = -> [H_element113]
  conduct = 2
  density = 1
  expand = 3
  formula = H
  name = G4_H
  specific = 4
FEATURE [App::DocumentObjectGroupPython] He_element001  label="He_element : 1"  # scripted group (container) (typed FeaturePython)
  n = 1
  ref = He_element
FEATURE [App::DocumentObjectGroupPython] G4_He  # scripted group (container) (typed FeaturePython)
  Dunit = g/cm3
  Dvalue = 0.000166322
  Group = -> [He_element001]
  conduct = 2
  density = 1
  expand = 3
  formula = He
  name = G4_He
  specific = 4
FEATURE [App::DocumentObjectGroupPython] Li_element008  label="Li_element : 008"  # scripted group (container) (typed FeaturePython)
  n = 1
  ref = Li_element
FEATURE [App::DocumentObjectGroupPython] G4_Li  # scripted group (container) (typed FeaturePython)
  Dunit = g/cm3
  Dvalue = 0.534
  Group = -> [Li_element008]
  conduct = 2
  density = 1
  expand = 3
  formula = Li
  name = G4_Li
  specific = 4
FEATURE [App::DocumentObjectGroupPython] Be_element002  label="Be_element : 002"  # scripted group (container) (typed FeaturePython)
  n = 1
  ref = Be_element
FEATURE [App::DocumentObjectGroupPython] G4_Be  # scripted group (container) (typed FeaturePython)
  Dunit = g/cm3
  Dvalue = 1.848
  Group = -> [Be_element002]
  conduct = 2
  density = 1
  expand = 3
  formula = Be
  name = G4_Be
  specific = 4
FEATURE [App::DocumentObjectGroupPython] B_element007  label="B_element : 007"  # scripted group (container) (typed FeaturePython)
  n = 1
  ref = B_element
FEATURE [App::DocumentObjectGroupPython] G4_B  # scripted group (container) (typed FeaturePython)
  Dunit = g/cm3
  Dvalue = 2.37
  Group = -> [B_element007]
  conduct = 2
  density = 1
  expand = 3
  formula = B
  name = G4_B
  specific = 4
FEATURE [App::DocumentObjectGroupPython] C_element124  label="C_element : 070"  # scripted group (container) (typed FeaturePython)
  n = 1
  ref = C_element
FEATURE [App::DocumentObjectGroupPython] G4_C  # scripted group (container) (typed FeaturePython)
  Dunit = g/cm3
  Dvalue = 2
  Group = -> [C_element124]
  conduct = 2
  density = 1
  expand = 3
  formula = C
  name = G4_C
  specific = 4
FEATURE [App::DocumentObjectGroupPython] N_element048  label="N_element : 021"  # scripted group (container) (typed FeaturePython)
  n = 1
  ref = N_element
FEATURE [App::DocumentObjectGroupPython] G4_N  # scripted group (container) (typed FeaturePython)
  Dunit = g/cm3
  Dvalue = 0.0011652
  Group = -> [N_element048]
  conduct = 2
  density = 1
  expand = 3
  formula = N
  name = G4_N
  specific = 4
FEATURE [App::DocumentObjectGroupPython] O_element105  label="O_element : 059"  # scripted group (container) (typed FeaturePython)
  n = 1
  ref = O_element
FEATURE [App::DocumentObjectGroupPython] G4_O  # scripted group (container) (typed FeaturePython)
  Dunit = g/cm3
  Dvalue = 0.00133151
  Group = -> [O_element105]
  conduct = 2
  density = 1
  expand = 3
  formula = O
  name = G4_O
  specific = 4
FEATURE [App::DocumentObjectGroupPython] F_element019  label="F_element : 008"  # scripted group (container) (typed FeaturePython)
  n = 1
  ref = F_element
FEATURE [App::DocumentObjectGroupPython] G4_F  # scripted group (container) (typed FeaturePython)
  Dunit = g/cm3
  Dvalue = 0.00158029
  Group = -> [F_element019]
  conduct = 2
  density = 1
  expand = 3
  formula = F
  name = G4_F
  specific = 4
FEATURE [App::DocumentObjectGroupPython] Ne_element001  label="Ne_element : 1"  # scripted group (container) (typed FeaturePython)
  n = 1
  ref = Ne_element
FEATURE [App::DocumentObjectGroupPython] G4_Ne  # scripted group (container) (typed FeaturePython)
  Dunit = g/cm3
  Dvalue = 0.000838505
  Group = -> [Ne_element001]
  conduct = 2
  density = 1
  expand = 3
  formula = Ne
  name = G4_Ne
  specific = 4
FEATURE [App::DocumentObjectGroupPython] Na_element020  label="Na_element : 005"  # scripted group (container) (typed FeaturePython)
  n = 1
  ref = Na_element
FEATURE [App::DocumentObjectGroupPython] G4_Na  # scripted group (container) (typed FeaturePython)
  Dunit = g/cm3
  Dvalue = 0.971
  Group = -> [Na_element020]
  conduct = 2
  density = 1
  expand = 3
  formula = Na
  name = G4_Na
  specific = 4
FEATURE [App::DocumentObjectGroupPython] Mg_element011  label="Mg_element : 005"  # scripted group (container) (typed FeaturePython)
  n = 1
  ref = Mg_element
FEATURE [App::DocumentObjectGroupPython] G4_Mg  # scripted group (container) (typed FeaturePython)
  Dunit = g/cm3
  Dvalue = 1.74
  Group = -> [Mg_element011]
  conduct = 2
  density = 1
  expand = 3
  formula = Mg
  name = G4_Mg
  specific = 4
FEATURE [App::DocumentObjectGroupPython] Al_element004  label="Al_element : 1"  # scripted group (container) (typed FeaturePython)
  n = 1
  ref = Al_element
FEATURE [App::DocumentObjectGroupPython] G4_Al  # scripted group (container) (typed FeaturePython)
  Dunit = g/cm3
  Dvalue = 2.699
  Group = -> [Al_element004]
  conduct = 2
  density = 1
  expand = 3
  formula = Al
  name = G4_Al
  specific = 4
FEATURE [App::DocumentObjectGroupPython] Si_element007  label="Si_element : 002"  # scripted group (container) (typed FeaturePython)
  n = 1
  ref = Si_element
FEATURE [App::DocumentObjectGroupPython] G4_Si  # scripted group (container) (typed FeaturePython)
  Dunit = g/cm3
  Dvalue = 2.33
  Group = -> [Si_element007]
  conduct = 2
  density = 1
  expand = 3
  formula = Si
  name = G4_Si
  specific = 4
FEATURE [App::DocumentObjectGroupPython] P_element013  label="P_element : 002"  # scripted group (container) (typed FeaturePython)
  n = 1
  ref = P_element
FEATURE [App::DocumentObjectGroupPython] G4_P  # scripted group (container) (typed FeaturePython)
  Dunit = g/cm3
  Dvalue = 2.2
  Group = -> [P_element013]
  conduct = 2
  density = 1
  expand = 3
  formula = P
  name = G4_P
  specific = 4
FEATURE [App::DocumentObjectGroupPython] S_element023  label="S_element : 007"  # scripted group (container) (typed FeaturePython)
  n = 1
  ref = S_element
FEATURE [App::DocumentObjectGroupPython] G4_S  # scripted group (container) (typed FeaturePython)
  Dunit = g/cm3
  Dvalue = 2
  Group = -> [S_element023]
  conduct = 2
  density = 1
  expand = 3
  formula = S
  name = G4_S
  specific = 4
FEATURE [App::DocumentObjectGroupPython] Cl_element029  label="Cl_element : 015"  # scripted group (container) (typed FeaturePython)
  n = 1
  ref = Cl_element
FEATURE [App::DocumentObjectGroupPython] G4_Cl  # scripted group (container) (typed FeaturePython)
  Dunit = g/cm3
  Dvalue = 0.00299473
  Group = -> [Cl_element029]
  conduct = 2
  density = 1
  expand = 3
  formula = Cl
  name = G4_Cl
  specific = 4
FEATURE [App::DocumentObjectGroupPython] Ar_element002  label="Ar_element : 1"  # scripted group (container) (typed FeaturePython)
  n = 1
  ref = Ar_element
FEATURE [App::DocumentObjectGroupPython] G4_Ar  # scripted group (container) (typed FeaturePython)
  Dunit = g/cm3
  Dvalue = 0.00166201
  Group = -> [Ar_element002]
  conduct = 2
  density = 1
  expand = 3
  formula = Ar
  name = G4_Ar
  specific = 4
FEATURE [App::DocumentObjectGroupPython] K_element013  label="K_element : 003"  # scripted group (container) (typed FeaturePython)
  n = 1
  ref = K_element
FEATURE [App::DocumentObjectGroupPython] G4_K  # scripted group (container) (typed FeaturePython)
  Dunit = g/cm3
  Dvalue = 0.862
  Group = -> [K_element013]
  conduct = 2
  density = 1
  expand = 3
  formula = K
  name = G4_K
  specific = 4
FEATURE [App::DocumentObjectGroupPython] Ca_element014  label="Ca_element : 007"  # scripted group (container) (typed FeaturePython)
  n = 1
  ref = Ca_element
FEATURE [App::DocumentObjectGroupPython] G4_Ca  # scripted group (container) (typed FeaturePython)
  Dunit = g/cm3
  Dvalue = 1.55
  Group = -> [Ca_element014]
  conduct = 2
  density = 1
  expand = 3
  formula = Ca
  name = G4_Ca
  specific = 4
FEATURE [App::DocumentObjectGroupPython] Sc_element001  label="Sc_element : 1"  # scripted group (container) (typed FeaturePython)
  n = 1
  ref = Sc_element
FEATURE [App::DocumentObjectGroupPython] G4_Sc  # scripted group (container) (typed FeaturePython)
  Dunit = g/cm3
  Dvalue = 2.989
  Group = -> [Sc_element001]
  conduct = 2
  density = 1
  expand = 3
  formula = Sc
  name = G4_Sc
  specific = 4
FEATURE [App::DocumentObjectGroupPython] Ti_element004  label="Ti_element : 002"  # scripted group (container) (typed FeaturePython)
  n = 1
  ref = Ti_element
FEATURE [App::DocumentObjectGroupPython] G4_Ti  # scripted group (container) (typed FeaturePython)
  Dunit = g/cm3
  Dvalue = 4.54
  Group = -> [Ti_element004]
  conduct = 2
  density = 1
  expand = 3
  formula = Ti
  name = G4_Ti
  specific = 4
FEATURE [App::DocumentObjectGroupPython] V_element001  label="V_element : 1"  # scripted group (container) (typed FeaturePython)
  n = 1
  ref = V_element
FEATURE [App::DocumentObjectGroupPython] G4_V  # scripted group (container) (typed FeaturePython)
  Dunit = g/cm3
  Dvalue = 6.11
  Group = -> [V_element001]
  conduct = 2
  density = 1
  expand = 3
  formula = V
  name = G4_V
  specific = 4
FEATURE [App::DocumentObjectGroupPython] Cr_element001  label="Cr_element : 1"  # scripted group (container) (typed FeaturePython)
  n = 1
  ref = Cr_element
FEATURE [App::DocumentObjectGroupPython] G4_Cr  # scripted group (container) (typed FeaturePython)
  Dunit = g/cm3
  Dvalue = 7.18
  Group = -> [Cr_element001]
  conduct = 2
  density = 1
  expand = 3
  formula = Cr
  name = G4_Cr
  specific = 4
FEATURE [App::DocumentObjectGroupPython] Mn_element001  label="Mn_element : 1"  # scripted group (container) (typed FeaturePython)
  n = 1
  ref = Mn_element
FEATURE [App::DocumentObjectGroupPython] G4_Mn  # scripted group (container) (typed FeaturePython)
  Dunit = g/cm3
  Dvalue = 7.44
  Group = -> [Mn_element001]
  conduct = 2
  density = 1
  expand = 3
  formula = Mn
  name = G4_Mn
  specific = 4
FEATURE [App::DocumentObjectGroupPython] Fe_element007  label="Fe_element : 004"  # scripted group (container) (typed FeaturePython)
  n = 1
  ref = Fe_element
FEATURE [App::DocumentObjectGroupPython] G4_Fe  # scripted group (container) (typed FeaturePython)
  Dunit = g/cm3
  Dvalue = 7.874
  Group = -> [Fe_element007]
  conduct = 2
  density = 1
  expand = 3
  formula = Fe
  name = G4_Fe
  specific = 4
FEATURE [App::DocumentObjectGroupPython] Co_element001  label="Co_element : 1"  # scripted group (container) (typed FeaturePython)
  n = 1
  ref = Co_element
FEATURE [App::DocumentObjectGroupPython] G4_Co  # scripted group (container) (typed FeaturePython)
  Dunit = g/cm3
  Dvalue = 8.9
  Group = -> [Co_element001]
  conduct = 2
  density = 1
  expand = 3
  formula = Co
  name = G4_Co
  specific = 4
FEATURE [App::DocumentObjectGroupPython] Ni_element001  label="Ni_element : 1"  # scripted group (container) (typed FeaturePython)
  n = 1
  ref = Ni_element
FEATURE [App::DocumentObjectGroupPython] G4_Ni  # scripted group (container) (typed FeaturePython)
  Dunit = g/cm3
  Dvalue = 8.902
  Group = -> [Ni_element001]
  conduct = 2
  density = 1
  expand = 3
  formula = Ni
  name = G4_Ni
  specific = 4
FEATURE [App::DocumentObjectGroupPython] Cu_element001  label="Cu_element : 1"  # scripted group (container) (typed FeaturePython)
  n = 1
  ref = Cu_element
FEATURE [App::DocumentObjectGroupPython] G4_Cu  # scripted group (container) (typed FeaturePython)
  Dunit = g/cm3
  Dvalue = 8.96
  Group = -> [Cu_element001]
  conduct = 2
  density = 1
  expand = 3
  formula = Cu
  name = G4_Cu
  specific = 4
FEATURE [App::DocumentObjectGroupPython] Zn_element001  label="Zn_element : 1"  # scripted group (container) (typed FeaturePython)
  n = 1
  ref = Zn_element
FEATURE [App::DocumentObjectGroupPython] G4_Zn  # scripted group (container) (typed FeaturePython)
  Dunit = g/cm3
  Dvalue = 7.133
  Group = -> [Zn_element001]
  conduct = 2
  density = 1
  expand = 3
  formula = Zn
  name = G4_Zn
  specific = 4
FEATURE [App::DocumentObjectGroupPython] Ga_element002  label="Ga_element : 002"  # scripted group (container) (typed FeaturePython)
  n = 1
  ref = Ga_element
FEATURE [App::DocumentObjectGroupPython] G4_Ga  # scripted group (container) (typed FeaturePython)
  Dunit = g/cm3
  Dvalue = 5.904
  Group = -> [Ga_element002]
  conduct = 2
  density = 1
  expand = 3
  formula = Ga
  name = G4_Ga
  specific = 4
FEATURE [App::DocumentObjectGroupPython] Ge_element002  label="Ge_element : 1"  # scripted group (container) (typed FeaturePython)
  n = 1
  ref = Ge_element
FEATURE [App::DocumentObjectGroupPython] G4_Ge  # scripted group (container) (typed FeaturePython)
  Dunit = g/cm3
  Dvalue = 5.323
  Group = -> [Ge_element002]
  conduct = 2
  density = 1
  expand = 3
  formula = Ge
  name = G4_Ge
  specific = 4
FEATURE [App::DocumentObjectGroupPython] As_element003  label="As_element : 002"  # scripted group (container) (typed FeaturePython)
  n = 1
  ref = As_element
FEATURE [App::DocumentObjectGroupPython] G4_As  # scripted group (container) (typed FeaturePython)
  Dunit = g/cm3
  Dvalue = 5.73
  Group = -> [As_element003]
  conduct = 2
  density = 1
  expand = 3
  formula = As
  name = G4_As
  specific = 4
FEATURE [App::DocumentObjectGroupPython] Se_element001  label="Se_element : 1"  # scripted group (container) (typed FeaturePython)
  n = 1
  ref = Se_element
FEATURE [App::DocumentObjectGroupPython] G4_Se  # scripted group (container) (typed FeaturePython)
  Dunit = g/cm3
  Dvalue = 4.5
  Group = -> [Se_element001]
  conduct = 2
  density = 1
  expand = 3
  formula = Se
  name = G4_Se
  specific = 4
FEATURE [App::DocumentObjectGroupPython] Br_element007  label="Br_element : 004"  # scripted group (container) (typed FeaturePython)
  n = 1
  ref = Br_element
FEATURE [App::DocumentObjectGroupPython] G4_Br  # scripted group (container) (typed FeaturePython)
  Dunit = g/cm3
  Dvalue = 0.0070721
  Group = -> [Br_element007]
  conduct = 2
  density = 1
  expand = 3
  formula = Br
  name = G4_Br
  specific = 4
FEATURE [App::DocumentObjectGroupPython] Kr_element001  label="Kr_element : 1"  # scripted group (container) (typed FeaturePython)
  n = 1
  ref = Kr_element
FEATURE [App::DocumentObjectGroupPython] G4_Kr  # scripted group (container) (typed FeaturePython)
  Dunit = g/cm3
  Dvalue = 0.00347832
  Group = -> [Kr_element001]
  conduct = 2
  density = 1
  expand = 3
  formula = Kr
  name = G4_Kr
  specific = 4
FEATURE [App::DocumentObjectGroupPython] Rb_element001  label="Rb_element : 1"  # scripted group (container) (typed FeaturePython)
  n = 1
  ref = Rb_element
FEATURE [App::DocumentObjectGroupPython] G4_Rb  # scripted group (container) (typed FeaturePython)
  Dunit = g/cm3
  Dvalue = 1.532
  Group = -> [Rb_element001]
  conduct = 2
  density = 1
  expand = 3
  formula = Rb
  name = G4_Rb
  specific = 4
FEATURE [App::DocumentObjectGroupPython] Sr_element001  label="Sr_element : 1"  # scripted group (container) (typed FeaturePython)
  n = 1
  ref = Sr_element
FEATURE [App::DocumentObjectGroupPython] G4_Sr  # scripted group (container) (typed FeaturePython)
  Dunit = g/cm3
  Dvalue = 2.54
  Group = -> [Sr_element001]
  conduct = 2
  density = 1
  expand = 3
  formula = Sr
  name = G4_Sr
  specific = 4
FEATURE [App::DocumentObjectGroupPython] Y_element001  label="Y_element : 1"  # scripted group (container) (typed FeaturePython)
  n = 1
  ref = Y_element
FEATURE [App::DocumentObjectGroupPython] G4_Y  # scripted group (container) (typed FeaturePython)
  Dunit = g/cm3
  Dvalue = 4.469
  Group = -> [Y_element001]
  conduct = 2
  density = 1
  expand = 3
  formula = Y
  name = G4_Y
  specific = 4
FEATURE [App::DocumentObjectGroupPython] Zr_element001  label="Zr_element : 1"  # scripted group (container) (typed FeaturePython)
  n = 1
  ref = Zr_element
FEATURE [App::DocumentObjectGroupPython] G4_Zr  # scripted group (container) (typed FeaturePython)
  Dunit = g/cm3
  Dvalue = 6.506
  Group = -> [Zr_element001]
  conduct = 2
  density = 1
  expand = 3
  formula = Zr
  name = G4_Zr
  specific = 4
FEATURE [App::DocumentObjectGroupPython] Nb_element001  label="Nb_element : 1"  # scripted group (container) (typed FeaturePython)
  n = 1
  ref = Nb_element
FEATURE [App::DocumentObjectGroupPython] G4_Nb  # scripted group (container) (typed FeaturePython)
  Dunit = g/cm3
  Dvalue = 8.57
  Group = -> [Nb_element001]
  conduct = 2
  density = 1
  expand = 3
  formula = Nb
  name = G4_Nb
  specific = 4
FEATURE [App::DocumentObjectGroupPython] Mo_element001  label="Mo_element : 1"  # scripted group (container) (typed FeaturePython)
  n = 1
  ref = Mo_element
FEATURE [App::DocumentObjectGroupPython] G4_Mo  # scripted group (container) (typed FeaturePython)
  Dunit = g/cm3
  Dvalue = 10.22
  Group = -> [Mo_element001]
  conduct = 2
  density = 1
  expand = 3
  formula = Mo
  name = G4_Mo
  specific = 4
FEATURE [App::DocumentObjectGroupPython] Tc_element001  label="Tc_element : 1"  # scripted group (container) (typed FeaturePython)
  n = 1
  ref = Tc_element
FEATURE [App::DocumentObjectGroupPython] G4_Tc  # scripted group (container) (typed FeaturePython)
  Dunit = g/cm3
  Dvalue = 11.5
  Group = -> [Tc_element001]
  conduct = 2
  density = 1
  expand = 3
  formula = Tc
  name = G4_Tc
  specific = 4
FEATURE [App::DocumentObjectGroupPython] Ru_element001  label="Ru_element : 1"  # scripted group (container) (typed FeaturePython)
  n = 1
  ref = Ru_element
FEATURE [App::DocumentObjectGroupPython] G4_Ru  # scripted group (container) (typed FeaturePython)
  Dunit = g/cm3
  Dvalue = 12.41
  Group = -> [Ru_element001]
  conduct = 2
  density = 1
  expand = 3
  formula = Ru
  name = G4_Ru
  specific = 4
FEATURE [App::DocumentObjectGroupPython] Rh_element001  label="Rh_element : 1"  # scripted group (container) (typed FeaturePython)
  n = 1
  ref = Rh_element
FEATURE [App::DocumentObjectGroupPython] G4_Rh  # scripted group (container) (typed FeaturePython)
  Dunit = g/cm3
  Dvalue = 12.41
  Group = -> [Rh_element001]
  conduct = 2
  density = 1
  expand = 3
  formula = Rh
  name = G4_Rh
  specific = 4
FEATURE [App::DocumentObjectGroupPython] Pd_element001  label="Pd_element : 1"  # scripted group (container) (typed FeaturePython)
  n = 1
  ref = Pd_element
FEATURE [App::DocumentObjectGroupPython] G4_Pd  # scripted group (container) (typed FeaturePython)
  Dunit = g/cm3
  Dvalue = 12.02
  Group = -> [Pd_element001]
  conduct = 2
  density = 1
  expand = 3
  formula = Pd
  name = G4_Pd
  specific = 4
FEATURE [App::DocumentObjectGroupPython] Ag_element006  label="Ag_element : 004"  # scripted group (container) (typed FeaturePython)
  n = 1
  ref = Ag_element
FEATURE [App::DocumentObjectGroupPython] G4_Ag  # scripted group (container) (typed FeaturePython)
  Dunit = g/cm3
  Dvalue = 10.5
  Group = -> [Ag_element006]
  conduct = 2
  density = 1
  expand = 3
  formula = Ag
  name = G4_Ag
  specific = 4
FEATURE [App::DocumentObjectGroupPython] Cd_element003  label="Cd_element : 003"  # scripted group (container) (typed FeaturePython)
  n = 1
  ref = Cd_element
FEATURE [App::DocumentObjectGroupPython] G4_Cd  # scripted group (container) (typed FeaturePython)
  Dunit = g/cm3
  Dvalue = 8.65
  Group = -> [Cd_element003]
  conduct = 2
  density = 1
  expand = 3
  formula = Cd
  name = G4_Cd
  specific = 4
FEATURE [App::DocumentObjectGroupPython] In_element001  label="In_element : 1"  # scripted group (container) (typed FeaturePython)
  n = 1
  ref = In_element
FEATURE [App::DocumentObjectGroupPython] G4_In  # scripted group (container) (typed FeaturePython)
  Dunit = g/cm3
  Dvalue = 7.31
  Group = -> [In_element001]
  conduct = 2
  density = 1
  expand = 3
  formula = In
  name = G4_In
  specific = 4
FEATURE [App::DocumentObjectGroupPython] Sn_element001  label="Sn_element : 1"  # scripted group (container) (typed FeaturePython)
  n = 1
  ref = Sn_element
FEATURE [App::DocumentObjectGroupPython] G4_Sn  # scripted group (container) (typed FeaturePython)
  Dunit = g/cm3
  Dvalue = 7.31
  Group = -> [Sn_element001]
  conduct = 2
  density = 1
  expand = 3
  formula = Sn
  name = G4_Sn
  specific = 4
FEATURE [App::DocumentObjectGroupPython] Sb_element001  label="Sb_element : 1"  # scripted group (container) (typed FeaturePython)
  n = 1
  ref = Sb_element
FEATURE [App::DocumentObjectGroupPython] G4_Sb  # scripted group (container) (typed FeaturePython)
  Dunit = g/cm3
  Dvalue = 6.691
  Group = -> [Sb_element001]
  conduct = 2
  density = 1
  expand = 3
  formula = Sb
  name = G4_Sb
  specific = 4
FEATURE [App::DocumentObjectGroupPython] Te_element002  label="Te_element : 002"  # scripted group (container) (typed FeaturePython)
  n = 1
  ref = Te_element
FEATURE [App::DocumentObjectGroupPython] G4_Te  # scripted group (container) (typed FeaturePython)
  Dunit = g/cm3
  Dvalue = 6.24
  Group = -> [Te_element002]
  conduct = 2
  density = 1
  expand = 3
  formula = Te
  name = G4_Te
  specific = 4
FEATURE [App::DocumentObjectGroupPython] I_element010  label="I_element : 006"  # scripted group (container) (typed FeaturePython)
  n = 1
  ref = I_element
FEATURE [App::DocumentObjectGroupPython] G4_I  # scripted group (container) (typed FeaturePython)
  Dunit = g/cm3
  Dvalue = 4.93
  Group = -> [I_element010]
  conduct = 2
  density = 1
  expand = 3
  formula = I
  name = G4_I
  specific = 4
FEATURE [App::DocumentObjectGroupPython] Xe_element001  label="Xe_element : 1"  # scripted group (container) (typed FeaturePython)
  n = 1
  ref = Xe_element
FEATURE [App::DocumentObjectGroupPython] G4_Xe  # scripted group (container) (typed FeaturePython)
  Dunit = g/cm3
  Dvalue = 0.00548536
  Group = -> [Xe_element001]
  conduct = 2
  density = 1
  expand = 3
  formula = Xe
  name = G4_Xe
  specific = 4
FEATURE [App::DocumentObjectGroupPython] Cs_element003  label="Cs_element : 003"  # scripted group (container) (typed FeaturePython)
  n = 1
  ref = Cs_element
FEATURE [App::DocumentObjectGroupPython] G4_Cs  # scripted group (container) (typed FeaturePython)
  Dunit = g/cm3
  Dvalue = 1.873
  Group = -> [Cs_element003]
  conduct = 2
  density = 1
  expand = 3
  formula = Cs
  name = G4_Cs
  specific = 4
FEATURE [App::DocumentObjectGroupPython] Ba_element003  label="Ba_element : 003"  # scripted group (container) (typed FeaturePython)
  n = 1
  ref = Ba_element
FEATURE [App::DocumentObjectGroupPython] G4_Ba  # scripted group (container) (typed FeaturePython)
  Dunit = g/cm3
  Dvalue = 3.5
  Group = -> [Ba_element003]
  conduct = 2
  density = 1
  expand = 3
  formula = Ba
  name = G4_Ba
  specific = 4
FEATURE [App::DocumentObjectGroupPython] La_element003  label="La_element : 003"  # scripted group (container) (typed FeaturePython)
  n = 1
  ref = La_element
FEATURE [App::DocumentObjectGroupPython] G4_La  # scripted group (container) (typed FeaturePython)
  Dunit = g/cm3
  Dvalue = 6.154
  Group = -> [La_element003]
  conduct = 2
  density = 1
  expand = 3
  formula = La
  name = G4_La
  specific = 4
FEATURE [App::DocumentObjectGroupPython] Ce_element002  label="Ce_element : 1"  # scripted group (container) (typed FeaturePython)
  n = 1
  ref = Ce_element
FEATURE [App::DocumentObjectGroupPython] G4_Ce  # scripted group (container) (typed FeaturePython)
  Dunit = g/cm3
  Dvalue = 6.657
  Group = -> [Ce_element002]
  conduct = 2
  density = 1
  expand = 3
  formula = Ce
  name = G4_Ce
  specific = 4
FEATURE [App::DocumentObjectGroupPython] Pr_element001  label="Pr_element : 1"  # scripted group (container) (typed FeaturePython)
  n = 1
  ref = Pr_element
FEATURE [App::DocumentObjectGroupPython] G4_Pr  # scripted group (container) (typed FeaturePython)
  Dunit = g/cm3
  Dvalue = 6.71
  Group = -> [Pr_element001]
  conduct = 2
  density = 1
  expand = 3
  formula = Pr
  name = G4_Pr
  specific = 4
FEATURE [App::DocumentObjectGroupPython] Nd_element001  label="Nd_element : 1"  # scripted group (container) (typed FeaturePython)
  n = 1
  ref = Nd_element
FEATURE [App::DocumentObjectGroupPython] G4_Nd  # scripted group (container) (typed FeaturePython)
  Dunit = g/cm3
  Dvalue = 6.9
  Group = -> [Nd_element001]
  conduct = 2
  density = 1
  expand = 3
  formula = Nd
  name = G4_Nd
  specific = 4
FEATURE [App::DocumentObjectGroupPython] Pm_element001  label="Pm_element : 1"  # scripted group (container) (typed FeaturePython)
  n = 1
  ref = Pm_element
FEATURE [App::DocumentObjectGroupPython] G4_Pm  # scripted group (container) (typed FeaturePython)
  Dunit = g/cm3
  Dvalue = 7.22
  Group = -> [Pm_element001]
  conduct = 2
  density = 1
  expand = 3
  formula = Pm
  name = G4_Pm
  specific = 4
FEATURE [App::DocumentObjectGroupPython] Sm_element001  label="Sm_element : 1"  # scripted group (container) (typed FeaturePython)
  n = 1
  ref = Sm_element
FEATURE [App::DocumentObjectGroupPython] G4_Sm  # scripted group (container) (typed FeaturePython)
  Dunit = g/cm3
  Dvalue = 7.46
  Group = -> [Sm_element001]
  conduct = 2
  density = 1
  expand = 3
  formula = Sm
  name = G4_Sm
  specific = 4
FEATURE [App::DocumentObjectGroupPython] Eu_element001  label="Eu_element : 1"  # scripted group (container) (typed FeaturePython)
  n = 1
  ref = Eu_element
FEATURE [App::DocumentObjectGroupPython] G4_Eu  # scripted group (container) (typed FeaturePython)
  Dunit = g/cm3
  Dvalue = 5.243
  Group = -> [Eu_element001]
  conduct = 2
  density = 1
  expand = 3
  formula = Eu
  name = G4_Eu
  specific = 4
FEATURE [App::DocumentObjectGroupPython] Gd_element002  label="Gd_element : 1"  # scripted group (container) (typed FeaturePython)
  n = 1
  ref = Gd_element
FEATURE [App::DocumentObjectGroupPython] G4_Gd  # scripted group (container) (typed FeaturePython)
  Dunit = g/cm3
  Dvalue = 7.9004
  Group = -> [Gd_element002]
  conduct = 2
  density = 1
  expand = 3
  formula = Gd
  name = G4_Gd
  specific = 4
FEATURE [App::DocumentObjectGroupPython] Tb_element001  label="Tb_element : 1"  # scripted group (container) (typed FeaturePython)
  n = 1
  ref = Tb_element
FEATURE [App::DocumentObjectGroupPython] G4_Tb  # scripted group (container) (typed FeaturePython)
  Dunit = g/cm3
  Dvalue = 8.229
  Group = -> [Tb_element001]
  conduct = 2
  density = 1
  expand = 3
  formula = Tb
  name = G4_Tb
  specific = 4
FEATURE [App::DocumentObjectGroupPython] Dy_element001  label="Dy_element : 1"  # scripted group (container) (typed FeaturePython)
  n = 1
  ref = Dy_element
FEATURE [App::DocumentObjectGroupPython] G4_Dy  # scripted group (container) (typed FeaturePython)
  Dunit = g/cm3
  Dvalue = 8.55
  Group = -> [Dy_element001]
  conduct = 2
  density = 1
  expand = 3
  formula = Dy
  name = G4_Dy
  specific = 4
FEATURE [App::DocumentObjectGroupPython] Ho_element001  label="Ho_element : 1"  # scripted group (container) (typed FeaturePython)
  n = 1
  ref = Ho_element
FEATURE [App::DocumentObjectGroupPython] G4_Ho  # scripted group (container) (typed FeaturePython)
  Dunit = g/cm3
  Dvalue = 8.795
  Group = -> [Ho_element001]
  conduct = 2
  density = 1
  expand = 3
  formula = Ho
  name = G4_Ho
  specific = 4
FEATURE [App::DocumentObjectGroupPython] Er_element001  label="Er_element : 1"  # scripted group (container) (typed FeaturePython)
  n = 1
  ref = Er_element
FEATURE [App::DocumentObjectGroupPython] G4_Er  # scripted group (container) (typed FeaturePython)
  Dunit = g/cm3
  Dvalue = 9.066
  Group = -> [Er_element001]
  conduct = 2
  density = 1
  expand = 3
  formula = Er
  name = G4_Er
  specific = 4
FEATURE [App::DocumentObjectGroupPython] Tm_element001  label="Tm_element : 1"  # scripted group (container) (typed FeaturePython)
  n = 1
  ref = Tm_element
FEATURE [App::DocumentObjectGroupPython] G4_Tm  # scripted group (container) (typed FeaturePython)
  Dunit = g/cm3
  Dvalue = 9.321
  Group = -> [Tm_element001]
  conduct = 2
  density = 1
  expand = 3
  formula = Tm
  name = G4_Tm
  specific = 4
FEATURE [App::DocumentObjectGroupPython] Yb_element001  label="Yb_element : 1"  # scripted group (container) (typed FeaturePython)
  n = 1
  ref = Yb_element
FEATURE [App::DocumentObjectGroupPython] G4_Yb  # scripted group (container) (typed FeaturePython)
  Dunit = g/cm3
  Dvalue = 6.73
  Group = -> [Yb_element001]
  conduct = 2
  density = 1
  expand = 3
  formula = Yb
  name = G4_Yb
  specific = 4
FEATURE [App::DocumentObjectGroupPython] Lu_element001  label="Lu_element : 1"  # scripted group (container) (typed FeaturePython)
  n = 1
  ref = Lu_element
FEATURE [App::DocumentObjectGroupPython] G4_Lu  # scripted group (container) (typed FeaturePython)
  Dunit = g/cm3
  Dvalue = 9.84
  Group = -> [Lu_element001]
  conduct = 2
  density = 1
  expand = 3
  formula = Lu
  name = G4_Lu
  specific = 4
FEATURE [App::DocumentObjectGroupPython] Hf_element001  label="Hf_element : 1"  # scripted group (container) (typed FeaturePython)
  n = 1
  ref = Hf_element
FEATURE [App::DocumentObjectGroupPython] G4_Hf  # scripted group (container) (typed FeaturePython)
  Dunit = g/cm3
  Dvalue = 13.31
  Group = -> [Hf_element001]
  conduct = 2
  density = 1
  expand = 3
  formula = Hf
  name = G4_Hf
  specific = 4
FEATURE [App::DocumentObjectGroupPython] Ta_element001  label="Ta_element : 1"  # scripted group (container) (typed FeaturePython)
  n = 1
  ref = Ta_element
FEATURE [App::DocumentObjectGroupPython] G4_Ta  # scripted group (container) (typed FeaturePython)
  Dunit = g/cm3
  Dvalue = 16.654
  Group = -> [Ta_element001]
  conduct = 2
  density = 1
  expand = 3
  formula = Ta
  name = G4_Ta
  specific = 4
FEATURE [App::DocumentObjectGroupPython] W_element004  label="W_element : 004"  # scripted group (container) (typed FeaturePython)
  n = 1
  ref = W_element
FEATURE [App::DocumentObjectGroupPython] G4_W  # scripted group (container) (typed FeaturePython)
  Dunit = g/cm3
  Dvalue = 19.3
  Group = -> [W_element004]
  conduct = 2
  density = 1
  expand = 3
  formula = W
  name = G4_W
  specific = 4
FEATURE [App::DocumentObjectGroupPython] Re_element001  label="Re_element : 1"  # scripted group (container) (typed FeaturePython)
  n = 1
  ref = Re_element
FEATURE [App::DocumentObjectGroupPython] G4_Re  # scripted group (container) (typed FeaturePython)
  Dunit = g/cm3
  Dvalue = 21.02
  Group = -> [Re_element001]
  conduct = 2
  density = 1
  expand = 3
  formula = Re
  name = G4_Re
  specific = 4
FEATURE [App::DocumentObjectGroupPython] Os_element001  label="Os_element : 1"  # scripted group (container) (typed FeaturePython)
  n = 1
  ref = Os_element
FEATURE [App::DocumentObjectGroupPython] G4_Os  # scripted group (container) (typed FeaturePython)
  Dunit = g/cm3
  Dvalue = 22.57
  Group = -> [Os_element001]
  conduct = 2
  density = 1
  expand = 3
  formula = Os
  name = G4_Os
  specific = 4
FEATURE [App::DocumentObjectGroupPython] Ir_element001  label="Ir_element : 1"  # scripted group (container) (typed FeaturePython)
  n = 1
  ref = Ir_element
FEATURE [App::DocumentObjectGroupPython] G4_Ir  # scripted group (container) (typed FeaturePython)
  Dunit = g/cm3
  Dvalue = 22.42
  Group = -> [Ir_element001]
  conduct = 2
  density = 1
  expand = 3
  formula = Ir
  name = G4_Ir
  specific = 4
FEATURE [App::DocumentObjectGroupPython] Pt_element001  label="Pt_element : 1"  # scripted group (container) (typed FeaturePython)
  n = 1
  ref = Pt_element
FEATURE [App::DocumentObjectGroupPython] G4_Pt  # scripted group (container) (typed FeaturePython)
  Dunit = g/cm3
  Dvalue = 21.45
  Group = -> [Pt_element001]
  conduct = 2
  density = 1
  expand = 3
  formula = Pt
  name = G4_Pt
  specific = 4
FEATURE [App::DocumentObjectGroupPython] Au_element001  label="Au_element : 1"  # scripted group (container) (typed FeaturePython)
  n = 1
  ref = Au_element
FEATURE [App::DocumentObjectGroupPython] G4_Au  # scripted group (container) (typed FeaturePython)
  Dunit = g/cm3
  Dvalue = 19.32
  Group = -> [Au_element001]
  conduct = 2
  density = 1
  expand = 3
  formula = Au
  name = G4_Au
  specific = 4
FEATURE [App::DocumentObjectGroupPython] Hg_element002  label="Hg_element : 002"  # scripted group (container) (typed FeaturePython)
  n = 1
  ref = Hg_element
FEATURE [App::DocumentObjectGroupPython] G4_Hg  # scripted group (container) (typed FeaturePython)
  Dunit = g/cm3
  Dvalue = 13.546
  Group = -> [Hg_element002]
  conduct = 2
  density = 1
  expand = 3
  formula = Hg
  name = G4_Hg
  specific = 4
FEATURE [App::DocumentObjectGroupPython] Tl_element002  label="Tl_element : 002"  # scripted group (container) (typed FeaturePython)
  n = 1
  ref = Tl_element
FEATURE [App::DocumentObjectGroupPython] G4_Tl  # scripted group (container) (typed FeaturePython)
  Dunit = g/cm3
  Dvalue = 11.72
  Group = -> [Tl_element002]
  conduct = 2
  density = 1
  expand = 3
  formula = Tl
  name = G4_Tl
  specific = 4
FEATURE [App::DocumentObjectGroupPython] Pb_element003  label="Pb_element : 1"  # scripted group (container) (typed FeaturePython)
  n = 1
  ref = Pb_element
FEATURE [App::DocumentObjectGroupPython] G4_Pb  # scripted group (container) (typed FeaturePython)
  Dunit = g/cm3
  Dvalue = 11.35
  Group = -> [Pb_element003]
  conduct = 2
  density = 1
  expand = 3
  formula = Pb
  name = G4_Pb
  specific = 4
FEATURE [App::DocumentObjectGroupPython] Bi_element002  label="Bi_element : 1"  # scripted group (container) (typed FeaturePython)
  n = 1
  ref = Bi_element
FEATURE [App::DocumentObjectGroupPython] G4_Bi  # scripted group (container) (typed FeaturePython)
  Dunit = g/cm3
  Dvalue = 9.747
  Group = -> [Bi_element002]
  conduct = 2
  density = 1
  expand = 3
  formula = Bi
  name = G4_Bi
  specific = 4
FEATURE [App::DocumentObjectGroupPython] Po_element001  label="Po_element : 1"  # scripted group (container) (typed FeaturePython)
  n = 1
  ref = Po_element
FEATURE [App::DocumentObjectGroupPython] G4_Po  # scripted group (container) (typed FeaturePython)
  Dunit = g/cm3
  Dvalue = 9.32
  Group = -> [Po_element001]
  conduct = 2
  density = 1
  expand = 3
  formula = Po
  name = G4_Po
  specific = 4
FEATURE [App::DocumentObjectGroupPython] At_element001  label="At_element : 1"  # scripted group (container) (typed FeaturePython)
  n = 1
  ref = At_element
FEATURE [App::DocumentObjectGroupPython] G4_At  # scripted group (container) (typed FeaturePython)
  Dunit = g/cm3
  Dvalue = 9.32
  Group = -> [At_element001]
  conduct = 2
  density = 1
  expand = 3
  formula = At
  name = G4_At
  specific = 4
FEATURE [App::DocumentObjectGroupPython] Rn_element001  label="Rn_element : 1"  # scripted group (container) (typed FeaturePython)
  n = 1
  ref = Rn_element
FEATURE [App::DocumentObjectGroupPython] G4_Rn  # scripted group (container) (typed FeaturePython)
  Dunit = g/cm3
  Dvalue = 0.00900662
  Group = -> [Rn_element001]
  conduct = 2
  density = 1
  expand = 3
  formula = Rn
  name = G4_Rn
  specific = 4
FEATURE [App::DocumentObjectGroupPython] Fr_element001  label="Fr_element : 1"  # scripted group (container) (typed FeaturePython)
  n = 1
  ref = Fr_element
FEATURE [App::DocumentObjectGroupPython] G4_Fr  # scripted group (container) (typed FeaturePython)
  Dunit = g/cm3
  Dvalue = 1
  Group = -> [Fr_element001]
  conduct = 2
  density = 1
  expand = 3
  formula = Fr
  name = G4_Fr
  specific = 4
FEATURE [App::DocumentObjectGroupPython] Ra_element001  label="Ra_element : 1"  # scripted group (container) (typed FeaturePython)
  n = 1
  ref = Ra_element
FEATURE [App::DocumentObjectGroupPython] G4_Ra  # scripted group (container) (typed FeaturePython)
  Dunit = g/cm3
  Dvalue = 5
  Group = -> [Ra_element001]
  conduct = 2
  density = 1
  expand = 3
  formula = Ra
  name = G4_Ra
  specific = 4
FEATURE [App::DocumentObjectGroupPython] Ac_element001  label="Ac_element : 1"  # scripted group (container) (typed FeaturePython)
  n = 1
  ref = Ac_element
FEATURE [App::DocumentObjectGroupPython] G4_Ac  # scripted group (container) (typed FeaturePython)
  Dunit = g/cm3
  Dvalue = 10.07
  Group = -> [Ac_element001]
  conduct = 2
  density = 1
  expand = 3
  formula = Ac
  name = G4_Ac
  specific = 4
FEATURE [App::DocumentObjectGroupPython] Th_element001  label="Th_element : 1"  # scripted group (container) (typed FeaturePython)
  n = 1
  ref = Th_element
FEATURE [App::DocumentObjectGroupPython] G4_Th  # scripted group (container) (typed FeaturePython)
  Dunit = g/cm3
  Dvalue = 11.72
  Group = -> [Th_element001]
  conduct = 2
  density = 1
  expand = 3
  formula = Th
  name = G4_Th
  specific = 4
FEATURE [App::DocumentObjectGroupPython] Pa_element001  label="Pa_element : 1"  # scripted group (container) (typed FeaturePython)
  n = 1
  ref = Pa_element
FEATURE [App::DocumentObjectGroupPython] G4_Pa  # scripted group (container) (typed FeaturePython)
  Dunit = g/cm3
  Dvalue = 15.37
  Group = -> [Pa_element001]
  conduct = 2
  density = 1
  expand = 3
  formula = Pa
  name = G4_Pa
  specific = 4
FEATURE [App::DocumentObjectGroupPython] U_element004  label="U_element : 004"  # scripted group (container) (typed FeaturePython)
  n = 1
  ref = U_element
FEATURE [App::DocumentObjectGroupPython] G4_U  # scripted group (container) (typed FeaturePython)
  Dunit = g/cm3
  Dvalue = 18.95
  Group = -> [U_element004]
  conduct = 2
  density = 1
  expand = 3
  formula = U
  name = G4_U
  specific = 4
FEATURE [App::DocumentObjectGroupPython] Np_element001  label="Np_element : 1"  # scripted group (container) (typed FeaturePython)
  n = 1
  ref = Np_element
FEATURE [App::DocumentObjectGroupPython] G4_Np  # scripted group (container) (typed FeaturePython)
  Dunit = g/cm3
  Dvalue = 20.25
  Group = -> [Np_element001]
  conduct = 2
  density = 1
  expand = 3
  formula = Np
  name = G4_Np
  specific = 4
FEATURE [App::DocumentObjectGroupPython] Pu_element002  label="Pu_element : 002"  # scripted group (container) (typed FeaturePython)
  n = 1
  ref = Pu_element
FEATURE [App::DocumentObjectGroupPython] G4_Pu  # scripted group (container) (typed FeaturePython)
  Dunit = g/cm3
  Dvalue = 19.84
  Group = -> [Pu_element002]
  conduct = 2
  density = 1
  expand = 3
  formula = Pu
  name = G4_Pu
  specific = 4
FEATURE [App::DocumentObjectGroupPython] Am_element001  label="Am_element : 1"  # scripted group (container) (typed FeaturePython)
  n = 1
  ref = Am_element
FEATURE [App::DocumentObjectGroupPython] G4_Am  # scripted group (container) (typed FeaturePython)
  Dunit = g/cm3
  Dvalue = 13.67
  Group = -> [Am_element001]
  conduct = 2
  density = 1
  expand = 3
  formula = Am
  name = G4_Am
  specific = 4
FEATURE [App::DocumentObjectGroupPython] Cm_element001  label="Cm_element : 1"  # scripted group (container) (typed FeaturePython)
  n = 1
  ref = Cm_element
FEATURE [App::DocumentObjectGroupPython] G4_Cm  # scripted group (container) (typed FeaturePython)
  Dunit = g/cm3
  Dvalue = 13.51
  Group = -> [Cm_element001]
  conduct = 2
  density = 1
  expand = 3
  formula = Cm
  name = G4_Cm
  specific = 4
FEATURE [App::DocumentObjectGroupPython] Bk_element001  label="Bk_element : 1"  # scripted group (container) (typed FeaturePython)
  n = 1
  ref = Bk_element
FEATURE [App::DocumentObjectGroupPython] G4_Bk  # scripted group (container) (typed FeaturePython)
  Dunit = g/cm3
  Dvalue = 14
  Group = -> [Bk_element001]
  conduct = 2
  density = 1
  expand = 3
  formula = Bk
  name = G4_Bk
  specific = 4
FEATURE [App::DocumentObjectGroupPython] Cf_element001  label="Cf_element : 1"  # scripted group (container) (typed FeaturePython)
  n = 1
  ref = Cf_element
FEATURE [App::DocumentObjectGroupPython] G4_Cf  # scripted group (container) (typed FeaturePython)
  Dunit = g/cm3
  Dvalue = 10
  Group = -> [Cf_element001]
  conduct = 2
  density = 1
  expand = 3
  formula = Cf
  name = G4_Cf
  specific = 4
FEATURE [App::DocumentObjectGroupPython] Element  # scripted group (container) (typed FeaturePython)
  Group = -> [G4_H,G4_He,G4_Li,G4_Be,G4_B,G4_C,G4_N,G4_O,G4_F,G4_Ne,G4_Na,G4_Mg,G4_Al,G4_Si,G4_P,G4_S,G4_Cl,G4_Ar,G4_K,G4_Ca,G4_Sc,G4_Ti,G4_V,G4_Cr,G4_Mn,G4_Fe,G4_Co,G4_Ni,G4_Cu,G4_Zn,G4_Ga,G4_Ge,G4_As,G4_Se,G4_Br,G4_Kr,G4_Rb,G4_Sr,G4_Y,G4_Zr,G4_Nb,G4_Mo,G4_Tc,G4_Ru,G4_Rh,G4_Pd,G4_Ag,G4_Cd,G4_In,G4_Sn,G4_Sb,G4_Te,G4_I,G4_Xe,G4_Cs,G4_Ba,G4_La,G4_Ce,G4_Pr,G4_Nd,G4_Pm,G4_Sm,G4_Eu,G4_Gd,G4_Tb,G4_Dy,G4_Ho,G4_Er,+30 more]
FEATURE [App::DocumentObjectGroupPython] H_element114  label="H_element : 063"  # scripted group (container) (typed FeaturePython)
  n = 2
  ref = H_element
FEATURE [App::DocumentObjectGroupPython] G4_lH2  # scripted group (container) (typed FeaturePython)
  Dunit = g/cm3
  Dvalue = 0.0708
  Group = -> [H_element114]
  conduct = 2
  density = 1
  expand = 3
  formula = G4_lH2
  name = G4_lH2
  specific = 4
FEATURE [App::DocumentObjectGroupPython] N_element049  label="N_element : 022"  # scripted group (container) (typed FeaturePython)
  n = 2
  ref = N_element
FEATURE [App::DocumentObjectGroupPython] G4_lN2  # scripted group (container) (typed FeaturePython)
  Dunit = g/cm3
  Dvalue = 0.807
  Group = -> [N_element049]
  conduct = 2
  density = 1
  expand = 3
  formula = G4_lN2
  name = G4_lN2
  specific = 4
FEATURE [App::DocumentObjectGroupPython] O_element106  label="O_element : 060"  # scripted group (container) (typed FeaturePython)
  n = 2
  ref = O_element
FEATURE [App::DocumentObjectGroupPython] G4_lO2  # scripted group (container) (typed FeaturePython)
  Dunit = g/cm3
  Dvalue = 1.141
  Group = -> [O_element106]
  conduct = 2
  density = 1
  expand = 3
  formula = G4_lO2
  name = G4_lO2
  specific = 4
FEATURE [App::DocumentObjectGroupPython] Ar_element003  label="Ar_element : 002"  # scripted group (container) (typed FeaturePython)
  n = 1
  ref = Ar_element
FEATURE [App::DocumentObjectGroupPython] G4_lAr  # scripted group (container) (typed FeaturePython)
  Dunit = g/cm3
  Dvalue = 1.396
  Group = -> [Ar_element003]
  conduct = 2
  density = 1
  expand = 3
  formula = G4_lAr
  name = G4_lAr
  specific = 4
FEATURE [App::DocumentObjectGroupPython] Br_element008  label="Br_element : 005"  # scripted group (container) (typed FeaturePython)
  n = 1
  ref = Br_element
FEATURE [App::DocumentObjectGroupPython] G4_lBr  # scripted group (container) (typed FeaturePython)
  Dunit = g/cm3
  Dvalue = 3.1028
  Group = -> [Br_element008]
  conduct = 2
  density = 1
  expand = 3
  formula = G4_lBr
  name = G4_lBr
  specific = 4
FEATURE [App::DocumentObjectGroupPython] Kr_element002  label="Kr_element : 002"  # scripted group (container) (typed FeaturePython)
  n = 1
  ref = Kr_element
FEATURE [App::DocumentObjectGroupPython] G4_lKr  # scripted group (container) (typed FeaturePython)
  Dunit = g/cm3
  Dvalue = 2.418
  Group = -> [Kr_element002]
  conduct = 2
  density = 1
  expand = 3
  formula = G4_lKr
  name = G4_lKr
  specific = 4
FEATURE [App::DocumentObjectGroupPython] Xe_element002  label="Xe_element : 002"  # scripted group (container) (typed FeaturePython)
  n = 1
  ref = Xe_element
FEATURE [App::DocumentObjectGroupPython] G4_lXe  # scripted group (container) (typed FeaturePython)
  Dunit = g/cm3
  Dvalue = 2.953
  Group = -> [Xe_element002]
  conduct = 2
  density = 1
  expand = 3
  formula = G4_lXe
  name = G4_lXe
  specific = 4
FEATURE [App::DocumentObjectGroupPython] O_element107  label="O_element : 061"  # scripted group (container) (typed FeaturePython)
  n = 4
  ref = O_element
FEATURE [App::DocumentObjectGroupPython] Pb_element004  label="Pb_element : 002"  # scripted group (container) (typed FeaturePython)
  n = 1
  ref = Pb_element
FEATURE [App::DocumentObjectGroupPython] W_element005  label="W_element : 005"  # scripted group (container) (typed FeaturePython)
  n = 1
  ref = W_element
FEATURE [App::DocumentObjectGroupPython] G4_PbWO4  # scripted group (container) (typed FeaturePython)
  Dunit = g/cm3
  Dvalue = 8.28
  Group = -> [O_element107,Pb_element004,W_element005]
  conduct = 2
  density = 1
  expand = 3
  formula = G4_PbWO4
  name = G4_PbWO4
  specific = 4
FEATURE [App::DocumentObjectGroupPython] H_element115  label="H_element : 064"  # scripted group (container) (typed FeaturePython)
  n = 1
  ref = H_element
FEATURE [App::DocumentObjectGroupPython] G4_Galactic  # scripted group (container) (typed FeaturePython)
  Dunit = g/cm3
  Dvalue = 0
  Group = -> [H_element115]
  conduct = 2
  density = 1
  expand = 3
  formula = G4_Galactic
  name = G4_Galactic
  specific = 4
FEATURE [App::DocumentObjectGroupPython] C_element125  label="C_element : 071"  # scripted group (container) (typed FeaturePython)
  n = 1
  ref = C_element
FEATURE [App::DocumentObjectGroupPython] G4_GRAPHITE_POROUS  # scripted group (container) (typed FeaturePython)
  Dunit = g/cm3
  Dvalue = 1.7
  Group = -> [C_element125]
  conduct = 2
  density = 1
  expand = 3
  formula = G4_GRAPHITE_POROUS
  name = G4_GRAPHITE_POROUS
  specific = 4
FEATURE [App::DocumentObjectGroupPython] H_element116  label="H_element : 0.150"  # scripted group (container) (typed FeaturePython)
  n = 0.080538
FEATURE [App::DocumentObjectGroupPython] C_element126  label="C_element : 0.600"  # scripted group (container) (typed FeaturePython)
  n = 0.599848
FEATURE [App::DocumentObjectGroupPython] O_element108  label="O_element : 0.320"  # scripted group (container) (typed FeaturePython)
  n = 0.319614
FEATURE [App::DocumentObjectGroupPython] G4_LUCITE  # scripted group (container) (typed FeaturePython)
  Dunit = g/cm3
  Dvalue = 1.19
  Group = -> [H_element116,C_element126,O_element108]
  conduct = 2
  density = 1
  expand = 3
  formula = G4_LUCITE
  name = G4_LUCITE
  specific = 4
FEATURE [App::DocumentObjectGroupPython] Cu_element002  label="Cu_element : 62"  # scripted group (container) (typed FeaturePython)
  n = 62
  ref = Cu_element
FEATURE [App::DocumentObjectGroupPython] Zn_element002  label="Zn_element : 35"  # scripted group (container) (typed FeaturePython)
  n = 35
  ref = Zn_element
FEATURE [App::DocumentObjectGroupPython] Pb_element005  label="Pb_element : 3"  # scripted group (container) (typed FeaturePython)
  n = 3
  ref = Pb_element
FEATURE [App::DocumentObjectGroupPython] G4_BRASS  # scripted group (container) (typed FeaturePython)
  Dunit = g/cm3
  Dvalue = 8.52
  Group = -> [Cu_element002,Zn_element002,Pb_element005]
  conduct = 2
  density = 1
  expand = 3
  formula = G4_BRASS
  name = G4_BRASS
  specific = 4
FEATURE [App::DocumentObjectGroupPython] Cu_element003  label="Cu_element : 89"  # scripted group (container) (typed FeaturePython)
  n = 89
  ref = Cu_element
FEATURE [App::DocumentObjectGroupPython] Zn_element003  label="Zn_element : 9"  # scripted group (container) (typed FeaturePython)
  n = 9
  ref = Zn_element
FEATURE [App::DocumentObjectGroupPython] Pb_element006  label="Pb_element : 2"  # scripted group (container) (typed FeaturePython)
  n = 2
  ref = Pb_element
FEATURE [App::DocumentObjectGroupPython] G4_BRONZE  # scripted group (container) (typed FeaturePython)
  Dunit = g/cm3
  Dvalue = 8.82
  Group = -> [Cu_element003,Zn_element003,Pb_element006]
  conduct = 2
  density = 1
  expand = 3
  formula = G4_BRONZE
  name = G4_BRONZE
  specific = 4
FEATURE [App::DocumentObjectGroupPython] Fe_element008  label="Fe_element : 74"  # scripted group (container) (typed FeaturePython)
  n = 74
  ref = Fe_element
FEATURE [App::DocumentObjectGroupPython] Cr_element002  label="Cr_element : 18"  # scripted group (container) (typed FeaturePython)
  n = 18
  ref = Cr_element
FEATURE [App::DocumentObjectGroupPython] Ni_element002  label="Ni_element : 8"  # scripted group (container) (typed FeaturePython)
  n = 8
  ref = Ni_element
FEATURE [App::DocumentObjectGroupPython] G4_STAINLESS_STEEL  label="G4_STAINLESS-STEEL"  # scripted group (container) (typed FeaturePython)
  Dunit = g/cm3
  Dvalue = 8
  Group = -> [Fe_element008,Cr_element002,Ni_element002]
  conduct = 2
  density = 1
  expand = 3
  formula = G4_STAINLESS-STEEL
  name = G4_STAINLESS-STEEL
  specific = 4
FEATURE [App::DocumentObjectGroupPython] H_element117  label="H_element : 065"  # scripted group (container) (typed FeaturePython)
  n = 18
  ref = H_element
FEATURE [App::DocumentObjectGroupPython] C_element127  label="C_element : 072"  # scripted group (container) (typed FeaturePython)
  n = 12
  ref = C_element
FEATURE [App::DocumentObjectGroupPython] O_element109  label="O_element : 062"  # scripted group (container) (typed FeaturePython)
  n = 7
  ref = O_element
FEATURE [App::DocumentObjectGroupPython] G4_CR39  # scripted group (container) (typed FeaturePython)
  Dunit = g/cm3
  Dvalue = 1.32
  Group = -> [H_element117,C_element127,O_element109]
  conduct = 2
  density = 1
  expand = 3
  formula = G4_CR39
  name = G4_CR39
  specific = 4
FEATURE [App::DocumentObjectGroupPython] H_element118  label="H_element : 38"  # scripted group (container) (typed FeaturePython)
  n = 38
  ref = H_element
FEATURE [App::DocumentObjectGroupPython] C_element128  label="C_element : 073"  # scripted group (container) (typed FeaturePython)
  n = 18
  ref = C_element
FEATURE [App::DocumentObjectGroupPython] O_element110  label="O_element : 063"  # scripted group (container) (typed FeaturePython)
  n = 1
  ref = O_element
FEATURE [App::DocumentObjectGroupPython] G4_OCTADECANOL  # scripted group (container) (typed FeaturePython)
  Dunit = g/cm3
  Dvalue = 0.812
  Group = -> [H_element118,C_element128,O_element110]
  conduct = 2
  density = 1
  expand = 3
  formula = G4_OCTADECANOL
  name = G4_OCTADECANOL
  specific = 4
FEATURE [App::DocumentObjectGroupPython] HEP  # scripted group (container) (typed FeaturePython)
  Group = -> [G4_lH2,G4_lN2,G4_lO2,G4_lAr,G4_lBr,G4_lKr,G4_lXe,G4_PbWO4,G4_Galactic,G4_GRAPHITE_POROUS,G4_LUCITE,G4_BRASS,G4_BRONZE,G4_STAINLESS_STEEL,G4_CR39,G4_OCTADECANOL]
FEATURE [App::DocumentObjectGroupPython] C_element129  label="C_element : 074"  # scripted group (container) (typed FeaturePython)
  n = 14
  ref = C_element
FEATURE [App::DocumentObjectGroupPython] H_element119  label="H_element : 066"  # scripted group (container) (typed FeaturePython)
  n = 10
  ref = H_element
FEATURE [App::DocumentObjectGroupPython] O_element111  label="O_element : 064"  # scripted group (container) (typed FeaturePython)
  n = 2
  ref = O_element
FEATURE [App::DocumentObjectGroupPython] N_element050  label="N_element : 023"  # scripted group (container) (typed FeaturePython)
  n = 2
  ref = N_element
FEATURE [App::DocumentObjectGroupPython] G4_KEVLAR  # scripted group (container) (typed FeaturePython)
  Dunit = g/cm3
  Dvalue = 1.44
  Group = -> [C_element129,H_element119,O_element111,N_element050]
  conduct = 2
  density = 1
  expand = 3
  formula = G4_KEVLAR
  name = G4_KEVLAR
  specific = 4
FEATURE [App::DocumentObjectGroupPython] C_element130  label="C_element : 075"  # scripted group (container) (typed FeaturePython)
  n = 10
  ref = C_element
FEATURE [App::DocumentObjectGroupPython] H_element120  label="H_element : 067"  # scripted group (container) (typed FeaturePython)
  n = 8
  ref = H_element
FEATURE [App::DocumentObjectGroupPython] O_element112  label="O_element : 065"  # scripted group (container) (typed FeaturePython)
  n = 4
  ref = O_element
FEATURE [App::DocumentObjectGroupPython] G4_DACRON  # scripted group (container) (typed FeaturePython)
  Dunit = g/cm3
  Dvalue = 1.4
  Group = -> [C_element130,H_element120,O_element112]
  conduct = 2
  density = 1
  expand = 3
  formula = G4_DACRON
  name = G4_DACRON
  specific = 4
FEATURE [App::DocumentObjectGroupPython] C_element131  label="C_element : 076"  # scripted group (container) (typed FeaturePython)
  n = 4
  ref = C_element
FEATURE [App::DocumentObjectGroupPython] H_element121  label="H_element : 068"  # scripted group (container) (typed FeaturePython)
  n = 5
  ref = H_element
FEATURE [App::DocumentObjectGroupPython] Cl_element030  label="Cl_element : 016"  # scripted group (container) (typed FeaturePython)
  n = 1
  ref = Cl_element
FEATURE [App::DocumentObjectGroupPython] G4_NEOPRENE  # scripted group (container) (typed FeaturePython)
  Dunit = g/cm3
  Dvalue = 1.23
  Group = -> [C_element131,H_element121,Cl_element030]
  conduct = 2
  density = 1
  expand = 3
  formula = G4_NEOPRENE
  name = G4_NEOPRENE
  specific = 4
FEATURE [App::DocumentObjectGroupPython] Space  # scripted group (container) (typed FeaturePython)
  Group = -> [G4_KEVLAR,G4_DACRON,G4_NEOPRENE]
FEATURE [App::DocumentObjectGroupPython] H_element122  label="H_element : 069"  # scripted group (container) (typed FeaturePython)
  n = 5
  ref = H_element
FEATURE [App::DocumentObjectGroupPython] C_element132  label="C_element : 077"  # scripted group (container) (typed FeaturePython)
  n = 4
  ref = C_element
FEATURE [App::DocumentObjectGroupPython] N_element051  label="N_element : 3"  # scripted group (container) (typed FeaturePython)
  n = 3
  ref = N_element
FEATURE [App::DocumentObjectGroupPython] O_element113  label="O_element : 066"  # scripted group (container) (typed FeaturePython)
  n = 1
  ref = O_element
FEATURE [App::DocumentObjectGroupPython] G4_CYTOSINE  # scripted group (container) (typed FeaturePython)
  Dunit = g/cm3
  Dvalue = 1.55
  Group = -> [H_element122,C_element132,N_element051,O_element113]
  conduct = 2
  density = 1
  expand = 3
  formula = G4_CYTOSINE
  name = G4_CYTOSINE
  specific = 4
FEATURE [App::DocumentObjectGroupPython] H_element123  label="H_element : 070"  # scripted group (container) (typed FeaturePython)
  n = 6
  ref = H_element
FEATURE [App::DocumentObjectGroupPython] C_element133  label="C_element : 078"  # scripted group (container) (typed FeaturePython)
  n = 5
  ref = C_element
FEATURE [App::DocumentObjectGroupPython] N_element052  label="N_element : 024"  # scripted group (container) (typed FeaturePython)
  n = 2
  ref = N_element
FEATURE [App::DocumentObjectGroupPython] O_element114  label="O_element : 067"  # scripted group (container) (typed FeaturePython)
  n = 2
  ref = O_element
FEATURE [App::DocumentObjectGroupPython] G4_THYMINE  # scripted group (container) (typed FeaturePython)
  Dunit = g/cm3
  Dvalue = 1.23
  Group = -> [H_element123,C_element133,N_element052,O_element114]
  conduct = 2
  density = 1
  expand = 3
  formula = G4_THYMINE
  name = G4_THYMINE
  specific = 4
FEATURE [App::DocumentObjectGroupPython] H_element124  label="H_element : 071"  # scripted group (container) (typed FeaturePython)
  n = 4
  ref = H_element
FEATURE [App::DocumentObjectGroupPython] C_element134  label="C_element : 079"  # scripted group (container) (typed FeaturePython)
  n = 4
  ref = C_element
FEATURE [App::DocumentObjectGroupPython] N_element053  label="N_element : 025"  # scripted group (container) (typed FeaturePython)
  n = 2
  ref = N_element
FEATURE [App::DocumentObjectGroupPython] O_element115  label="O_element : 068"  # scripted group (container) (typed FeaturePython)
  n = 2
  ref = O_element
FEATURE [App::DocumentObjectGroupPython] G4_URACIL  # scripted group (container) (typed FeaturePython)
  Dunit = g/cm3
  Dvalue = 1.32
  Group = -> [H_element124,C_element134,N_element053,O_element115]
  conduct = 2
  density = 1
  expand = 3
  formula = G4_URACIL
  name = G4_URACIL
  specific = 4
FEATURE [App::DocumentObjectGroupPython] H_element125  label="H_element : 072"  # scripted group (container) (typed FeaturePython)
  n = 4
  ref = H_element
FEATURE [App::DocumentObjectGroupPython] C_element135  label="C_element : 080"  # scripted group (container) (typed FeaturePython)
  n = 5
  ref = C_element
FEATURE [App::DocumentObjectGroupPython] N_element054  label="N_element : 026"  # scripted group (container) (typed FeaturePython)
  n = 5
  ref = N_element
FEATURE [App::DocumentObjectGroupPython] G4_DNA_ADENINE  # scripted group (container) (typed FeaturePython)
  Dunit = g/cm3
  Dvalue = 1
  Group = -> [H_element125,C_element135,N_element054]
  conduct = 2
  density = 1
  expand = 3
  formula = G4_DNA_ADENINE
  name = G4_DNA_ADENINE
  specific = 4
FEATURE [App::DocumentObjectGroupPython] H_element126  label="H_element : 073"  # scripted group (container) (typed FeaturePython)
  n = 4
  ref = H_element
FEATURE [App::DocumentObjectGroupPython] C_element136  label="C_element : 081"  # scripted group (container) (typed FeaturePython)
  n = 5
  ref = C_element
FEATURE [App::DocumentObjectGroupPython] N_element055  label="N_element : 027"  # scripted group (container) (typed FeaturePython)
  n = 5
  ref = N_element
FEATURE [App::DocumentObjectGroupPython] O_element116  label="O_element : 069"  # scripted group (container) (typed FeaturePython)
  n = 1
  ref = O_element
FEATURE [App::DocumentObjectGroupPython] G4_DNA_GUANINE  # scripted group (container) (typed FeaturePython)
  Dunit = g/cm3
  Dvalue = 1
  Group = -> [H_element126,C_element136,N_element055,O_element116]
  conduct = 2
  density = 1
  expand = 3
  formula = G4_DNA_GUANINE
  name = G4_DNA_GUANINE
  specific = 4
FEATURE [App::DocumentObjectGroupPython] H_element127  label="H_element : 074"  # scripted group (container) (typed FeaturePython)
  n = 4
  ref = H_element
FEATURE [App::DocumentObjectGroupPython] C_element137  label="C_element : 082"  # scripted group (container) (typed FeaturePython)
  n = 4
  ref = C_element
FEATURE [App::DocumentObjectGroupPython] N_element056  label="N_element : 028"  # scripted group (container) (typed FeaturePython)
  n = 3
  ref = N_element
FEATURE [App::DocumentObjectGroupPython] O_element117  label="O_element : 070"  # scripted group (container) (typed FeaturePython)
  n = 1
  ref = O_element
FEATURE [App::DocumentObjectGroupPython] G4_DNA_CYTOSINE  # scripted group (container) (typed FeaturePython)
  Dunit = g/cm3
  Dvalue = 1
  Group = -> [H_element127,C_element137,N_element056,O_element117]
  conduct = 2
  density = 1
  expand = 3
  formula = G4_DNA_CYTOSINE
  name = G4_DNA_CYTOSINE
  specific = 4
FEATURE [App::DocumentObjectGroupPython] H_element128  label="H_element : 075"  # scripted group (container) (typed FeaturePython)
  n = 5
  ref = H_element
FEATURE [App::DocumentObjectGroupPython] C_element138  label="C_element : 083"  # scripted group (container) (typed FeaturePython)
  n = 5
  ref = C_element
FEATURE [App::DocumentObjectGroupPython] N_element057  label="N_element : 029"  # scripted group (container) (typed FeaturePython)
  n = 2
  ref = N_element
FEATURE [App::DocumentObjectGroupPython] O_element118  label="O_element : 071"  # scripted group (container) (typed FeaturePython)
  n = 2
  ref = O_element
FEATURE [App::DocumentObjectGroupPython] G4_DNA_THYMINE  # scripted group (container) (typed FeaturePython)
  Dunit = g/cm3
  Dvalue = 1
  Group = -> [H_element128,C_element138,N_element057,O_element118]
  conduct = 2
  density = 1
  expand = 3
  formula = G4_DNA_THYMINE
  name = G4_DNA_THYMINE
  specific = 4
FEATURE [App::DocumentObjectGroupPython] H_element129  label="H_element : 076"  # scripted group (container) (typed FeaturePython)
  n = 3
  ref = H_element
FEATURE [App::DocumentObjectGroupPython] C_element139  label="C_element : 084"  # scripted group (container) (typed FeaturePython)
  n = 4
  ref = C_element
FEATURE [App::DocumentObjectGroupPython] N_element058  label="N_element : 030"  # scripted group (container) (typed FeaturePython)
  n = 2
  ref = N_element
FEATURE [App::DocumentObjectGroupPython] O_element119  label="O_element : 072"  # scripted group (container) (typed FeaturePython)
  n = 2
  ref = O_element
FEATURE [App::DocumentObjectGroupPython] G4_DNA_URACIL  # scripted group (container) (typed FeaturePython)
  Dunit = g/cm3
  Dvalue = 1
  Group = -> [H_element129,C_element139,N_element058,O_element119]
  conduct = 2
  density = 1
  expand = 3
  formula = G4_DNA_URACIL
  name = G4_DNA_URACIL
  specific = 4
FEATURE [App::DocumentObjectGroupPython] H_element130  label="H_element : 077"  # scripted group (container) (typed FeaturePython)
  n = 10
  ref = H_element
FEATURE [App::DocumentObjectGroupPython] C_element140  label="C_element : 085"  # scripted group (container) (typed FeaturePython)
  n = 10
  ref = C_element
FEATURE [App::DocumentObjectGroupPython] N_element059  label="N_element : 031"  # scripted group (container) (typed FeaturePython)
  n = 5
  ref = N_element
FEATURE [App::DocumentObjectGroupPython] O_element120  label="O_element : 073"  # scripted group (container) (typed FeaturePython)
  n = 4
  ref = O_element
FEATURE [App::DocumentObjectGroupPython] G4_DNA_ADENOSINE  # scripted group (container) (typed FeaturePython)
  Dunit = g/cm3
  Dvalue = 1
  Group = -> [H_element130,C_element140,N_element059,O_element120]
  conduct = 2
  density = 1
  expand = 3
  formula = G4_DNA_ADENOSINE
  name = G4_DNA_ADENOSINE
  specific = 4
FEATURE [App::DocumentObjectGroupPython] H_element131  label="H_element : 078"  # scripted group (container) (typed FeaturePython)
  n = 10
  ref = H_element
FEATURE [App::DocumentObjectGroupPython] C_element141  label="C_element : 086"  # scripted group (container) (typed FeaturePython)
  n = 10
  ref = C_element
FEATURE [App::DocumentObjectGroupPython] N_element060  label="N_element : 032"  # scripted group (container) (typed FeaturePython)
  n = 5
  ref = N_element
FEATURE [App::DocumentObjectGroupPython] O_element121  label="O_element : 074"  # scripted group (container) (typed FeaturePython)
  n = 5
  ref = O_element
FEATURE [App::DocumentObjectGroupPython] G4_DNA_GUANOSINE  # scripted group (container) (typed FeaturePython)
  Dunit = g/cm3
  Dvalue = 1
  Group = -> [H_element131,C_element141,N_element060,O_element121]
  conduct = 2
  density = 1
  expand = 3
  formula = G4_DNA_GUANOSINE
  name = G4_DNA_GUANOSINE
  specific = 4
FEATURE [App::DocumentObjectGroupPython] H_element132  label="H_element : 079"  # scripted group (container) (typed FeaturePython)
  n = 10
  ref = H_element
FEATURE [App::DocumentObjectGroupPython] C_element142  label="C_element : 087"  # scripted group (container) (typed FeaturePython)
  n = 9
  ref = C_element
FEATURE [App::DocumentObjectGroupPython] N_element061  label="N_element : 033"  # scripted group (container) (typed FeaturePython)
  n = 3
  ref = N_element
FEATURE [App::DocumentObjectGroupPython] O_element122  label="O_element : 075"  # scripted group (container) (typed FeaturePython)
  n = 5
  ref = O_element
FEATURE [App::DocumentObjectGroupPython] G4_DNA_CYTIDINE  # scripted group (container) (typed FeaturePython)
  Dunit = g/cm3
  Dvalue = 1
  Group = -> [H_element132,C_element142,N_element061,O_element122]
  conduct = 2
  density = 1
  expand = 3
  formula = G4_DNA_CYTIDINE
  name = G4_DNA_CYTIDINE
  specific = 4
FEATURE [App::DocumentObjectGroupPython] H_element133  label="H_element : 080"  # scripted group (container) (typed FeaturePython)
  n = 9
  ref = H_element
FEATURE [App::DocumentObjectGroupPython] C_element143  label="C_element : 088"  # scripted group (container) (typed FeaturePython)
  n = 9
  ref = C_element
FEATURE [App::DocumentObjectGroupPython] N_element062  label="N_element : 034"  # scripted group (container) (typed FeaturePython)
  n = 2
  ref = N_element
FEATURE [App::DocumentObjectGroupPython] O_element123  label="O_element : 076"  # scripted group (container) (typed FeaturePython)
  n = 6
  ref = O_element
FEATURE [App::DocumentObjectGroupPython] G4_DNA_URIDINE  # scripted group (container) (typed FeaturePython)
  Dunit = g/cm3
  Dvalue = 1
  Group = -> [H_element133,C_element143,N_element062,O_element123]
  conduct = 2
  density = 1
  expand = 3
  formula = G4_DNA_URIDINE
  name = G4_DNA_URIDINE
  specific = 4
FEATURE [App::DocumentObjectGroupPython] H_element134  label="H_element : 081"  # scripted group (container) (typed FeaturePython)
  n = 11
  ref = H_element
FEATURE [App::DocumentObjectGroupPython] C_element144  label="C_element : 089"  # scripted group (container) (typed FeaturePython)
  n = 10
  ref = C_element
FEATURE [App::DocumentObjectGroupPython] N_element063  label="N_element : 035"  # scripted group (container) (typed FeaturePython)
  n = 2
  ref = N_element
FEATURE [App::DocumentObjectGroupPython] O_element124  label="O_element : 077"  # scripted group (container) (typed FeaturePython)
  n = 6
  ref = O_element
FEATURE [App::DocumentObjectGroupPython] G4_DNA_METHYLURIDINE  # scripted group (container) (typed FeaturePython)
  Dunit = g/cm3
  Dvalue = 1
  Group = -> [H_element134,C_element144,N_element063,O_element124]
  conduct = 2
  density = 1
  expand = 3
  formula = G4_DNA_METHYLURIDINE
  name = G4_DNA_METHYLURIDINE
  specific = 4
FEATURE [App::DocumentObjectGroupPython] P_element014  label="P_element : 003"  # scripted group (container) (typed FeaturePython)
  n = 1
  ref = P_element
FEATURE [App::DocumentObjectGroupPython] O_element125  label="O_element : 078"  # scripted group (container) (typed FeaturePython)
  n = 3
  ref = O_element
FEATURE [App::DocumentObjectGroupPython] G4_DNA_MONOPHOSPHATE  # scripted group (container) (typed FeaturePython)
  Dunit = g/cm3
  Dvalue = 1
  Group = -> [P_element014,O_element125]
  conduct = 2
  density = 1
  expand = 3
  formula = G4_DNA_MONOPHOSPHATE
  name = G4_DNA_MONOPHOSPHATE
  specific = 4
FEATURE [App::DocumentObjectGroupPython] H_element135  label="H_element : 082"  # scripted group (container) (typed FeaturePython)
  n = 10
  ref = H_element
FEATURE [App::DocumentObjectGroupPython] C_element145  label="C_element : 090"  # scripted group (container) (typed FeaturePython)
  n = 10
  ref = C_element
FEATURE [App::DocumentObjectGroupPython] N_element064  label="N_element : 036"  # scripted group (container) (typed FeaturePython)
  n = 5
  ref = N_element
FEATURE [App::DocumentObjectGroupPython] O_element126  label="O_element : 079"  # scripted group (container) (typed FeaturePython)
  n = 7
  ref = O_element
FEATURE [App::DocumentObjectGroupPython] P_element015  label="P_element : 004"  # scripted group (container) (typed FeaturePython)
  n = 1
  ref = P_element
FEATURE [App::DocumentObjectGroupPython] G4_DNA_A  # scripted group (container) (typed FeaturePython)
  Dunit = g/cm3
  Dvalue = 1
  Group = -> [H_element135,C_element145,N_element064,O_element126,P_element015]
  conduct = 2
  density = 1
  expand = 3
  formula = G4_DNA_A
  name = G4_DNA_A
  specific = 4
FEATURE [App::DocumentObjectGroupPython] H_element136  label="H_element : 083"  # scripted group (container) (typed FeaturePython)
  n = 10
  ref = H_element
FEATURE [App::DocumentObjectGroupPython] C_element146  label="C_element : 091"  # scripted group (container) (typed FeaturePython)
  n = 10
  ref = C_element
FEATURE [App::DocumentObjectGroupPython] N_element065  label="N_element : 037"  # scripted group (container) (typed FeaturePython)
  n = 5
  ref = N_element
FEATURE [App::DocumentObjectGroupPython] O_element127  label="O_element : 8"  # scripted group (container) (typed FeaturePython)
  n = 8
  ref = O_element
FEATURE [App::DocumentObjectGroupPython] P_element016  label="P_element : 005"  # scripted group (container) (typed FeaturePython)
  n = 1
  ref = P_element
FEATURE [App::DocumentObjectGroupPython] G4_DNA_G  # scripted group (container) (typed FeaturePython)
  Dunit = g/cm3
  Dvalue = 1
  Group = -> [H_element136,C_element146,N_element065,O_element127,P_element016]
  conduct = 2
  density = 1
  expand = 3
  formula = G4_DNA_G
  name = G4_DNA_G
  specific = 4
FEATURE [App::DocumentObjectGroupPython] H_element137  label="H_element : 084"  # scripted group (container) (typed FeaturePython)
  n = 10
  ref = H_element
FEATURE [App::DocumentObjectGroupPython] C_element147  label="C_element : 092"  # scripted group (container) (typed FeaturePython)
  n = 9
  ref = C_element
FEATURE [App::DocumentObjectGroupPython] N_element066  label="N_element : 038"  # scripted group (container) (typed FeaturePython)
  n = 3
  ref = N_element
FEATURE [App::DocumentObjectGroupPython] O_element128  label="O_element : 080"  # scripted group (container) (typed FeaturePython)
  n = 8
  ref = O_element
FEATURE [App::DocumentObjectGroupPython] P_element017  label="P_element : 006"  # scripted group (container) (typed FeaturePython)
  n = 1
  ref = P_element
FEATURE [App::DocumentObjectGroupPython] G4_DNA_C  # scripted group (container) (typed FeaturePython)
  Dunit = g/cm3
  Dvalue = 1
  Group = -> [H_element137,C_element147,N_element066,O_element128,P_element017]
  conduct = 2
  density = 1
  expand = 3
  formula = G4_DNA_C
  name = G4_DNA_C
  specific = 4
FEATURE [App::DocumentObjectGroupPython] H_element138  label="H_element : 085"  # scripted group (container) (typed FeaturePython)
  n = 9
  ref = H_element
FEATURE [App::DocumentObjectGroupPython] C_element148  label="C_element : 093"  # scripted group (container) (typed FeaturePython)
  n = 9
  ref = C_element
FEATURE [App::DocumentObjectGroupPython] N_element067  label="N_element : 039"  # scripted group (container) (typed FeaturePython)
  n = 2
  ref = N_element
FEATURE [App::DocumentObjectGroupPython] O_element129  label="O_element : 9"  # scripted group (container) (typed FeaturePython)
  n = 9
  ref = O_element
FEATURE [App::DocumentObjectGroupPython] P_element018  label="P_element : 007"  # scripted group (container) (typed FeaturePython)
  n = 1
  ref = P_element
FEATURE [App::DocumentObjectGroupPython] G4_DNA_U  # scripted group (container) (typed FeaturePython)
  Dunit = g/cm3
  Dvalue = 1
  Group = -> [H_element138,C_element148,N_element067,O_element129,P_element018]
  conduct = 2
  density = 1
  expand = 3
  formula = G4_DNA_U
  name = G4_DNA_U
  specific = 4
FEATURE [App::DocumentObjectGroupPython] H_element139  label="H_element : 086"  # scripted group (container) (typed FeaturePython)
  n = 11
  ref = H_element
FEATURE [App::DocumentObjectGroupPython] C_element149  label="C_element : 094"  # scripted group (container) (typed FeaturePython)
  n = 10
  ref = C_element
FEATURE [App::DocumentObjectGroupPython] N_element068  label="N_element : 040"  # scripted group (container) (typed FeaturePython)
  n = 2
  ref = N_element
FEATURE [App::DocumentObjectGroupPython] O_element130  label="O_element : 081"  # scripted group (container) (typed FeaturePython)
  n = 9
  ref = O_element
FEATURE [App::DocumentObjectGroupPython] P_element019  label="P_element : 008"  # scripted group (container) (typed FeaturePython)
  n = 1
  ref = P_element
FEATURE [App::DocumentObjectGroupPython] G4_DNA_MU  # scripted group (container) (typed FeaturePython)
  Dunit = g/cm3
  Dvalue = 1
  Group = -> [H_element139,C_element149,N_element068,O_element130,P_element019]
  conduct = 2
  density = 1
  expand = 3
  formula = G4_DNA_MU
  name = G4_DNA_MU
  specific = 4
FEATURE [App::DocumentObjectGroupPython] BioChemical  # scripted group (container) (typed FeaturePython)
  Group = -> [G4_CYTOSINE,G4_THYMINE,G4_URACIL,G4_DNA_ADENINE,G4_DNA_GUANINE,G4_DNA_CYTOSINE,G4_DNA_THYMINE,G4_DNA_URACIL,G4_DNA_ADENOSINE,G4_DNA_GUANOSINE,G4_DNA_CYTIDINE,G4_DNA_URIDINE,G4_DNA_METHYLURIDINE,G4_DNA_MONOPHOSPHATE,G4_DNA_A,G4_DNA_G,G4_DNA_C,G4_DNA_U,G4_DNA_MU]
FEATURE [App::DocumentObjectGroupPython] G4Materials  # scripted group (container) (typed FeaturePython)
  Group = -> [NIST,Element,HEP,Space,BioChemical]
  version = 1
FEATURE [App::DocumentObjectGroupPython] Geant4  # scripted group (container) (typed FeaturePython)
  Group = -> [G4Isotopes,G4Elements,G4Materials]
FEATURE [App::DocumentObjectGroupPython] Materials  # scripted group (container) (typed FeaturePython)
  Group = -> [Geant4]
FEATURE [Part::FeaturePython] GDMLBox_WorldBox  # WARN: FeaturePython — macro-defined, semantics opaque (R4)
  lunit = 2
  material = 5
  x = 6000
  y = 6200
  z = 6000
FEATURE [Sketcher::SketchObject] Sketch
  ArcFitTolerance = 1e-06
  AttachmentSupport = -> [YZ_Plane001]
  FullyConstrained = true
  MakeInternals = false
  MapMode = 5
  Placement = pos=(0,0,0) rot=(0.57735,0.57735,0.57735;2.0944rad)
  expr: Constraints[16] = <<params>>.base_radius
  expr: Constraints[17] = <<params>>.splash_thickness
  expr: Constraints[18] = <<params>>.splash_height
  expr: Constraints[21] = <<params>>.cone_radius
  expr: Constraints[22] = <<params>>.cone_height
  expr: Constraints[23] = <<params>>.base_height
  sketch-geometry (8):
    g0: LineSegment StartX=200 StartY=0 StartZ=0 EndX=200 EndY=200 EndZ=0
    g1: LineSegment StartX=200 StartY=200 StartZ=0 EndX=0 EndY=200 EndZ=0
    g2: LineSegment StartX=0 StartY=100 StartZ=0 EndX=0 EndY=0 EndZ=0
    g3: LineSegment StartX=0 StartY=100 StartZ=0 EndX=0 EndY=150 EndZ=0
    g4: LineSegment StartX=0 StartY=150 StartZ=0 EndX=-500 EndY=150 EndZ=0
    g5: LineSegment StartX=-500 StartY=150 StartZ=0 EndX=-500 EndY=200 EndZ=0
    g6: LineSegment StartX=-500 StartY=200 StartZ=0 EndX=0 EndY=200 EndZ=0
    g7: LineSegment StartX=0 StartY=0 StartZ=0 EndX=200 EndY=0 EndZ=0
  constraints (24):
    c: PointOnObject(g2,g-1)
    c: PointOnObject(g0,g-1)
    c: Vertical(g0)
    c: Coincident(g0,g1)
    c: Horizontal(g1)
    c: PointOnObject(g2,g-2)
    c: PointOnObject(g1,g-2)
    c: Coincident(g2,g3)
    c: PointOnObject(g3,g-2)
    c: Coincident(g3,g4)
    c: Horizontal(g4)
    c: Coincident(g4,g5)
    c: Vertical(g5)
    c: Coincident(g5,g6)
    c: Coincident(g6,g1)
    c: Horizontal(g6)
    c: DistanceY(g0,g0) = 200
    c: DistanceY(g5,g5) = 50
    c: DistanceX(g6,g6) = 500
    c: Coincident(g7,g2)
    c: Coincident(g7,g0)
    c: Distance(g2,g-1) = 100
    c: Distance(g2,g-2) = 0
    c: Distance(g0,g3) = 200
FEATURE [Spreadsheet::Sheet] Spreadsheet  label="params"
  cells = A1='Base Beam Dump Radius; B1='base_radius; C1(base_radius)=200; A2='Base Beam Dump Height; B2='base_height; C2(base_height)=200; A3='Gamma Splash Shield Thickness; B3='splash_thickness; C3(splash_thickness)=50; A4='Gamme Splash Shield Height; B4='splash_height; C4(splash_height)=500; A5='Center Cone Height; B5='cone_height; C5(cone_height)=0; A6='Center Cone Radius; B6='cone_radius; C6(cone_radius)=100; A8='HDPE Base Thickness; B8='hdpe_base_thickness; C8(hdpe_base_thickness)=100; A9='HDPE Side Thickness; B9='hdpe_side_thickness; C9(hdpe_side_thickness)=100; A11='Minimal Opening Radius; B11='min_open_radius; C11(min_open_radius)=100; A13='Wall Shield Size; B13='wall_shield_size; C13(wall_shield_size)=3000; A14='Wall Shield Thickness; B14='wall_shield_thickness; C14(wall_shield_thickness)=450; A15='Cap Upstream Thickness; B15='cap_us_thickness; C15(cap_us_thickness)=450; A16='Cap Downstream Thickness; B16='cap_ds_thickness; C16(cap_ds_thickness)=650; A17='Containment Length; B17='containment_length; C17(containment_length)=4000
FEATURE [PartDesign::Revolution] Revolution
  Angle = 360
  Angle2 = 60
  Axis = (1e-16,1,-1e-16)
  Base = (0,0,0)
  Placement = pos=(0,0,0) rot=(1,1,1;2.0944rad)
  Profile = -> Sketch
  ReferenceAxis = -> Y_Axis001
  Refine = true
  Suppressed = false
  Type = 0
FEATURE [PartDesign::Body] Body  label="Body_W"
  AllowCompound = false
  Group = -> [Sketch,Revolution]
  Origin = -> Origin001
  Tip = -> Revolution
FEATURE [Sketcher::SketchObject] Sketch001
  ArcFitTolerance = 1e-06
  AttachmentSupport = -> [YZ_Plane002]
  FullyConstrained = true
  MakeInternals = false
  MapMode = 5
  Placement = pos=(0,0,0) rot=(0.57735,0.57735,0.57735;2.0944rad)
  expr: Constraints[18] = <<params>>.base_radius
  expr: Constraints[19] = <<params>>.base_height
  expr: Constraints[20] = <<params>>.cone_height
  expr: Constraints[21] = <<params>>.cone_radius
  expr: Constraints[22] = <<params>>.splash_thickness
  expr: Constraints[23] = <<params>>.splash_height
  expr: Constraints[38] = <<params>>.hdpe_base_thickness
  expr: Constraints[39] = <<params>>.hdpe_side_thickness
  expr: Constraints[40] = <<params>>.hdpe_side_thickness
  expr: Constraints[41] = <<params>>.min_open_radius
  expr: Constraints[56] = <<params>>.splash_thickness
  expr: Constraints[57] = <<params>>.hdpe_side_thickness
  expr: Constraints[58] = 50 mm
  sketch-geometry (21):
    g0: LineSegment [constr] StartX=0 StartY=0 StartZ=0 EndX=200 EndY=0 EndZ=0
    g1: LineSegment [constr] StartX=200 StartY=0 StartZ=0 EndX=200 EndY=200 EndZ=0
    g2: LineSegment [constr] StartX=200 StartY=200 StartZ=0 EndX=0 EndY=200 EndZ=0
    g3: LineSegment [constr] StartX=0 StartY=100 StartZ=0 EndX=0 EndY=0 EndZ=0
    g4: LineSegment [constr] StartX=0 StartY=100 StartZ=0 EndX=0 EndY=150 EndZ=0
    g5: LineSegment [constr] StartX=0 StartY=150 StartZ=0 EndX=-500 EndY=150 EndZ=0
    g6: LineSegment [constr] StartX=-500 StartY=150 StartZ=0 EndX=-500 EndY=200 EndZ=0
    g7: LineSegment [constr] StartX=-500 StartY=200 StartZ=0 EndX=0 EndY=200 EndZ=0
    g8: LineSegment StartX=-500 StartY=200 StartZ=0 EndX=200 EndY=200 EndZ=0
    g9: LineSegment StartX=200 StartY=200 StartZ=0 EndX=200 EndY=0 EndZ=0
    g10: LineSegment StartX=200 StartY=0 StartZ=0 EndX=300 EndY=0 EndZ=0
    g11: LineSegment StartX=300 StartY=0 StartZ=0 EndX=300 EndY=300 EndZ=0
    g12: LineSegment StartX=300 StartY=300 StartZ=0 EndX=-600 EndY=300 EndZ=0
    g13: LineSegment StartX=-600 StartY=300 StartZ=0 EndX=-600 EndY=100 EndZ=0
    g14: LineSegment StartX=-600 StartY=100 StartZ=0 EndX=-500 EndY=100 EndZ=0
    g15: LineSegment StartX=-500 StartY=100 StartZ=0 EndX=-50 EndY=100 EndZ=0
    g16: LineSegment StartX=-50 StartY=100 StartZ=0 EndX=-50 EndY=0 EndZ=0
    g17: LineSegment StartX=-50 StartY=0 StartZ=0 EndX=0 EndY=0 EndZ=0
    g18: LineSegment StartX=0 StartY=0 StartZ=0 EndX=0 EndY=150 EndZ=0
    g19: LineSegment StartX=0 StartY=150 StartZ=0 EndX=-500 EndY=150 EndZ=0
    g20: LineSegment StartX=-500 StartY=150 StartZ=0 EndX=-500 EndY=200 EndZ=0
  constraints (59):
    c: PointOnObject(g0,g-1)
    c: PointOnObject(g0,g-1)
    c: Coincident(g0,g1)
    c: Vertical(g1)
    c: Coincident(g1,g2)
    c: Horizontal(g2)
    c: PointOnObject(g3,g-2)
    c: Coincident(g3,g0)
    c: PointOnObject(g2,g-2)
    c: Coincident(g3,g4)
    c: PointOnObject(g4,g-2)
    c: Coincident(g4,g5)
    c: Horizontal(g5)
    c: Coincident(g5,g6)
    c: Vertical(g6)
    c: Coincident(g6,g7)
    c: Coincident(g7,g2)
    c: Horizontal(g7)
    c: DistanceY(g1,g1) = 200
    c: Distance(g0,g-2) = 200
    c: Distance(g0,g-2) = 0
    c: Distance(g3,g0) = 100
    c: DistanceY(g6,g6) = 50
    c: DistanceX(g7,g7) = 500
    c: Coincident(g6,g8)
    c: Coincident(g8,g1)
    c: Coincident(g8,g9)
    c: Coincident(g9,g0)
    c: Coincident(g9,g10)
    c: PointOnObject(g10,g-1)
    c: Coincident(g10,g11)
    c: Vertical(g11)
    c: Coincident(g11,g12)
    c: Horizontal(g12)
    c: Coincident(g12,g13)
    c: Vertical(g13)
    c: Coincident(g13,g14)
    c: Horizontal(g14)
    c: DistanceX(g10,g10) = 100
    c: Distance(g11,g8) = 100
    c: DistanceX(g14,g14) = 100
    c: Distance(g14,g-1) = 100
    c: Coincident(g14,g15)
    c: Horizontal(g15)
    c: Coincident(g15,g16)
    c: PointOnObject(g16,g-1)
    c: Vertical(g16)
    c: Coincident(g16,g17)
    c: Coincident(g17,g-1)
    c: Coincident(g17,g18)
    c: PointOnObject(g18,g-2)
    c: Coincident(g18,g19)
    c: Horizontal(g19)
    c: Coincident(g19,g20)
    c: Coincident(g20,g8)
    c: Vertical(g20)
    c: Distance(g19,g8) = 50
    c: Distance(g12,g20) = 100
    c: DistanceX(g17,g17) = 50
FEATURE [PartDesign::Revolution] Revolution001
  Angle = 360
  Angle2 = 60
  Axis = (1e-16,1,-1e-16)
  Base = (0,0,0)
  Placement = pos=(0,0,0) rot=(1,1,1;2.0944rad)
  Profile = -> Sketch001
  ReferenceAxis = -> Y_Axis002
  Refine = true
  Suppressed = false
  Type = 0
FEATURE [PartDesign::Body] Body001  label="Body_HDPE"
  AllowCompound = false
  Group = -> [Sketch001,Revolution001]
  Origin = -> Origin002
  Tip = -> Revolution001
FEATURE [Sketcher::SketchObject] Sketch002
  ArcFitTolerance = 1e-06
  AttachmentSupport = -> [XZ_Plane003]
  FullyConstrained = true
  MakeInternals = false
  MapMode = 5
  Placement = pos=(0,0,0) rot=(1,0,0;1.5708rad)
  expr: Constraints[10] = <<params>>.wall_shield_size
  expr: Constraints[21] = <<params>>.wall_shield_thickness
  sketch-geometry (8):
    g0: LineSegment StartX=-1500 StartY=1500 StartZ=0 EndX=-1500 EndY=-1500 EndZ=0
    g1: LineSegment StartX=-1500 StartY=-1500 StartZ=0 EndX=1500 EndY=-1500 EndZ=0
    g2: LineSegment StartX=1500 StartY=-1500 StartZ=0 EndX=1500 EndY=1500 EndZ=0
    g3: LineSegment StartX=1500 StartY=1500 StartZ=0 EndX=-1500 EndY=1500 EndZ=0
    g4: LineSegment StartX=-1050 StartY=1050 StartZ=0 EndX=-1050 EndY=-1050 EndZ=0
    g5: LineSegment StartX=-1050 StartY=-1050 StartZ=0 EndX=1050 EndY=-1050 EndZ=0
    g6: LineSegment StartX=1050 StartY=-1050 StartZ=0 EndX=1050 EndY=1050 EndZ=0
    g7: LineSegment StartX=1050 StartY=1050 StartZ=0 EndX=-1050 EndY=1050 EndZ=0
  constraints (22):
    c: Coincident(g0,g1)
    c: Coincident(g1,g2)
    c: Coincident(g2,g3)
    c: Coincident(g3,g0)
    c: Vertical(g0)
    c: Vertical(g2)
    c: Horizontal(g1)
    c: Horizontal(g3)
    c: Symmetric(g1,g0,g-1)
    c: Equal(g3,g0)
    c: DistanceX(g3,g3) = 3000
    c: Coincident(g4,g5)
    c: Coincident(g5,g6)
    c: Coincident(g6,g7)
    c: Coincident(g7,g4)
    c: Vertical(g4)
    c: Vertical(g6)
    c: Horizontal(g5)
    c: Horizontal(g7)
    c: Symmetric(g5,g4,g-1)
    c: Equal(g4,g7)
    c: Distance(g6,g3) = 450
FEATURE [PartDesign::Pad] Pad
  Direction = (0,-1,2e-16)
  Length = 4000
  Length2 = 10
  Midplane = true
  Placement = pos=(0,0,0) rot=(1,0,0;1.5708rad)
  Profile = -> Sketch002
  ReferenceAxis = -> Sketch002 [N_Axis]
  Refine = true
  Suppressed = false
  Type = 0
  expr: Length = <<params>>.containment_length
FEATURE [Sketcher::SketchObject] Sketch003
  ArcFitTolerance = 1e-06
  AttachmentSupport = -> [Pad]
  ExternalGeometry = -> [Pad]
  FullyConstrained = true
  MakeInternals = false
  MapMode = 5
  Placement = pos=(0,-2000,0) rot=(1,0,0;1.5708rad)
  sketch-geometry (4):
    g0: LineSegment StartX=-1500 StartY=1500 StartZ=0 EndX=-1500 EndY=-1500 EndZ=0
    g1: LineSegment StartX=-1500 StartY=-1500 StartZ=0 EndX=1500 EndY=-1500 EndZ=0
    g2: LineSegment StartX=1500 StartY=-1500 StartZ=0 EndX=1500 EndY=1500 EndZ=0
    g3: LineSegment StartX=1500 StartY=1500 StartZ=0 EndX=-1500 EndY=1500 EndZ=0
  constraints (11):
    c: Coincident(g0,g1)
    c: Coincident(g1,g2)
    c: Coincident(g2,g3)
    c: Coincident(g3,g0)
    c: Vertical(g0)
    c: Vertical(g2)
    c: Horizontal(g1)
    c: Horizontal(g3)
    c: Symmetric(g1,g0,g-1)
    c: Equal(g3,g-3)
    c: Equal(g-3,g0)
FEATURE [PartDesign::Pad] Pad001
  BaseFeature = -> Pad
  Direction = (0,-1,2e-16)
  Length = 450
  Length2 = 10
  Placement = pos=(0,0,0) rot=(1,0,0;1.5708rad)
  Profile = -> Sketch003
  ReferenceAxis = -> Sketch003 [N_Axis]
  Refine = true
  Suppressed = false
  Type = 0
  expr: Length = <<params>>.cap_us_thickness
FEATURE [Sketcher::SketchObject] Sketch004
  ArcFitTolerance = 1e-06
  AttachmentSupport = -> [Pad001]
  ExternalGeometry = -> [Pad001]
  FullyConstrained = true
  MakeInternals = false
  MapMode = 5
  Placement = pos=(0,2000,0) rot=(-1,0,0;1.5708rad)
  sketch-geometry (4):
    g0: LineSegment StartX=-1500 StartY=1500 StartZ=0 EndX=-1500 EndY=-1500 EndZ=0
    g1: LineSegment StartX=-1500 StartY=-1500 StartZ=0 EndX=1500 EndY=-1500 EndZ=0
    g2: LineSegment StartX=1500 StartY=-1500 StartZ=0 EndX=1500 EndY=1500 EndZ=0
    g3: LineSegment StartX=1500 StartY=1500 StartZ=0 EndX=-1500 EndY=1500 EndZ=0
  constraints (11):
    c: Coincident(g0,g1)
    c: Coincident(g1,g2)
    c: Coincident(g2,g3)
    c: Coincident(g3,g0)
    c: Vertical(g0)
    c: Vertical(g2)
    c: Horizontal(g1)
    c: Horizontal(g3)
    c: Symmetric(g1,g0,g-1)
    c: Equal(g3,g0)
    c: Equal(g0,g-3)
FEATURE [PartDesign::Pad] Pad002
  BaseFeature = -> Pad001
  Direction = (0,1,2e-16)
  Length = 650
  Length2 = 10
  Placement = pos=(0,0,0) rot=(1,0,0;1.5708rad)
  Profile = -> Sketch004
  ReferenceAxis = -> Sketch004 [N_Axis]
  Refine = true
  Suppressed = false
  Type = 0
  expr: Length = <<params>>.cap_ds_thickness
FEATURE [PartDesign::Body] Body002  label="Body_WallShield"
  AllowCompound = false
  Group = -> [Sketch002,Pad,Sketch003,Pad001,Sketch004,Pad002]
  Origin = -> Origin003
  Tip = -> Pad002
FEATURE [Part::FeaturePython] GDMLTessellate_Body_WallShield  # WARN: FeaturePython — macro-defined, semantics opaque (R4)
  facets = 24
  lunit = 2
  material = 45
  vertex = 16
FEATURE [App::Part] LV_Body_WallShield
  Group = -> [GDMLTessellate_Body_WallShield]
  Origin = -> Origin004
  SkinSurface = 0
FEATURE [Part::FeaturePython] GDMLTessellate_Body_W  # WARN: FeaturePython — macro-defined, semantics opaque (R4)
  facets = 1048
  lunit = 2
  material = 253
  vertex = 526
FEATURE [App::Part] LV_Body_W
  Group = -> [GDMLTessellate_Body_W]
  Origin = -> Origin005
  Placement = pos=(0,1500,0) rot=(0,0,1;0rad)
  SkinSurface = 0
FEATURE [Part::FeaturePython] GDMLTessellate_Body_HDPE  # WARN: FeaturePython — macro-defined, semantics opaque (R4)
  facets = 2136
  lunit = 2
  material = 121
  vertex = 1072
FEATURE [App::Part] LV_Body_HDPE
  Group = -> [GDMLTessellate_Body_HDPE]
  Origin = -> Origin006
  Placement = pos=(0,1500,0) rot=(0,0,1;0rad)
  SkinSurface = 0
FEATURE [Sketcher::SketchObject] Sketch005
  ArcFitTolerance = 1e-06
  AttachmentSupport = -> [XZ_Plane007]
  FullyConstrained = true
  MakeInternals = false
  MapMode = 5
  Placement = pos=(0,0,0) rot=(1,0,0;1.5708rad)
  sketch-geometry (2):
    g0: Circle CenterX=0 CenterY=0 CenterZ=0 NormalX=0 NormalY=0 NormalZ=1 AngleXU=0 Radius=2500
    g1: Circle CenterX=0 CenterY=0 CenterZ=0 NormalX=0 NormalY=0 NormalZ=1 AngleXU=0 Radius=2250
  constraints (4):
    c: Coincident(g0,g-1)
    c: Coincident(g1,g0)
    c: Diameter(g0) = 5000
    c: Diameter(g1) = 4500
FEATURE [PartDesign::Pad] Pad003
  Direction = (0,-1,2e-16)
  Length = 5500
  Length2 = 10
  Midplane = true
  Placement = pos=(0,0,0) rot=(1,0,0;1.5708rad)
  Profile = -> Sketch005
  ReferenceAxis = -> Sketch005 [N_Axis]
  Refine = true
  Suppressed = false
  Type = 0
FEATURE [Sketcher::SketchObject] Sketch006
  ArcFitTolerance = 1e-06
  AttachmentSupport = -> [Pad003]
  ExternalGeometry = -> [Pad003]
  FullyConstrained = true
  MakeInternals = false
  MapMode = 5
  Placement = pos=(0,-2750,0) rot=(1,0,0;1.5708rad)
  sketch-geometry (1):
    g0: Circle CenterX=0 CenterY=0 CenterZ=0 NormalX=0 NormalY=0 NormalZ=1 AngleXU=0 Radius=2500
  constraints (2):
    c: Coincident(g0,g-1)
    c: Equal(g0,g-3)
FEATURE [PartDesign::Pad] Pad004
  BaseFeature = -> Pad003
  Direction = (0,-1,2e-16)
  Length = 250
  Length2 = 10
  Placement = pos=(0,0,0) rot=(1,0,0;1.5708rad)
  Profile = -> Sketch006
  ReferenceAxis = -> Sketch006 [N_Axis]
  Refine = true
  Suppressed = false
  Type = 0
FEATURE [Sketcher::SketchObject] Sketch007
  ArcFitTolerance = 1e-06
  AttachmentSupport = -> [Pad004]
  ExternalGeometry = -> [Pad004]
  FullyConstrained = true
  MakeInternals = false
  MapMode = 5
  Placement = pos=(0,2750,0) rot=(-1,0,0;1.5708rad)
  sketch-geometry (1):
    g0: Circle CenterX=0 CenterY=0 CenterZ=0 NormalX=0 NormalY=0 NormalZ=1 AngleXU=0 Radius=2500
  constraints (2):
    c: Coincident(g0,g-1)
    c: Equal(g0,g-3)
FEATURE [PartDesign::Pad] Pad005
  BaseFeature = -> Pad004
  Direction = (0,1,2e-16)
  Length = 250
  Length2 = 10
  Placement = pos=(0,0,0) rot=(1,0,0;1.5708rad)
  Profile = -> Sketch007
  ReferenceAxis = -> Sketch007 [N_Axis]
  Refine = true
  Suppressed = false
  Type = 0
FEATURE [PartDesign::Body] Body003  label="Body_Detector"
  AllowCompound = false
  Group = -> [Sketch005,Pad003,Sketch006,Pad004,Sketch007,Pad005]
  Origin = -> Origin007
  Tip = -> Pad005
FEATURE [Part::FeaturePython] GDMLTessellate_Body_Detector  # WARN: FeaturePython — macro-defined, semantics opaque (R4)
  facets = 3868
  lunit = 2
  material = 5
  vertex = 1938
FEATURE [App::Part] LV_Body_Detector
  Group = -> [GDMLTessellate_Body_Detector]
  Origin = -> Origin008
  SkinSurface = 0
FEATURE [App::Part] worldVOL
  Group = -> [GDMLBox_WorldBox,LV_Body_WallShield,LV_Body_W,LV_Body_HDPE,LV_Body_Detector]
  Origin = -> Origin
